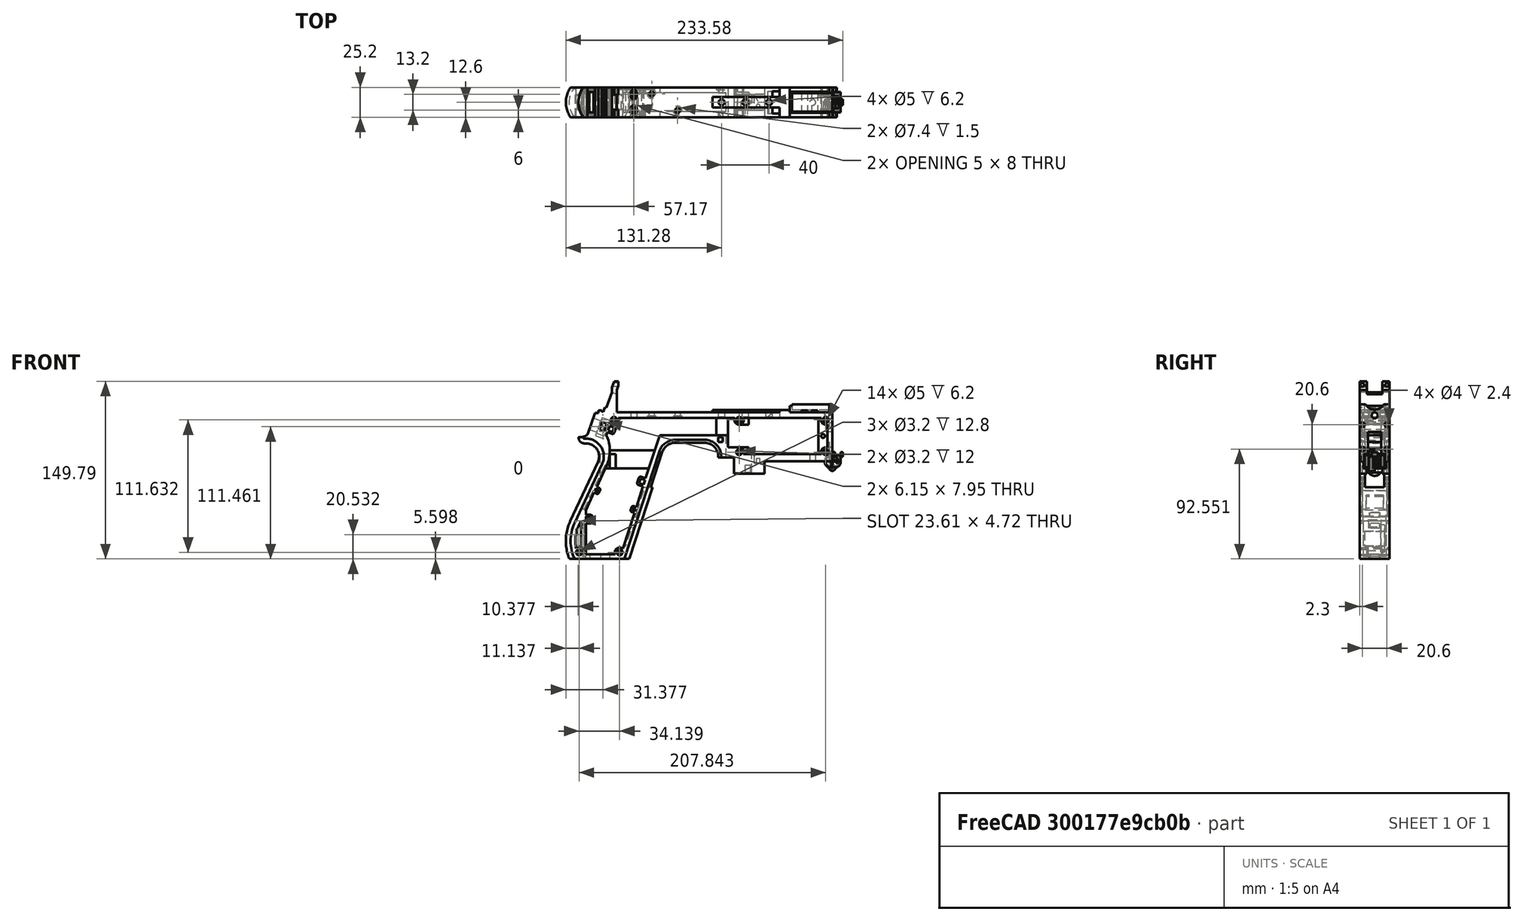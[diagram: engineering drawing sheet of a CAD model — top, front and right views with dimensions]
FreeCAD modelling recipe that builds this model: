
FCSTD DOCUMENT  (FreeCAD 1.0R39319 (Git))
Label: PICON-OF_ver_41
License: All rights reserved
LicenseURL: https://en.wikipedia.org/wiki/All_rights_reserved
objects: Sketcher::SketchObject×109, Part::Extrusion×52, Part::Cut×41, PartDesign::Pad×29, PartDesign::Pocket×18, PartDesign::Chamfer×15, PartDesign::Body×10, PartDesign::Fillet×6, PartDesign::SubtractivePipe×4, Part::Part2DObjectPython×4, PartDesign::SubtractiveLoft×4, PartDesign::Plane×2, PartDesign::SubShapeBinder×2, Part::Sweep×1, PartDesign::ShapeBinder×1, Part::MultiFuse×1, Mesh::Feature×1
note: 560 computed .brp shape members not serialized (recipe doc carries the construction recipe); baked Part::Feature solids carry a one-line shape summary decoded from their .brp

FEATURE [Sketcher::SketchObject] Sketch  label="corpo principale"
  ArcFitTolerance = 1e-06
  AttacherType = Attacher::AttachEngine3D
  AttachmentSupport = -> [XZ_Plane]
  FullyConstrained = true
  MakeInternals = false
  MapMode = 5
  Placement = pos=(0,0,0) rot=(1,0,0;1.5708rad)
  sketch-geometry (65):
    g0: LineSegment StartX=0 StartY=0 StartZ=0 EndX=-57.2 EndY=0 EndZ=0
    g1: LineSegment StartX=-57.2 StartY=0 StartZ=0 EndX=-57.2 EndY=-10.4 EndZ=0
    g2: LineSegment StartX=-57.2 StartY=-10.4 StartZ=0 EndX=-82.8 EndY=-10.4 EndZ=0
    g3: LineSegment StartX=-82.8 StartY=-10.4 StartZ=0 EndX=-82.8 EndY=3.2 EndZ=0
    g4: LineSegment StartX=-82.8 StartY=3.2 StartZ=0 EndX=-93.6 EndY=3.2 EndZ=0
    g5: LineSegment StartX=-93.6 StartY=3.2 StartZ=0 EndX=-93.6 EndY=4 EndZ=0
    g6: LineSegment StartX=-107.6 StartY=18 StartZ=0 EndX=-132.428 EndY=18 EndZ=0
    g7: LineSegment StartX=-145.743 StartY=8.32624 StartZ=0 EndX=-175.232 EndY=-82.4316 EndZ=0
    g8: LineSegment StartX=-175.232 StartY=-82.4316 StartZ=0 EndX=-217.232 EndY=-82.4316 EndZ=0
    g9: LineSegment StartX=-217.232 StartY=-52.1862 StartZ=0 EndX=-193.988 EndY=-2.33927 EndZ=0
    g10: LineSegment StartX=-206.196 StartY=23.0857 StartZ=0 EndX=-199.861 EndY=40.4914 EndZ=0
    g11: LineSegment StartX=-199.861 StartY=40.4914 StartZ=0 EndX=-197.061 EndY=40.4914 EndZ=0
    g12: LineSegment StartX=-197.061 StartY=40.4914 StartZ=0 EndX=-197.061 EndY=42.8914 EndZ=0
    g13: LineSegment StartX=-197.061 StartY=42.8914 StartZ=0 EndX=-194.261 EndY=42.8914 EndZ=0
    g14: LineSegment StartX=-194.261 StartY=42.8914 StartZ=0 EndX=-194.535 EndY=42.1397 EndZ=0
    g15: LineSegment StartX=-194.535 StartY=42.1397 StartZ=0 EndX=-193.031 EndY=41.5924 EndZ=0
    g16: LineSegment StartX=-193.031 StartY=41.5924 StartZ=0 EndX=-191.663 EndY=45.3512 EndZ=0
    g17: LineSegment StartX=-191.663 StartY=45.3512 StartZ=0 EndX=-190.536 EndY=44.9408 EndZ=0
    g18: LineSegment StartX=-190.536 StartY=44.9408 StartZ=0 EndX=-185.747 EndY=58.0965 EndZ=0
    g19: LineSegment StartX=-185.747 StartY=58.0965 StartZ=0 EndX=-185.747 EndY=62.0965 EndZ=0
    g20: LineSegment StartX=-185.747 StartY=62.0965 StartZ=0 EndX=-183.832 EndY=67.3588 EndZ=0
    g21: LineSegment StartX=-183.832 StartY=67.3588 StartZ=0 EndX=-180.232 EndY=67.3588 EndZ=0
    g22: LineSegment StartX=-180.232 StartY=67.3588 StartZ=0 EndX=-180.232 EndY=63.7588 EndZ=0
    g23: LineSegment StartX=-180.232 StartY=63.7588 StartZ=0 EndX=-181.6 EndY=60 EndZ=0
    g24: LineSegment StartX=-181.6 StartY=60 StartZ=0 EndX=-181.6 EndY=41.2 EndZ=0
    g25: LineSegment StartX=-181.6 StartY=41.2 StartZ=0 EndX=-100.8 EndY=41.2 EndZ=0
    g26: LineSegment StartX=-36 StartY=43.2 StartZ=0 EndX=-36 EndY=41.2 EndZ=0
    g27: LineSegment StartX=0 StartY=48 StartZ=0 EndX=0 EndY=0 EndZ=0
    g28: LineSegment StartX=-209.901 StartY=19.85 StartZ=0 EndX=-209.901 EndY=20.1 EndZ=0
    g29: LineSegment StartX=-208.001 StartY=22 StartZ=0 EndX=-207.747 EndY=22 EndZ=0
    g30: LineSegment StartX=-207.583 StartY=19 StartZ=0 EndX=-209.051 EndY=19 EndZ=0
    g31: ArcOfCircle CenterX=-208.001 CenterY=20.1 CenterZ=0 NormalX=0 NormalY=0 NormalZ=1 AngleXU=0 Radius=1.9 StartAngle=1.5708 EndAngle=3.14159
    g32: GeomPoint [constr] X=-209.901 Y=22 Z=0
    g33: ArcOfCircle CenterX=-209.051 CenterY=19.85 CenterZ=0 NormalX=0 NormalY=0 NormalZ=1 AngleXU=0 Radius=0.85 StartAngle=3.14159 EndAngle=4.71239
    g34: GeomPoint [constr] X=-209.901 Y=19 Z=0
    g35: ArcOfCircle CenterX=-207.747 CenterY=23.65 CenterZ=0 NormalX=0 NormalY=0 NormalZ=1 AngleXU=0 Radius=1.65 StartAngle=4.71239 EndAngle=5.93412
    g36: GeomPoint [constr] X=-206.591 Y=22 Z=0
    g37: LineSegment StartX=-4 StartY=6 StartZ=0 EndX=-4 EndY=36.4 EndZ=0
    g38: LineSegment StartX=-4 StartY=36.4 StartZ=0 EndX=-185.2 EndY=36.4 EndZ=0
    g39: LineSegment StartX=-185.2 StartY=36.4 StartZ=0 EndX=-190.441 EndY=22 EndZ=0
    g40: LineSegment StartX=-214.575 StartY=-78.4316 StartZ=0 EndX=-178.142 EndY=-78.4316 EndZ=0
    g41: LineSegment StartX=-178.142 StartY=-78.4316 StartZ=0 EndX=-145.51 EndY=22 EndZ=0
    g42: LineSegment StartX=-145.51 StartY=22 StartZ=0 EndX=-87.91 EndY=22 EndZ=0
    g43: LineSegment StartX=-87.91 StartY=22 StartZ=0 EndX=-87.91 EndY=11.6 EndZ=0
    g44: LineSegment StartX=-87.91 StartY=11.6 StartZ=0 EndX=-80.11 EndY=11.6 EndZ=0
    g45: LineSegment StartX=-80.11 StartY=11.6 StartZ=0 EndX=-80.11 EndY=6 EndZ=0
    g46: LineSegment StartX=-80.11 StartY=6 StartZ=0 EndX=-4 EndY=6 EndZ=0
    g47: LineSegment StartX=-190.363 StartY=-4.02975 StartZ=0 EndX=-213.607 EndY=-53.8767 EndZ=0
    g48: ArcOfCircle CenterX=-132.428 CenterY=4 CenterZ=0 NormalX=0 NormalY=0 NormalZ=1 AngleXU=0 Radius=14 StartAngle=1.5708 EndAngle=2.82743
    g49: GeomPoint [constr] X=-142.6 Y=18 Z=0
    g50: ArcOfCircle CenterX=-107.6 CenterY=4 CenterZ=0 NormalX=0 NormalY=0 NormalZ=1 AngleXU=0 Radius=14 StartAngle=0 EndAngle=1.5708
    g51: GeomPoint [constr] X=-93.6 Y=18 Z=0
    g52: ArcOfCircle CenterX=-184.801 CenterY=-67.3089 CenterZ=0 NormalX=0 NormalY=0 NormalZ=1 AngleXU=0 Radius=35.7833 StartAngle=2.70526 EndAngle=3.57792
    g53: ArcOfCircle CenterX=-207.583 CenterY=4 CenterZ=0 NormalX=0 NormalY=0 NormalZ=1 AngleXU=0 Radius=15 StartAngle=5.84685 EndAngle=7.85398
    g54: LineSegment [constr] StartX=-213.607 StartY=-53.8767 StartZ=0 EndX=-217.232 EndY=-52.1862 EndZ=0
    g55: ArcOfCircle CenterX=-184.801 CenterY=-67.3089 CenterZ=0 NormalX=0 NormalY=0 NormalZ=1 AngleXU=0 Radius=31.7833 StartAngle=2.70526 EndAngle=3.49911
    g56: ArcOfCircle CenterX=-218.095 CenterY=8.90192 CenterZ=0 NormalX=0 NormalY=0 NormalZ=1 AngleXU=0 Radius=30.5989 StartAngle=5.84685 EndAngle=6.72553
    g57: LineSegment StartX=-44.6 StartY=43.2 StartZ=0 EndX=-36 EndY=43.2 EndZ=0
    g58: LineSegment StartX=-100.8 StartY=41.2 StartZ=0 EndX=-44.6 EndY=41.2 EndZ=0
    g59: LineSegment StartX=-44.6 StartY=41.2 StartZ=0 EndX=-44.6 EndY=43.2 EndZ=0
    g60: LineSegment StartX=-2.4 StartY=48 StartZ=0 EndX=0 EndY=48 EndZ=0
    g61: LineSegment StartX=-36 StartY=41.2 StartZ=0 EndX=-2.4 EndY=41.2 EndZ=0
    g62: LineSegment StartX=-2.4 StartY=41.2 StartZ=0 EndX=-2.4 EndY=48 EndZ=0
    g63: LineSegment [constr] StartX=-181.6 StartY=36.4 StartZ=0 EndX=-152.209 EndY=36.4 EndZ=0
    g64: LineSegment [constr] StartX=-181.6 StartY=36.4 StartZ=0 EndX=-130.41 EndY=36.4 EndZ=0
  constraints (183):
    c: Coincident(g-1,g0)
    c: PointOnObject(g0,g-1)
    c: Coincident(g0,g1)
    c: Vertical(g1)
    c: Coincident(g1,g2)
    c: Horizontal(g2)
    c: Coincident(g2,g3)
    c: Vertical(g3)
    c: Coincident(g3,g4)
    c: Coincident(g4,g5)
    c: Vertical(g5)
    c: Horizontal(g6)
    c: Coincident(g7,g8)
    c: Horizontal(g8)
    c: Coincident(g10,g11)
    c: Horizontal(g11)
    c: Coincident(g11,g12)
    c: Vertical(g12)
    c: Coincident(g12,g13)
    c: Horizontal(g13)
    c: Coincident(g13,g14)
    c: Coincident(g14,g15)
    c: Coincident(g15,g16)
    c: Coincident(g16,g17)
    c: Coincident(g17,g18)
    c: Coincident(g18,g19)
    c: Vertical(g19)
    c: Coincident(g19,g20)
    c: Coincident(g20,g21)
    c: Horizontal(g21)
    c: Coincident(g21,g22)
    c: Vertical(g22)
    c: Coincident(g22,g23)
    c: Coincident(g23,g24)
    c: Vertical(g24)
    c: Coincident(g24,g25)
    c: Horizontal(g25)
    c: Coincident(g57,g26)
    c: Vertical(g26)
    c: Coincident(g26,g61)
    c: PointOnObject(g60,g-2)
    c: Coincident(g60,g27)
    c: Coincident(g27,g0)
    c: DistanceY(g27,g27) = 48
    c: DistanceY(g1,g1) = 10.4
    c: DistanceX(g0,g0) = 57.2
    c: DistanceX(g2,g2) = 25.6
    c: Horizontal(g4)
    c: DistanceY(g3,g3) = 13.6
    c: DistanceX(g4,g4) = 10.8
    c: DistanceY(g5,g51) = 14.8
    c: DistanceX(g49,g51) = 49
    c: Distance(g7,g49) = 105.6
    c: DistanceX(g61,g60) = 36
    c: DistanceX(g25,g25) = 80.8
    c: DistanceY(g24,g24) = 18.8
    c: DistanceY(g22,g22) = 3.6
    c: Distance(g23) = 4
    c: Angle(g-1,g23) = 1.22173
    c: DistanceX(g21,g21) = 3.6
    c: Distance(g20) = 5.6
    c: Angle(g-1,g20) = 1.22173
    c: DistanceY(g19,g19) = 4
    c: Distance(g18) = 14
    c: Angle(g-1,g18) = 1.22173
    c: Distance(g17) = 1.2
    c: Distance(g16) = 4
    c: Angle(g16) = 1.22173
    c: Perpendicular(g18,g17)
    c: Distance(g15) = 1.6
    c: Perpendicular(g16,g15)
    c: Distance(g14) = 0.8
    c: DistanceX(g13,g13) = 2.8
    c: Perpendicular(g15,g14)
    c: DistanceY(g12,g12) = 2.4
    c: DistanceX(g11,g11) = 2.8
    c: Distance(g9) = 55
    c: Angle(g9,g-1) = 2.00713
    c: Horizontal(g29)
    c: Vertical(g28)
    c: Horizontal(g30)
    c: PointOnObject(g32,g29)
    c: PointOnObject(g32,g28)
    c: Tangent(g29,g31) = 1.5708
    c: Tangent(g28,g31) = 1.5708
    c: PointOnObject(g34,g28)
    c: PointOnObject(g34,g30)
    c: Tangent(g28,g33) = 1.5708
    c: Tangent(g30,g33) = 1.5708
    c: PointOnObject(g36,g29)
    c: PointOnObject(g36,g10)
    c: Tangent(g29,g35) = -1.5708
    c: Tangent(g10,g35) = -1.5708
    c: Angle(g-1,g10) = 1.22173
    c: Radius(g35) = 1.65
    c: Vertical(g37)
    c: Coincident(g37,g38)
    c: Horizontal(g38)
    c: Coincident(g38,g39)
    c: Horizontal(g40)
    c: Coincident(g40,g41)
    c: Coincident(g41,g42)
    c: Horizontal(g42)
    c: Coincident(g42,g43)
    c: Vertical(g43)
    c: Coincident(g43,g44)
    c: Horizontal(g44)
    c: Coincident(g44,g45)
    c: Vertical(g45)
    c: Coincident(g45,g46)
    c: Coincident(g46,g37)
    c: Horizontal(g46)
    c: DistanceY(g0,g37) = 6
    c: DistanceX(g37,g0) = 4
    c: DistanceY(g37,g25) = 4.8
    c: DistanceX(g38,g38) = 181.2
    c: DistanceX(g42,g42) = 57.6
    c: DistanceY(g49,g41) = 4
    c: DistanceX(g41,g49) = 2.91
    c: DistanceY(g43,g43) = 10.4
    c: DistanceX(g44,g44) = 7.8
    c: DistanceY(g7,g40) = 4
    c: Distance(g47) = 55
    c: Angle(g-1,g39) = 1.22173
    c: PointOnObject(g49,g7)
    c: PointOnObject(g49,g6)
    c: Tangent(g7,g48) = -1.5708
    c: Tangent(g6,g48) = -1.5708
    c: PointOnObject(g51,g5)
    c: PointOnObject(g51,g6)
    c: Tangent(g5,g50) = -1.5708
    c: Tangent(g6,g50) = -1.5708
    c: Radius(g50) = 14
    c: Radius(g48) = 14
    c: DistanceX(g8,g8) = 42
    c: Angle(g7,g-1) = 1.88496
    c: Parallel(g41,g7)
    c: Parallel(g47,g9)
    c: Coincident(g52,g8)
    c: Tangent(g52,g9) = 1.5708
    c: DistanceX(g9,g8) = 0
    c: Tangent(g53,g9) = -1.5708
    c: Tangent(g53,g30) = -1.5708
    c: Diameter(g53) = 30
    c: DistanceY(g53,g0) = -4
    c: Coincident(g54,g47)
    c: Distance(g54) = 4
    c: Coincident(g54,g9)
    c: Coincident(g55,g40)
    c: Tangent(g55,g47) = -1.5708
    c: Coincident(g52,g55)
    c: Coincident(g56,g39)
    c: Tangent(g56,g47) = 1.5708
    c: Horizontal(g57)
    c: DistanceX(g57,g57) = 8.6
    c: Coincident(g58,g25)
    c: Horizontal(g58)
    c: Coincident(g59,g58)
    c: Vertical(g59)
    c: DistanceY(g58,g57) = 2
    c: DistanceX(g58,g58) = 56.2
    c: Coincident(g59,g57)
    c: DistanceY(g41,g36) = 0
    c: DistanceY(g36,g39) = 0
    c: DistanceY(g28,g28) = 0.25
    c: DistanceX(g30,g36) = 2.46
    c: DistanceX(g28,g29) = 1.9
    c: Coincident(g62,g60)
    c: Horizontal(g60)
    c: DistanceX(g62,g27) = 2.4
    c: Coincident(g61,g62)
    c: DistanceY(g26,g26) = 2
    c: Vertical(g62)
    c: DistanceY(g61,g60) = 6.8
    c: Horizontal(g61)
    c: Distance(g63) = 29.391
    c: PointOnObject(g63,g38)
    c: PointOnObject(g63,g38)
    c: Distance(g64) = 51.19
    c: PointOnObject(g64,g38)
    c: PointOnObject(g64,g38)
    c: DistanceX(g24,g63) = 0
    c: DistanceX(g24,g64) = 0
FEATURE [Part::Extrusion] Extrude  label="Extrude corpo principale"
  Base = -> Sketch
  Dir = (0,-1,2e-16)
  DirMode = 2
  FaceMakerClass = Part::FaceMakerBullseye
  FaceMakerMode = 3
  LengthFwd = 25.2
  LengthRev = 12.6
  Solid = true
  Symmetric = true
FEATURE [Sketcher::SketchObject] Sketch002  label="scavo grilletto"
  ArcFitTolerance = 1e-06
  AttachmentSupport = -> [XZ_Plane]
  ExternalGeometry = -> [Sketch]
  FullyConstrained = true
  MakeInternals = false
  MapMode = 5
  Placement = pos=(0,0,0) rot=(1,0,0;1.5708rad)
  sketch-geometry (4):
    g0: LineSegment StartX=-89.51 StartY=22 StartZ=0 EndX=-152.71 EndY=22 EndZ=0
    g1: LineSegment StartX=-152.71 StartY=22 StartZ=0 EndX=-167.006 EndY=-22 EndZ=0
    g2: LineSegment StartX=-167.006 StartY=-22 StartZ=0 EndX=-89.51 EndY=-22 EndZ=0
    g3: LineSegment StartX=-89.51 StartY=-22 StartZ=0 EndX=-89.51 EndY=22 EndZ=0
  constraints (12):
    c: Horizontal(g0)
    c: Coincident(g0,g1)
    c: Coincident(g1,g2)
    c: Horizontal(g2)
    c: Coincident(g2,g3)
    c: Coincident(g3,g0)
    c: Vertical(g3)
    c: Angle(g1,g0) = 1.88496
    c: DistanceY(g3,g3) = 44
    c: DistanceX(g0,g0) = 63.2
    c: DistanceX(g0,g-3) = 1.6
    c: DistanceY(g-3,g0) = 0
FEATURE [Sketcher::SketchObject] Sketch004  label="traiettoria arrotondamento impugnatura anteriore"
  ArcFitTolerance = 1e-06
  AttachmentSupport = -> [XZ_Plane]
  ExternalGeometry = -> [Sketch]
  FullyConstrained = true
  MakeInternals = false
  MapMode = 5
  Placement = pos=(0,0,0) rot=(1,0,0;1.5708rad)
  sketch-geometry (13):
    g0: LineSegment StartX=-175.232 StartY=-82.4316 StartZ=0 EndX=-145.743 EndY=8.32624 EndZ=0
    g1: LineSegment StartX=-93.6 StartY=3.2 StartZ=0 EndX=-93.6 EndY=4 EndZ=0
    g2: LineSegment StartX=-132.428 StartY=18 StartZ=0 EndX=-107.6 EndY=18 EndZ=0
    g3: ArcOfCircle CenterX=-132.428 CenterY=4 CenterZ=0 NormalX=0 NormalY=0 NormalZ=1 AngleXU=0 Radius=14 StartAngle=1.5708 EndAngle=2.82743
    g4: ArcOfCircle CenterX=-107.6 CenterY=4 CenterZ=0 NormalX=0 NormalY=0 NormalZ=1 AngleXU=0 Radius=14 StartAngle=0 EndAngle=1.5708
    g5: LineSegment StartX=-175.232 StartY=-82.4316 StartZ=0 EndX=-217.232 EndY=-82.4316 EndZ=0
    g6: LineSegment StartX=-217.232 StartY=-52.1862 StartZ=0 EndX=-193.988 EndY=-2.33927 EndZ=0
    g7: LineSegment StartX=-209.051 StartY=19 StartZ=0 EndX=-207.583 EndY=19 EndZ=0
    g8: LineSegment StartX=-209.901 StartY=20.1 StartZ=0 EndX=-209.901 EndY=19.85 EndZ=0
    g9: ArcOfCircle CenterX=-184.801 CenterY=-67.3089 CenterZ=0 NormalX=0 NormalY=0 NormalZ=1 AngleXU=0 Radius=35.7833 StartAngle=2.70526 EndAngle=3.57792
    g10: ArcOfCircle CenterX=-207.583 CenterY=4 CenterZ=0 NormalX=0 NormalY=0 NormalZ=1 AngleXU=0 Radius=15 StartAngle=5.84685 EndAngle=7.85398
    g11: ArcOfCircle CenterX=-209.051 CenterY=19.85 CenterZ=0 NormalX=0 NormalY=0 NormalZ=1 AngleXU=0 Radius=0.85 StartAngle=3.14159 EndAngle=4.71239
    g12: ArcOfCircle CenterX=-208.001 CenterY=20.1 CenterZ=0 NormalX=0 NormalY=0 NormalZ=1 AngleXU=0 Radius=1.9 StartAngle=1.5708 EndAngle=3.14159
  constraints (26):
    c: Coincident(g0,g-3)
    c: Coincident(g0,g-6)
    c: Coincident(g1,g-8)
    c: Coincident(g1,g-7)
    c: Coincident(g2,g-5)
    c: Coincident(g2,g-4)
    c: Coincident(g3,g2)
    c: Tangent(g3,g0) = 1.5708
    c: Coincident(g4,g1)
    c: Tangent(g4,g2) = 1.5708
    c: Coincident(g5,g0)
    c: Coincident(g5,g-9)
    c: Coincident(g6,g-12)
    c: Coincident(g6,g-11)
    c: Coincident(g7,g-15)
    c: Coincident(g7,g-14)
    c: Coincident(g8,g-16)
    c: Coincident(g8,g-17)
    c: Tangent(g9,g6) = 1.5708
    c: Coincident(g9,g5)
    c: Coincident(g10,g7)
    c: Tangent(g10,g6) = -1.5708
    c: Tangent(g11,g7) = -1.5708
    c: Coincident(g11,g8)
    c: Tangent(g12,g8) = -1.5708
    c: Coincident(g12,g-17)
FEATURE [PartDesign::Plane] DatumPlane  label="Piano per disegno arrotondamento impugnatura"
  AttachmentSupport = -> [Sketch]
  Length = 68.5841
  MapMode = 7
  Placement = pos=(-145.743,1.8e-15,8.32624) rot=(0.154555,0.154555,0.97582;1.59527rad)
  ResizeMode = 0
  Width = 191.269
FEATURE [Sketcher::SketchObject] Sketch005  label="forma arrotondamento impugnatura anteriore"
  ArcFitTolerance = 1e-06
  AttachmentSupport = -> [DatumPlane]
  FullyConstrained = true
  MakeInternals = false
  MapMode = 5
  Placement = pos=(-145.743,1.8e-15,8.32624) rot=(0.154555,0.154555,0.97582;1.59527rad)
  sketch-geometry (5):
    g0: GeomPoint [constr] X=0 Y=-4 Z=0
    g1: GeomPoint [constr] X=-12.6 Y=7.1e-15 Z=0
    g2: GeomPoint [constr] X=12.6 Y=4.97e-14 Z=0
    g3: LineSegment StartX=-12.6 StartY=7.1e-15 StartZ=0 EndX=12.6 EndY=4.97e-14 EndZ=0
    g4: ArcOfCircle CenterX=-3.88e-14 CenterY=17.845 CenterZ=0 NormalX=0 NormalY=0 NormalZ=1 AngleXU=0 Radius=21.845 StartAngle=4.09759 EndAngle=5.32718
  constraints (11):
    c: DistanceY(g0,g-1) = 4
    c: DistanceX(g-1,g0) = 0
    c: DistanceX(g1,g-1) = 12.6
    c: DistanceX(g-1,g2) = 12.6
    c: DistanceY(g-1,g2) = 0
    c: DistanceY(g-1,g1) = 0
    c: Coincident(g3,g1)
    c: Coincident(g3,g2)
    c: Coincident(g4,g1)
    c: Coincident(g4,g2)
    c: PointOnObject(g0,g4)
FEATURE [Part::Sweep] Sweep  label="Sweep impugnatura"
  Frenet = true
  Sections = -> [Sketch005]
  Solid = true
  Spine = -> Sketch [Edge32,Edge33,Edge34,Edge35,Edge36,Edge37,Edge38,Edge39,Edge40,Edge41,Edge42,Edge43,Edge44]
  Transition = 1
FEATURE [Sketcher::SketchObject] Sketch008  label="buchi e pulizie varie"
  ArcFitTolerance = 1e-06
  AttachmentSupport = -> [XZ_Plane]
  ExternalGeometry = -> [Sketch]
  FullyConstrained = true
  MakeInternals = false
  MapMode = 5
  Placement = pos=(0,0,0) rot=(1,0,0;1.5708rad)
  sketch-geometry (26):
    g0: LineSegment StartX=-96.278 StartY=20.155 StartZ=0 EndX=-92.278 EndY=20.155 EndZ=0
    g1: LineSegment StartX=-92.278 StartY=20.155 StartZ=0 EndX=-92.278 EndY=16.155 EndZ=0
    g2: LineSegment StartX=-92.278 StartY=16.155 StartZ=0 EndX=-96.278 EndY=16.155 EndZ=0
    g3: LineSegment StartX=-96.278 StartY=16.155 StartZ=0 EndX=-96.278 EndY=20.155 EndZ=0
    g4: LineSegment StartX=-222.232 StartY=-82.4316 StartZ=0 EndX=-170.232 EndY=-82.4316 EndZ=0
    g5: LineSegment StartX=-170.232 StartY=-82.4316 StartZ=0 EndX=-170.232 EndY=-86.4316 EndZ=0
    g6: LineSegment StartX=-170.232 StartY=-86.4316 StartZ=0 EndX=-222.232 EndY=-86.4316 EndZ=0
    g7: LineSegment StartX=-222.232 StartY=-86.4316 StartZ=0 EndX=-222.232 EndY=-82.4316 EndZ=0
    g8: LineSegment StartX=-213.901 StartY=20.1 StartZ=0 EndX=-213.901 EndY=26 EndZ=0
    g9: LineSegment StartX=-213.901 StartY=26 StartZ=0 EndX=-206.196 EndY=26 EndZ=0
    g10: LineSegment StartX=-17.4 StartY=42.8 StartZ=0 EndX=-12.4 EndY=42.8 EndZ=0
    g11: LineSegment StartX=-12.4 StartY=42.8 StartZ=0 EndX=-12.4 EndY=41.2 EndZ=0
    g12: LineSegment StartX=-12.4 StartY=41.2 StartZ=0 EndX=-17.4 EndY=41.2 EndZ=0
    g13: LineSegment StartX=-17.4 StartY=41.2 StartZ=0 EndX=-17.4 EndY=42.8 EndZ=0
    g14: LineSegment StartX=-25.9 StartY=42.8 StartZ=0 EndX=-20.9 EndY=42.8 EndZ=0
    g15: LineSegment StartX=-20.9 StartY=42.8 StartZ=0 EndX=-20.9 EndY=41.2 EndZ=0
    g16: LineSegment StartX=-20.9 StartY=41.2 StartZ=0 EndX=-25.9 EndY=41.2 EndZ=0
    g17: LineSegment StartX=-25.9 StartY=41.2 StartZ=0 EndX=-25.9 EndY=42.8 EndZ=0
    g18: GeomPoint [constr] X=-206.196 Y=23.0857 Z=0
    g19: GeomPoint [constr] X=-213.901 Y=20.1 Z=0
    g20: BSplineCurve PolesCount=4 KnotsCount=2 Degree=3 IsPeriodic=0
    g21-g24: Circle [constr] x4 (B-spline internal-alignment scaffolding for g20; pole/knot coordinates omitted)
    g25: LineSegment StartX=-206.196 StartY=26 StartZ=0 EndX=-206.196 EndY=23.0857 EndZ=0
  constraints (73):
    c: Horizontal(g0)
    c: Coincident(g1,g0)
    c: Vertical(g1)
    c: Coincident(g2,g1)
    c: Horizontal(g2)
    c: Coincident(g3,g2)
    c: Coincident(g3,g0)
    c: Vertical(g3)
    c: DistanceX(g0,g-4) = 4.368
    c: DistanceY(g0,g-4) = 1.845
    c: DistanceY(g1,g1) = 4
    c: DistanceX(g2,g2) = 4
    c: Horizontal(g4)
    c: Coincident(g5,g4)
    c: Vertical(g5)
    c: Coincident(g6,g5)
    c: Horizontal(g6)
    c: Coincident(g7,g6)
    c: Coincident(g7,g4)
    c: Vertical(g7)
    c: DistanceY(g7,g7) = 4
    c: DistanceX(g4,g-5) = 5
    c: DistanceX(g-5,g4) = 5
    c: DistanceY(g4,g-5) = 0
    c: Coincident(g9,g8)
    c: Parallel(g9,g-6)
    c: DistanceX(g8,g-8) = 4
    c: Horizontal(g10)
    c: Coincident(g11,g10)
    c: Vertical(g11)
    c: Coincident(g12,g11)
    c: Horizontal(g12)
    c: Coincident(g13,g12)
    c: Coincident(g13,g10)
    c: Vertical(g13)
    c: Horizontal(g14)
    c: Coincident(g15,g14)
    c: Vertical(g15)
    c: Coincident(g16,g15)
    c: Horizontal(g16)
    c: Coincident(g17,g16)
    c: Coincident(g17,g14)
    c: Vertical(g17)
    c: DistanceY(g11,g10) = 1.6
    c: DistanceX(g10,g10) = 5
    c: DistanceY(g15,g14) = 1.6
    c: DistanceX(g14,g14) = 5
    c: DistanceX(g15,g12) = 3.5
    c: DistanceX(g11,g-9) = 10
    c: DistanceY(g-9,g11) = 0
    c: DistanceY(g-9,g15) = 0
    c: Perpendicular(g8,g9)
    c: DistanceY(g-7,g9) = 4
    c: DistanceY(g8,g-8) = 0
    c: InternalAlignment(g18,g20)
    c: InternalAlignment(g19,g20)
    c: InternalAlignment(g21,g20)
    c: Weight(g21) = 1
    c: InternalAlignment(g22,g20)
    c: Equal(g22,g21)
    c: InternalAlignment(g23,g20)
    c: Equal(g23,g21)
    c: InternalAlignment(g24,g20)
    c: Equal(g24,g21)
    c: Coincident(g18,g-12)
    c: Coincident(g19,g8)
    c: Coincident(g25,g9)
    c: Coincident(g25,g20)
    c: Vertical(g25)
    c: DistanceY(g20,g23) = 0
    c: DistanceY(g22,g18) = 2.26
    c: DistanceX(g22,g18) = 0.93
    c: DistanceX(g20,g23) = 2.9
FEATURE [Part::Extrusion] Extrude004  label="Extrude Buchi e pulizie varie"
  Base = -> Sketch008
  Dir = (0,-1,2e-16)
  DirMode = 2
  FaceMakerClass = Part::FaceMakerBullseye
  FaceMakerMode = 3
  LengthFwd = 25.2
  LengthRev = 0
  Solid = true
  Symmetric = true
FEATURE [Sketcher::SketchObject] Sketch009  label="rinforzi"
  ArcFitTolerance = 1e-06
  AttachmentSupport = -> [XZ_Plane]
  ExternalGeometry = -> [Sketch]
  FullyConstrained = true
  MakeInternals = false
  MapMode = 5
  Placement = pos=(0,0,0) rot=(1,0,0;1.5708rad)
  sketch-geometry (9):
    g0: LineSegment StartX=-87.91 StartY=22 StartZ=0 EndX=-87.91 EndY=36.4 EndZ=0
    g1: LineSegment StartX=-87.91 StartY=36.4 StartZ=0 EndX=-97.91 EndY=36.4 EndZ=0
    g2: LineSegment StartX=-97.91 StartY=36.4 StartZ=0 EndX=-97.91 EndY=22 EndZ=0
    g3: LineSegment StartX=-97.91 StartY=22 StartZ=0 EndX=-87.91 EndY=22 EndZ=0
    g4: LineSegment StartX=-149.713 StartY=9.06563 StartZ=0 EndX=-154.586 EndY=-5.93437 EndZ=0
    g5: LineSegment StartX=-154.586 StartY=-5.93437 StartZ=0 EndX=-191.863 EndY=-5.93437 EndZ=0
    g6: LineSegment StartX=-191.863 StartY=-5.93437 StartZ=0 EndX=-191.863 EndY=9.06563 EndZ=0
    g7: LineSegment StartX=-191.863 StartY=9.06563 StartZ=0 EndX=-149.713 EndY=9.06563 EndZ=0
    g8: LineSegment [constr] StartX=-145.51 StartY=22 StartZ=0 EndX=-149.713 EndY=9.06563 EndZ=0
  constraints (25):
    c: Vertical(g0)
    c: Coincident(g1,g0)
    c: Horizontal(g1)
    c: Coincident(g2,g1)
    c: Vertical(g2)
    c: Coincident(g3,g2)
    c: Coincident(g3,g0)
    c: Horizontal(g3)
    c: Coincident(g0,g-4)
    c: DistanceX(g3,g3) = 10
    c: DistanceY(g0,g-3) = 0
    c: Coincident(g5,g4)
    c: Horizontal(g5)
    c: Coincident(g6,g5)
    c: Vertical(g6)
    c: Coincident(g7,g6)
    c: Coincident(g7,g4)
    c: Horizontal(g7)
    c: Distance(g8) = 13.6
    c: Parallel(g-6,g8)
    c: Coincident(g-6,g8)
    c: Parallel(g4,g-6)
    c: DistanceY(g4,g4) = 15
    c: Coincident(g4,g8)
    c: DistanceX(g-5,g5) = -1.5
FEATURE [Part::Extrusion] Extrude001  label="Extrude scavo grilletto"
  Base = -> Sketch002
  Dir = (0,-1,2e-16)
  DirMode = 2
  FaceMakerClass = Part::FaceMakerBullseye
  FaceMakerMode = 3
  LengthFwd = 16
  LengthRev = 0
  Solid = true
  Symmetric = true
FEATURE [Part::Extrusion] Extrude005  label="Extrude Rinforzi"
  Base = -> Sketch009
  Dir = (0,-1,2e-16)
  DirMode = 2
  FaceMakerClass = Part::FaceMakerBullseye
  FaceMakerMode = 3
  LengthFwd = 2
  LengthRev = 0
  Placement = pos=(0,12.6,0) rot=(0,0,1;0rad)
  Solid = true
  Symmetric = false
FEATURE [PartDesign::ShapeBinder] CopyCut
  TraceSupport = false
FEATURE [PartDesign::Plane] DatumPlane001
  AttachmentSupport = -> [CopyCut]
  Length = 60
  MapMode = 5
  Placement = pos=(0,12.6,0) rot=(0,0.707107,0.707107;3.14159rad)
  ResizeMode = 0
  Width = 60
FEATURE [Sketcher::SketchObject] Sketch010  label="buco neopixel"
  ArcFitTolerance = 1e-06
  AttachmentSupport = -> [XZ_Plane]
  ExternalGeometry = -> [Sketch]
  FullyConstrained = true
  MakeInternals = false
  MapMode = 5
  Placement = pos=(0,0,0) rot=(1,0,0;1.5708rad)
  sketch-geometry (5):
    g0: LineSegment [constr] StartX=-199.861 StartY=40.4914 StartZ=0 EndX=-201.368 EndY=36.3521 EndZ=0
    g1: LineSegment StartX=-201.368 StartY=36.3521 StartZ=0 EndX=-204.932 EndY=26.5605 EndZ=0
    g2: LineSegment StartX=-201.368 StartY=36.3521 StartZ=0 EndX=-180.2 EndY=28.6477 EndZ=0
    g3: LineSegment StartX=-180.2 StartY=28.6477 StartZ=0 EndX=-183.764 EndY=18.8561 EndZ=0
    g4: LineSegment StartX=-183.764 StartY=18.8561 StartZ=0 EndX=-204.932 EndY=26.5605 EndZ=0
  constraints (14):
    c: Parallel(g0,g-3)
    c: Distance(g0) = 4.405
    c: Coincident(g0,g-3)
    c: Coincident(g2,g1)
    c: Coincident(g3,g2)
    c: Coincident(g4,g3)
    c: Coincident(g4,g1)
    c: Parallel(g1,g-3)
    c: Distance(g1) = 10.42
    c: Coincident(g1,g0)
    c: Parallel(g2,g4)
    c: Perpendicular(g1,g2)
    c: DistanceX(g-4,g2) = 5
    c: Parallel(g3,g1)
FEATURE [Part::Extrusion] Extrude006  label="Extrude buco neopixel"
  Base = -> Sketch010
  Dir = (0,-1,2e-16)
  DirMode = 2
  FaceMakerClass = Part::FaceMakerBullseye
  FaceMakerMode = 3
  LengthFwd = 17.2
  LengthRev = 0
  Solid = true
  Symmetric = true
FEATURE [Sketcher::SketchObject] Sketch011  label="fermo grilletto"
  ArcFitTolerance = 1e-06
  AttachmentSupport = -> [XZ_Plane]
  ExternalGeometry = -> [Sketch]
  FullyConstrained = true
  MakeInternals = false
  MapMode = 5
  Placement = pos=(0,0,0) rot=(1,0,0;1.5708rad)
  sketch-geometry (18):
    g0: LineSegment [constr] StartX=-145.51 StartY=22 StartZ=0 EndX=-157.347 EndY=-14.4293 EndZ=0
    g1: LineSegment [constr] StartX=-157.347 StartY=-14.4293 StartZ=0 EndX=-157.841 EndY=-15.951 EndZ=0
    g2: LineSegment StartX=-161.151 StartY=-13.1932 StartZ=0 EndX=-155.825 EndY=-14.9237 EndZ=0
    g3: LineSegment StartX=-163.167 StartY=-14.2205 StartZ=0 EndX=-164.403 EndY=-18.0247 EndZ=0
    g4: LineSegment StartX=-163.376 StartY=-20.0408 StartZ=0 EndX=-158.05 EndY=-21.7713 EndZ=0
    g5: LineSegment StartX=-158.05 StartY=-21.7713 StartZ=0 EndX=-155.825 EndY=-14.9237 EndZ=0
    g6: LineSegment StartX=-161.645 StartY=-14.7149 StartZ=0 EndX=-157.841 EndY=-15.951 EndZ=0
    g7: LineSegment StartX=-157.841 StartY=-15.951 StartZ=0 EndX=-159.077 EndY=-19.7552 EndZ=0
    g8: LineSegment StartX=-159.077 StartY=-19.7552 StartZ=0 EndX=-162.881 EndY=-18.5191 EndZ=0
    g9: LineSegment StartX=-162.881 StartY=-18.5191 StartZ=0 EndX=-161.645 EndY=-14.7149 EndZ=0
    g10: LineSegment [constr] StartX=-161.645 StartY=-14.7149 StartZ=0 EndX=-161.151 EndY=-13.1932 EndZ=0
    g11: LineSegment [constr] StartX=-159.077 StartY=-19.7552 StartZ=0 EndX=-157.555 EndY=-20.2496 EndZ=0
    g12: LineSegment [constr] StartX=-159.077 StartY=-19.7552 StartZ=0 EndX=-159.572 EndY=-21.2769 EndZ=0
    g13: LineSegment [constr] StartX=-161.645 StartY=-14.7149 StartZ=0 EndX=-163.167 EndY=-14.2205 EndZ=0
    g14: ArcOfCircle CenterX=-161.645 CenterY=-14.7149 CenterZ=0 NormalX=0 NormalY=0 NormalZ=1 AngleXU=0 Radius=1.6 StartAngle=1.25664 EndAngle=2.82743
    g15: GeomPoint [constr] X=-162.673 Y=-12.6988 Z=0
    g16: ArcOfCircle CenterX=-162.881 CenterY=-18.5191 CenterZ=0 NormalX=0 NormalY=0 NormalZ=1 AngleXU=0 Radius=1.6 StartAngle=2.82743 EndAngle=4.39823
    g17: GeomPoint [constr] X=-164.897 Y=-19.5464 Z=0
  constraints (48):
    c: Parallel(g0,g-3)
    c: Distance(g0) = 38.304
    c: Coincident(g0,g-3)
    c: Parallel(g1,g-3)
    c: Distance(g1) = 1.6
    c: Coincident(g1,g0)
    c: Coincident(g5,g4)
    c: Coincident(g5,g2)
    c: Coincident(g7,g6)
    c: Coincident(g8,g7)
    c: Coincident(g9,g8)
    c: Coincident(g9,g6)
    c: Parallel(g7,g-3)
    c: Parallel(g9,g7)
    c: Perpendicular(g6,g7)
    c: Parallel(g6,g8)
    c: Distance(g6) = 4
    c: Distance(g9) = 4
    c: Parallel(g5,g7)
    c: Parallel(g9,g3)
    c: Parallel(g2,g6)
    c: Parallel(g4,g8)
    c: Parallel(g13,g6)
    c: Parallel(g10,g9)
    c: Parallel(g11,g8)
    c: Parallel(g12,g7)
    c: Distance(g10) = 1.6
    c: Distance(g13) = 1.6
    c: Distance(g12) = 1.6
    c: Distance(g11) = 1.6
    c: Coincident(g10,g6)
    c: Coincident(g13,g6)
    c: Coincident(g12,g7)
    c: Coincident(g11,g7)
    c: Distance(g10,g15) = 1.6
    c: Distance(g15,g13) = 1.6
    c: Distance(g4,g12) = 1.6
    c: Distance(g4,g11) = 1.6
    c: PointOnObject(g15,g2)
    c: Tangent(g3,g14) = -1.5708
    c: Tangent(g2,g14) = 1.5708
    c: PointOnObject(g17,g4)
    c: PointOnObject(g17,g3)
    c: Tangent(g4,g16) = -1.5708
    c: Tangent(g3,g16) = -1.5708
    c: Equal(g16,g14)
    c: Coincident(g16,g8)
    c: Coincident(g6,g1)
FEATURE [Part::Extrusion] Extrude007  label="Extrude fermo grilletto"
  Base = -> Sketch011
  Dir = (0,-1,2e-16)
  DirMode = 2
  FaceMakerClass = Part::FaceMakerBullseye
  FaceMakerMode = 3
  LengthFwd = 25.2
  LengthRev = 0
  Solid = true
  Symmetric = true
FEATURE [Sketcher::SketchObject] Sketch012  label="buco oled"
  ArcFitTolerance = 1e-06
  AttachmentSupport = -> [XZ_Plane]
  ExternalGeometry = -> [Sketch]
  FullyConstrained = true
  MakeInternals = false
  MapMode = 5
  Placement = pos=(0,0,0) rot=(1,0,0;1.5708rad)
  sketch-geometry (4):
    g0: LineSegment StartX=-185.747 StartY=58.0965 StartZ=0 EndX=-180.232 EndY=56.0891 EndZ=0
    g1: LineSegment StartX=-185.747 StartY=58.0965 StartZ=0 EndX=-185.747 EndY=67.3588 EndZ=0
    g2: LineSegment StartX=-185.747 StartY=67.3588 StartZ=0 EndX=-180.232 EndY=67.3588 EndZ=0
    g3: LineSegment StartX=-180.232 StartY=67.3588 StartZ=0 EndX=-180.232 EndY=56.0891 EndZ=0
  constraints (10):
    c: Coincident(g1,g0)
    c: Coincident(g2,g1)
    c: Coincident(g3,g2)
    c: Coincident(g3,g0)
    c: Parallel(g1,g-5)
    c: Perpendicular(g-3,g0)
    c: Parallel(g2,g-6)
    c: Parallel(g3,g-4)
    c: Coincident(g0,g-5)
    c: Coincident(g2,g-6)
FEATURE [Part::Extrusion] Extrude008  label="Extrude buco oled"
  Base = -> Sketch012
  Dir = (0,-1,2e-16)
  DirMode = 2
  FaceMakerClass = Part::FaceMakerBullseye
  FaceMakerMode = 3
  LengthFwd = 12.8
  LengthRev = 0
  Solid = true
  Symmetric = true
FEATURE [Sketcher::SketchObject] Sketch013  label="buco pompa"
  ArcFitTolerance = 1e-06
  AttachmentSupport = -> [XZ_Plane]
  ExternalGeometry = -> [Sketch]
  FullyConstrained = true
  MakeInternals = false
  MapMode = 5
  Placement = pos=(0,0,0) rot=(1,0,0;1.5708rad)
  sketch-geometry (8):
    g0: LineSegment StartX=-82.8 StartY=-10.4 StartZ=0 EndX=-82.8 EndY=-9.6 EndZ=0
    g1: LineSegment StartX=-82.8 StartY=-9.6 StartZ=0 EndX=-67.9 EndY=-9.6 EndZ=0
    g2: LineSegment StartX=-67.9 StartY=-9.6 StartZ=0 EndX=-67.9 EndY=6 EndZ=0
    g3: LineSegment StartX=-67.9 StartY=6 StartZ=0 EndX=-65.9 EndY=6 EndZ=0
    g4: LineSegment StartX=-65.9 StartY=6 StartZ=0 EndX=-65.9 EndY=-1.7 EndZ=0
    g5: LineSegment StartX=-65.9 StartY=-1.7 StartZ=0 EndX=-57.2 EndY=-1.7 EndZ=0
    g6: LineSegment StartX=-57.2 StartY=-1.7 StartZ=0 EndX=-57.2 EndY=-10.4 EndZ=0
    g7: LineSegment StartX=-57.2 StartY=-10.4 StartZ=0 EndX=-82.8 EndY=-10.4 EndZ=0
  constraints (22):
    c: Vertical(g0)
    c: Coincident(g1,g0)
    c: Horizontal(g1)
    c: Coincident(g2,g1)
    c: Vertical(g2)
    c: Coincident(g3,g2)
    c: Horizontal(g3)
    c: Coincident(g4,g3)
    c: Vertical(g4)
    c: Coincident(g5,g4)
    c: Horizontal(g5)
    c: Coincident(g6,g5)
    c: Vertical(g6)
    c: Coincident(g7,g6)
    c: Coincident(g7,g0)
    c: DistanceY(g0,g0) = 0.8
    c: DistanceY(g6,g6) = 8.7
    c: DistanceX(g1,g1) = 14.9
    c: DistanceX(g3,g3) = 2
    c: Coincident(g0,g-4)
    c: DistanceY(g2,g-6) = 0
    c: Coincident(g6,g-5)
FEATURE [Part::Extrusion] Extrude009  label="Extrude buco pompa"
  Base = -> Sketch013
  Dir = (0,-1,2e-16)
  DirMode = 2
  FaceMakerClass = Part::FaceMakerBullseye
  FaceMakerMode = 3
  LengthFwd = 13.2
  LengthRev = 0
  Solid = true
  Symmetric = true
FEATURE [Sketcher::SketchObject] Sketch014  label="buco frontale"
  ArcFitTolerance = 1e-06
  AttachmentSupport = -> [XZ_Plane]
  ExternalGeometry = -> [Sketch]
  FullyConstrained = true
  MakeInternals = false
  MapMode = 5
  Placement = pos=(0,0,0) rot=(1,0,0;1.5708rad)
  sketch-geometry (10):
    g0: LineSegment StartX=0 StartY=0 StartZ=0 EndX=0 EndY=24.671 EndZ=0
    g1: LineSegment StartX=0 StartY=24.671 StartZ=0 EndX=-4 EndY=24.671 EndZ=0
    g2: LineSegment StartX=-4 StartY=24.671 StartZ=0 EndX=-4 EndY=16 EndZ=0
    g3: LineSegment StartX=-4 StartY=16 StartZ=0 EndX=-2.4 EndY=16 EndZ=0
    g4: LineSegment StartX=-2.4 StartY=16 StartZ=0 EndX=-2.4 EndY=10 EndZ=0
    g5: LineSegment StartX=-2.4 StartY=10 StartZ=0 EndX=-12 EndY=10 EndZ=0
    g6: LineSegment StartX=-12 StartY=10 StartZ=0 EndX=-12 EndY=6 EndZ=0
    g7: LineSegment StartX=-12 StartY=6 StartZ=0 EndX=-2.4 EndY=6 EndZ=0
    g8: LineSegment StartX=-2.4 StartY=6 StartZ=0 EndX=-2.4 EndY=0 EndZ=0
    g9: LineSegment StartX=-2.4 StartY=0 StartZ=0 EndX=0 EndY=0 EndZ=0
  constraints (29):
    c: Vertical(g0)
    c: Coincident(g1,g0)
    c: Horizontal(g1)
    c: Coincident(g2,g1)
    c: Vertical(g2)
    c: Coincident(g3,g2)
    c: Horizontal(g3)
    c: Coincident(g4,g3)
    c: Vertical(g4)
    c: Coincident(g5,g4)
    c: Horizontal(g5)
    c: Coincident(g6,g5)
    c: Vertical(g6)
    c: Coincident(g7,g6)
    c: Coincident(g8,g7)
    c: Vertical(g8)
    c: Coincident(g9,g8)
    c: Coincident(g9,g0)
    c: Horizontal(g9)
    c: DistanceY(g0,g0) = 24.671
    c: Horizontal(g7)
    c: DistanceY(g6,g6) = 4
    c: DistanceY(g4,g4) = 6
    c: DistanceX(g9,g9) = 2.4
    c: Coincident(g0,g-1)
    c: DistanceY(g-3,g7) = 0
    c: DistanceX(g8,g4) = 0
    c: DistanceX(g-3,g1) = 0
    c: DistanceX(g6,g-3) = 8
FEATURE [Part::Extrusion] Extrude010  label="Extrude buco frontale"
  Base = -> Sketch014
  Dir = (0,-1,2e-16)
  DirMode = 2
  FaceMakerClass = Part::FaceMakerBullseye
  FaceMakerMode = 3
  LengthFwd = 11.2
  LengthRev = 0
  Solid = true
  Symmetric = true
FEATURE [Sketcher::SketchObject] Sketch015  label="guida rail"
  ArcFitTolerance = 1e-06
  AttachmentSupport = -> [XZ_Plane]
  ExternalGeometry = -> [Sketch]
  FullyConstrained = true
  MakeInternals = false
  MapMode = 5
  Placement = pos=(0,0,0) rot=(1,0,0;1.5708rad)
  sketch-geometry (4):
    g0: LineSegment StartX=-100.8 StartY=43.2 StartZ=0 EndX=-44.6 EndY=43.2 EndZ=0
    g1: LineSegment StartX=-44.6 StartY=43.2 StartZ=0 EndX=-44.6 EndY=41.2 EndZ=0
    g2: LineSegment StartX=-44.6 StartY=41.2 StartZ=0 EndX=-100.8 EndY=41.2 EndZ=0
    g3: LineSegment StartX=-100.8 StartY=41.2 StartZ=0 EndX=-100.8 EndY=43.2 EndZ=0
  constraints (9):
    c: Horizontal(g0)
    c: Coincident(g1,g0)
    c: Coincident(g2,g1)
    c: Coincident(g3,g2)
    c: Coincident(g3,g0)
    c: Vertical(g3)
    c: Coincident(g2,g-3)
    c: Coincident(g1,g-3)
    c: Coincident(g0,g-4)
FEATURE [Part::Extrusion] Extrude011  label="Extrude guida rail"
  Base = -> Sketch015
  Dir = (0,-1,2e-16)
  DirMode = 2
  FaceMakerClass = Part::FaceMakerBullseye
  FaceMakerMode = 3
  LengthFwd = 9
  LengthRev = 0
  Solid = true
  Symmetric = true
FEATURE [Sketcher::SketchObject] Sketch016  label="guide per coperture laterali"
  ArcFitTolerance = 1e-06
  AttachmentSupport = -> [XZ_Plane]
  ExternalGeometry = -> [Sketch]
  FullyConstrained = true
  MakeInternals = false
  MapMode = 5
  Placement = pos=(0,0,0) rot=(1,0,0;1.5708rad)
  sketch-geometry (14):
    g0: Circle CenterX=-5.6 CenterY=7.6 CenterZ=0 NormalX=0 NormalY=0 NormalZ=1 AngleXU=0 Radius=1.6
    g1: Circle CenterX=-5.6 CenterY=7.6 CenterZ=0 NormalX=0 NormalY=0 NormalZ=1 AngleXU=0 Radius=4
    g2: Circle CenterX=-5.6 CenterY=34.8 CenterZ=0 NormalX=0 NormalY=0 NormalZ=1 AngleXU=0 Radius=1.6
    g3: Circle CenterX=-5.6 CenterY=34.8 CenterZ=0 NormalX=0 NormalY=0 NormalZ=1 AngleXU=0 Radius=4
    g4: Circle CenterX=-184.08 CenterY=34.8 CenterZ=0 NormalX=0 NormalY=0 NormalZ=1 AngleXU=0 Radius=1.6
    g5: Circle CenterX=-184.08 CenterY=34.8 CenterZ=0 NormalX=0 NormalY=0 NormalZ=1 AngleXU=0 Radius=4
    g6: Circle CenterX=-179.305 CenterY=-76.8316 CenterZ=0 NormalX=0 NormalY=0 NormalZ=1 AngleXU=0 Radius=1.6
    g7: Circle CenterX=-179.305 CenterY=-76.8316 CenterZ=0 NormalX=0 NormalY=0 NormalZ=1 AngleXU=0 Radius=4
    g8: Circle CenterX=-213.443 CenterY=-76.8316 CenterZ=0 NormalX=0 NormalY=0 NormalZ=1 AngleXU=0 Radius=1.6
    g9: Circle CenterX=-213.443 CenterY=-76.8316 CenterZ=0 NormalX=0 NormalY=0 NormalZ=1 AngleXU=0 Radius=4
    g10: Circle CenterX=-78.51 CenterY=7.6 CenterZ=0 NormalX=0 NormalY=0 NormalZ=1 AngleXU=0 Radius=1.6
    g11: Circle CenterX=-78.51 CenterY=7.6 CenterZ=0 NormalX=0 NormalY=0 NormalZ=1 AngleXU=0 Radius=4
    g12: Circle CenterX=-78.51 CenterY=34.8 CenterZ=0 NormalX=0 NormalY=0 NormalZ=1 AngleXU=0 Radius=1.6
    g13: Circle CenterX=-78.51 CenterY=34.8 CenterZ=0 NormalX=0 NormalY=0 NormalZ=1 AngleXU=0 Radius=4
  constraints (35):
    c: Diameter(g0) = 3.2
    c: Diameter(g1) = 8
    c: Coincident(g0,g1)
    c: Diameter(g2) = 3.2
    c: Diameter(g3) = 8
    c: Coincident(g3,g2)
    c: Tangent(g2,g-7)
    c: Diameter(g4) = 3.2
    c: Diameter(g5) = 8
    c: Coincident(g5,g4)
    c: Tangent(g4,g-7)
    c: Tangent(g4,g-8)
    c: Diameter(g6) = 3.2
    c: Diameter(g7) = 8
    c: Coincident(g7,g6)
    c: Tangent(g6,g-9)
    c: Tangent(g6,g-10)
    c: Diameter(g8) = 3.2
    c: Diameter(g9) = 8
    c: Coincident(g9,g8)
    c: Tangent(g8,g-10)
    c: Tangent(g8,g-11)
    c: Diameter(g10) = 3.2
    c: Diameter(g11) = 8
    c: Diameter(g12) = 3.2
    c: Diameter(g13) = 8
    c: Coincident(g12,g13)
    c: Coincident(g10,g11)
    c: Tangent(g12,g-7)
    c: DistanceX(g12,g10) = 0
    c: Tangent(g2,g-6)
    c: Tangent(g0,g-6)
    c: Tangent(g0,g-3)
    c: Tangent(g10,g-3)
    c: Tangent(g10,g-4)
FEATURE [Part::Extrusion] Extrude012  label="extrude guide per coperture laterali"
  Base = -> Sketch016
  Dir = (0,-1,2e-16)
  DirMode = 2
  FaceMakerClass = Part::FaceMakerBullseye
  FaceMakerMode = 3
  LengthFwd = 25.2
  LengthRev = 0
  Solid = true
  Symmetric = true
FEATURE [Sketcher::SketchObject] Sketch017  label="supporto CAM"
  ArcFitTolerance = 1e-06
  AttachmentSupport = -> [XZ_Plane]
  ExternalGeometry = -> [Sketch]
  FullyConstrained = true
  MakeInternals = false
  MapMode = 5
  Placement = pos=(0,0,0) rot=(1,0,0;1.5708rad)
  sketch-geometry (6):
    g0: LineSegment StartX=-2.4 StartY=48 StartZ=0 EndX=-2.4 EndY=41.2 EndZ=0
    g1: LineSegment StartX=-2.4 StartY=48 StartZ=0 EndX=-34 EndY=48 EndZ=0
    g2: LineSegment StartX=-34 StartY=48 StartZ=0 EndX=-34 EndY=46.72 EndZ=0
    g3: LineSegment StartX=-34 StartY=46.72 StartZ=0 EndX=-36 EndY=46.72 EndZ=0
    g4: LineSegment StartX=-36 StartY=46.72 StartZ=0 EndX=-36 EndY=41.2 EndZ=0
    g5: LineSegment StartX=-36 StartY=41.2 StartZ=0 EndX=-2.4 EndY=41.2 EndZ=0
  constraints (15):
    c: Coincident(g1,g0)
    c: Horizontal(g1)
    c: Coincident(g2,g1)
    c: Vertical(g2)
    c: Coincident(g3,g2)
    c: Horizontal(g3)
    c: Coincident(g4,g3)
    c: Coincident(g5,g4)
    c: DistanceX(g1,g0) = 31.6
    c: Coincident(g5,g0)
    c: Vertical(g4)
    c: DistanceY(g2,g1) = 1.28
    c: Coincident(g0,g-3)
    c: Coincident(g0,g-3)
    c: Coincident(g4,g-4)
FEATURE [Part::Extrusion] Extrude013  label="Extrude supporto CAM"
  Base = -> Sketch017
  Dir = (0,-1,2e-16)
  DirMode = 2
  FaceMakerClass = Part::FaceMakerBullseye
  FaceMakerMode = 3
  LengthFwd = 17.8
  LengthRev = 0
  Solid = true
  Symmetric = true
FEATURE [Sketcher::SketchObject] Sketch018  label="Scavo CAM"
  ArcFitTolerance = 1e-06
  AttachmentSupport = -> [YZ_Plane]
  ExternalGeometry = -> [Sketch]
  FullyConstrained = true
  MakeInternals = false
  MapMode = 5
  Placement = pos=(0,0,0) rot=(0.57735,0.57735,0.57735;2.0944rad)
  sketch-geometry (4):
    g0: LineSegment StartX=-7.73 StartY=48 StartZ=0 EndX=7.73 EndY=48 EndZ=0
    g1: LineSegment [constr] StartX=1.07e-14 StartY=48 StartZ=0 EndX=0 EndY=43.5155 EndZ=0
    g2: ArcOfCircle CenterX=9e-15 CenterY=52.42 CenterZ=0 NormalX=0 NormalY=0 NormalZ=1 AngleXU=0 Radius=8.90445 StartAngle=3.66102 EndAngle=5.76376
    g3: Circle [constr] CenterX=9e-15 CenterY=52.42 CenterZ=0 NormalX=0 NormalY=0 NormalZ=1 AngleXU=0 Radius=8.9
  constraints (13):
    c: Horizontal(g0)
    c: DistanceY(g-3,g0) = 0
    c: DistanceX(g0,g0) = 15.46
    c: DistanceX(g0,g-3) = 7.73
    c: DistanceX(g-3) = 0
    c: Coincident(g1,g-3)
    c: PointOnObject(g1,g-2)
    c: Coincident(g2,g0)
    c: Coincident(g2,g0)
    c: PointOnObject(g1,g2)
    c: Diameter(g3) = 17.8
    c: DistanceY(g1,g3) = 4.42
    c: Coincident(g2,g3)
FEATURE [Part::Extrusion] Extrude014  label="Extrude Scavo CAM"
  Base = -> Sketch018
  Dir = (1,0,0)
  DirMode = 2
  FaceMakerClass = Part::FaceMakerBullseye
  FaceMakerMode = 3
  LengthFwd = -34
  LengthRev = 0
  Solid = true
  Symmetric = false
FEATURE [Sketcher::SketchObject] Sketch019  label="scavo rumble"
  ArcFitTolerance = 1e-06
  AttachmentSupport = -> [XZ_Plane]
  ExternalGeometry = -> [Sketch]
  FullyConstrained = true
  MakeInternals = false
  MapMode = 5
  Placement = pos=(0,0,0) rot=(1,0,0;1.5708rad)
  sketch-geometry (6):
    g0: LineSegment StartX=-164.266 StartY=-23.4275 StartZ=0 EndX=-159.13 EndY=-25.0962 EndZ=0
    g1: LineSegment StartX=-159.13 StartY=-25.0962 StartZ=0 EndX=-166.238 EndY=-46.9705 EndZ=0
    g2: LineSegment StartX=-166.238 StartY=-46.9705 StartZ=0 EndX=-171.373 EndY=-45.3018 EndZ=0
    g3: LineSegment StartX=-171.373 StartY=-45.3018 StartZ=0 EndX=-164.266 EndY=-23.4275 EndZ=0
    g4: LineSegment [constr] StartX=-145.51 StartY=22 StartZ=0 EndX=-160.652 EndY=-24.6018 EndZ=0
    g5: LineSegment [constr] StartX=-159.13 StartY=-25.0962 StartZ=0 EndX=-160.652 EndY=-24.6018 EndZ=0
  constraints (17):
    c: Coincident(g1,g0)
    c: Coincident(g2,g1)
    c: Coincident(g3,g2)
    c: Coincident(g3,g0)
    c: Parallel(g3,g-3)
    c: Parallel(g3,g1)
    c: Perpendicular(g3,g0)
    c: Perpendicular(g2,g3)
    c: Distance(g2,g0) = 23
    c: Parallel(g4,g-3)
    c: Distance(g4) = 49
    c: Coincident(g4,g-3)
    c: Parallel(g5,g0)
    c: Distance(g5) = 1.6
    c: Coincident(g5,g0)
    c: Distance(g5,g0) = 3.8
    c: Coincident(g5,g4)
FEATURE [Part::Extrusion] Extrude015  label="scavo rumble001"
  Base = -> Sketch019
  Dir = (0,-1,2e-16)
  DirMode = 2
  FaceMakerClass = Part::FaceMakerBullseye
  FaceMakerMode = 3
  LengthFwd = 21
  LengthRev = 0
  Solid = true
  Symmetric = true
FEATURE [Sketcher::SketchObject] Sketch020  label="fermo rumble"
  ArcFitTolerance = 1e-06
  AttachmentSupport = -> [XZ_Plane]
  ExternalGeometry = -> [Sketch019,Sketch]
  FullyConstrained = true
  MakeInternals = false
  MapMode = 5
  Placement = pos=(0,0,0) rot=(1,0,0;1.5708rad)
  sketch-geometry (16):
    g0: LineSegment [constr] StartX=-166.4 StartY=-42.2914 StartZ=0 EndX=-167.759 EndY=-46.4761 EndZ=0
    g1: LineSegment [constr] StartX=-167.759 StartY=-46.4761 StartZ=0 EndX=-166.238 EndY=-46.9705 EndZ=0
    g2: LineSegment StartX=-167.812 StartY=-39.5193 StartZ=0 EndX=-165.72 EndY=-40.1991 EndZ=0
    g3: LineSegment StartX=-165.72 StartY=-40.1991 StartZ=0 EndX=-166.4 EndY=-42.2914 EndZ=0
    g4: LineSegment StartX=-166.4 StartY=-42.2914 StartZ=0 EndX=-168.492 EndY=-41.6116 EndZ=0
    g5: LineSegment StartX=-168.492 StartY=-41.6116 StartZ=0 EndX=-167.812 EndY=-39.5193 EndZ=0
    g6: LineSegment StartX=-167.318 StartY=-37.9976 StartZ=0 EndX=-163.894 EndY=-39.11 EndZ=0
    g7: LineSegment StartX=-163.894 StartY=-39.11 StartZ=0 EndX=-165.501 EndY=-44.0555 EndZ=0
    g8: LineSegment StartX=-165.501 StartY=-44.0555 StartZ=0 EndX=-168.924 EndY=-42.9431 EndZ=0
    g9: LineSegment StartX=-169.952 StartY=-40.9269 StartZ=0 EndX=-169.334 EndY=-39.0248 EndZ=0
    g10: LineSegment [constr] StartX=-169.334 StartY=-39.0248 StartZ=0 EndX=-168.839 EndY=-37.5031 EndZ=0
    g11: LineSegment [constr] StartX=-168.839 StartY=-37.5031 StartZ=0 EndX=-167.318 EndY=-37.9976 EndZ=0
    g12: ArcOfCircle CenterX=-168.43 CenterY=-41.4214 CenterZ=0 NormalX=0 NormalY=0 NormalZ=1 AngleXU=0 Radius=1.6 StartAngle=2.82743 EndAngle=4.39823
    g13: GeomPoint [constr] X=-170.446 Y=-42.4486 Z=0
    g14: ArcOfCircle CenterX=-167.812 CenterY=-39.5193 CenterZ=0 NormalX=0 NormalY=0 NormalZ=1 AngleXU=0 Radius=1.6 StartAngle=1.25664 EndAngle=2.82743
    g15: GeomPoint [constr] X=-168.839 Y=-37.5031 Z=0
  constraints (42):
    c: Parallel(g0,g-4)
    c: Distance(g0) = 4.4
    c: Coincident(g1,g0)
    c: Perpendicular(g0,g1)
    c: Distance(g1) = 1.6
    c: Coincident(g1,g-5)
    c: Coincident(g3,g2)
    c: Coincident(g4,g3)
    c: Coincident(g5,g4)
    c: Coincident(g5,g2)
    c: Parallel(g3,g-4)
    c: Parallel(g3,g5)
    c: Perpendicular(g2,g3)
    c: Parallel(g4,g2)
    c: Distance(g2) = 2.2
    c: Distance(g3) = 2.2
    c: Coincident(g7,g6)
    c: Coincident(g8,g7)
    c: Parallel(g7,g-4)
    c: Parallel(g7,g9)
    c: Perpendicular(g6,g7)
    c: Parallel(g6,g8)
    c: Distance(g6,g15) = 5.2
    c: Distance(g7) = 5.2
    c: Coincident(g11,g10)
    c: Parallel(g10,g9)
    c: Parallel(g11,g6)
    c: Distance(g10) = 1.6
    c: Distance(g11) = 1.6
    c: Coincident(g10,g15)
    c: Distance(g11,g2) = 1.6
    c: Distance(g2,g10) = 1.6
    c: PointOnObject(g13,g8)
    c: PointOnObject(g13,g9)
    c: Tangent(g8,g12) = 1.5708
    c: Tangent(g9,g12) = 1.5708
    c: PointOnObject(g15,g9)
    c: Tangent(g6,g14) = 1.5708
    c: Tangent(g9,g14) = 1.5708
    c: Equal(g12,g14)
    c: Coincident(g6,g11)
    c: Coincident(g3,g0)
FEATURE [Part::Extrusion] Extrude016  label="Extrude fermo rumble"
  Base = -> Sketch020
  Dir = (0,-1,2e-16)
  DirMode = 2
  FaceMakerClass = Part::FaceMakerBullseye
  FaceMakerMode = 3
  LengthFwd = 25.2
  LengthRev = 0
  Solid = true
  Symmetric = true
FEATURE [Sketcher::SketchObject] Sketch021  label="perno fermo rumble001"
  ArcFitTolerance = 1e-06
  AttachmentSupport = -> [XZ_Plane001]
  FullyConstrained = true
  MakeInternals = false
  MapMode = 5
  Placement = pos=(0,0,0) rot=(1,0,0;1.5708rad)
  sketch-geometry (16):
    g0: LineSegment StartX=0 StartY=0.45 StartZ=0 EndX=0 EndY=1.55 EndZ=0
    g1: LineSegment StartX=0.45 StartY=2 StartZ=0 EndX=1.55 EndY=2 EndZ=0
    g2: LineSegment StartX=2 StartY=1.55 StartZ=0 EndX=2 EndY=0.45 EndZ=0
    g3: LineSegment StartX=1.55 StartY=0 StartZ=0 EndX=0.45 EndY=0 EndZ=0
    g4: ArcOfCircle [constr] CenterX=0.45 CenterY=1.55 CenterZ=0 NormalX=0 NormalY=0 NormalZ=1 AngleXU=0 Radius=0.45 StartAngle=1.5708 EndAngle=3.14159
    g5: GeomPoint [constr] X=0 Y=2 Z=0
    g6: LineSegment StartX=0.45 StartY=2 StartZ=0 EndX=0 EndY=1.55 EndZ=0
    g7: ArcOfCircle [constr] CenterX=1.55 CenterY=1.55 CenterZ=0 NormalX=0 NormalY=0 NormalZ=1 AngleXU=0 Radius=0.45 StartAngle=0 EndAngle=1.5708
    g8: GeomPoint [constr] X=2 Y=2 Z=0
    g9: LineSegment StartX=2 StartY=1.55 StartZ=0 EndX=1.55 EndY=2 EndZ=0
    g10: ArcOfCircle [constr] CenterX=1.55 CenterY=0.45 CenterZ=0 NormalX=0 NormalY=0 NormalZ=1 AngleXU=0 Radius=0.45 StartAngle=4.71239 EndAngle=6.28319
    g11: GeomPoint [constr] X=2 Y=0 Z=0
    g12: LineSegment StartX=1.55 StartY=0 StartZ=0 EndX=2 EndY=0.45 EndZ=0
    g13: ArcOfCircle [constr] CenterX=0.45 CenterY=0.45 CenterZ=0 NormalX=0 NormalY=0 NormalZ=1 AngleXU=0 Radius=0.45 StartAngle=3.14159 EndAngle=4.71239
    g14: GeomPoint [constr] X=0 Y=0 Z=0
    g15: LineSegment StartX=0 StartY=0.45 StartZ=0 EndX=0.45 EndY=0 EndZ=0
  constraints (35):
    c: Coincident(g14,g-1)
    c: PointOnObject(g5,g-2)
    c: Horizontal(g1)
    c: Vertical(g2)
    c: Horizontal(g3)
    c: DistanceX(g5,g8) = 2
    c: DistanceY(g11,g8) = 2
    c: PointOnObject(g5,g0)
    c: PointOnObject(g5,g1)
    c: Tangent(g0,g4) = 1.5708
    c: Tangent(g1,g4) = 1.5708
    c: Coincident(g6,g0)
    c: Coincident(g6,g1)
    c: PointOnObject(g8,g2)
    c: PointOnObject(g8,g1)
    c: Tangent(g2,g7) = 1.5708
    c: Tangent(g1,g7) = 1.5708
    c: Coincident(g9,g2)
    c: Coincident(g9,g1)
    c: PointOnObject(g11,g2)
    c: PointOnObject(g11,g3)
    c: Tangent(g2,g10) = 1.5708
    c: Tangent(g3,g10) = 1.5708
    c: Coincident(g12,g2)
    c: Coincident(g12,g3)
    c: PointOnObject(g14,g0)
    c: PointOnObject(g14,g3)
    c: Tangent(g0,g13) = 1.5708
    c: Tangent(g3,g13) = 1.5708
    c: Coincident(g15,g0)
    c: Coincident(g15,g3)
    c: Equal(g6,g9)
    c: Equal(g9,g12)
    c: Equal(g12,g15)
    c: DistanceX(g14,g3) = 0.45
FEATURE [Sketcher::SketchObject] Sketch022  label="fori per M3x5(OD)x6(L)"
  ArcFitTolerance = 1e-06
  AttachmentSupport = -> [XZ_Plane]
  ExternalGeometry = -> [Sketch016]
  FullyConstrained = true
  MakeInternals = false
  MapMode = 5
  Placement = pos=(0,0,0) rot=(1,0,0;1.5708rad)
  sketch-geometry (7):
    g0: Circle CenterX=-5.6 CenterY=34.8 CenterZ=0 NormalX=0 NormalY=0 NormalZ=1 AngleXU=0 Radius=2.5
    g1: Circle CenterX=-5.6 CenterY=7.6 CenterZ=0 NormalX=0 NormalY=0 NormalZ=1 AngleXU=0 Radius=2.5
    g2: Circle CenterX=-78.51 CenterY=34.8 CenterZ=0 NormalX=0 NormalY=0 NormalZ=1 AngleXU=0 Radius=2.5
    g3: Circle CenterX=-78.51 CenterY=7.6 CenterZ=0 NormalX=0 NormalY=0 NormalZ=1 AngleXU=0 Radius=2.5
    g4: Circle CenterX=-184.08 CenterY=34.8 CenterZ=0 NormalX=0 NormalY=0 NormalZ=1 AngleXU=0 Radius=2.5
    g5: Circle CenterX=-179.305 CenterY=-76.8316 CenterZ=0 NormalX=0 NormalY=0 NormalZ=1 AngleXU=0 Radius=2.5
    g6: Circle CenterX=-213.443 CenterY=-76.8316 CenterZ=0 NormalX=0 NormalY=0 NormalZ=1 AngleXU=0 Radius=2.5
  constraints (14):
    c: Diameter(g0) = 5
    c: Diameter(g1) = 5
    c: Diameter(g2) = 5
    c: Diameter(g3) = 5
    c: Diameter(g4) = 5
    c: Diameter(g5) = 5
    c: Diameter(g6) = 5
    c: Coincident(g0,g-8)
    c: Coincident(g1,g-9)
    c: Coincident(g2,g-6)
    c: Coincident(g3,g-7)
    c: Coincident(g4,g-5)
    c: Coincident(g5,g-4)
    c: Coincident(g6,g-3)
FEATURE [Part::Extrusion] Extrude018  label="Extrude fori M3x5x6 - dx"
  Base = -> Sketch022
  Dir = (0,-1,2e-16)
  DirMode = 2
  FaceMakerClass = Part::FaceMakerBullseye
  FaceMakerMode = 3
  LengthFwd = 6.2
  LengthRev = 0
  Placement = pos=(0,-9.5,0) rot=(0,0,1;0rad)
  Solid = true
  Symmetric = true
FEATURE [Part::Extrusion] Extrude019  label="Extrude fori M3x5x6 - sx"
  Base = -> Sketch022
  Dir = (0,-1,2e-16)
  DirMode = 2
  FaceMakerClass = Part::FaceMakerBullseye
  FaceMakerMode = 3
  LengthFwd = 6.2
  LengthRev = 0
  Placement = pos=(0,9.5,0) rot=(0,0,1;0rad)
  Solid = true
  Symmetric = true
FEATURE [Sketcher::SketchObject] Sketch023  label="foro anteriore M3x5x6"
  ArcFitTolerance = 1e-06
  AttachmentSupport = -> [YZ_Plane]
  FullyConstrained = true
  MakeInternals = false
  MapMode = 5
  Placement = pos=(0,0,0) rot=(0.57735,0.57735,0.57735;2.0944rad)
  sketch-geometry (2):
    g0: LineSegment [constr] StartX=0 StartY=0 StartZ=0 EndX=0 EndY=38.6 EndZ=0
    g1: Circle CenterX=0 CenterY=38.6 CenterZ=0 NormalX=0 NormalY=0 NormalZ=1 AngleXU=0 Radius=2.5
  constraints (5):
    c: Coincident(g0,g-1)
    c: PointOnObject(g0,g-2)
    c: DistanceY(g0,g0) = 38.6
    c: Diameter(g1) = 5
    c: Coincident(g1,g0)
FEATURE [Part::Extrusion] Extrude020  label="Extrude foro anteriore M3x5x6"
  Base = -> Sketch023
  Dir = (1,0,0)
  DirMode = 2
  FaceMakerClass = Part::FaceMakerBullseye
  FaceMakerMode = 3
  LengthFwd = -6.2
  LengthRev = 0
  Solid = true
  Symmetric = false
FEATURE [Sketcher::SketchObject] Sketch024  label="fori per viti frontale"
  ArcFitTolerance = 1e-06
  AttachmentSupport = -> [YZ_Plane]
  FullyConstrained = true
  MakeInternals = false
  MapMode = 5
  Placement = pos=(0,0,0) rot=(0.57735,0.57735,0.57735;2.0944rad)
  sketch-geometry (9):
    g0: LineSegment [constr] StartX=-10.3 StartY=30.721 StartZ=0 EndX=10.3 EndY=30.721 EndZ=0
    g1: LineSegment [constr] StartX=10.3 StartY=30.721 StartZ=0 EndX=10.3 EndY=10.121 EndZ=0
    g2: LineSegment [constr] StartX=10.3 StartY=10.121 StartZ=0 EndX=-10.3 EndY=10.121 EndZ=0
    g3: LineSegment [constr] StartX=-10.3 StartY=10.121 StartZ=0 EndX=-10.3 EndY=30.721 EndZ=0
    g4: LineSegment [constr] StartX=0 StartY=0 StartZ=0 EndX=0 EndY=10.121 EndZ=0
    g5: Circle CenterX=-10.3 CenterY=30.721 CenterZ=0 NormalX=0 NormalY=0 NormalZ=1 AngleXU=0 Radius=2
    g6: Circle CenterX=10.3 CenterY=30.721 CenterZ=0 NormalX=0 NormalY=0 NormalZ=1 AngleXU=0 Radius=2
    g7: Circle CenterX=-10.3 CenterY=10.121 CenterZ=0 NormalX=0 NormalY=0 NormalZ=1 AngleXU=0 Radius=2
    g8: Circle CenterX=10.3 CenterY=10.121 CenterZ=0 NormalX=0 NormalY=0 NormalZ=1 AngleXU=0 Radius=2
  constraints (22):
    c: Horizontal(g0)
    c: Coincident(g1,g0)
    c: Vertical(g1)
    c: Coincident(g2,g1)
    c: Horizontal(g2)
    c: Coincident(g3,g2)
    c: Coincident(g3,g0)
    c: Vertical(g3)
    c: DistanceX(g0,g0) = 20.6
    c: DistanceY(g3,g3) = 20.6
    c: Coincident(g4,g-1)
    c: PointOnObject(g4,g-2)
    c: DistanceY(g4,g4) = 10.121
    c: Symmetric(g2,g2,g4)
    c: Diameter(g5) = 4
    c: Diameter(g6) = 4
    c: Diameter(g7) = 4
    c: Diameter(g8) = 4
    c: Coincident(g5,g0)
    c: Coincident(g6,g0)
    c: Coincident(g7,g2)
    c: Coincident(g8,g1)
FEATURE [Part::Extrusion] Extrude021  label="Extrude fori per viti frontale"
  Base = -> Sketch024
  Dir = (1,0,0)
  DirMode = 2
  FaceMakerClass = Part::FaceMakerBullseye
  FaceMakerMode = 3
  LengthFwd = -2.4
  LengthRev = 0
  Solid = true
  Symmetric = false
FEATURE [Sketcher::SketchObject] Sketch025  label="foro per filo CAM"
  ArcFitTolerance = 1e-06
  AttachmentSupport = -> [XZ_Plane]
  ExternalGeometry = -> [Sketch]
  FullyConstrained = true
  MakeInternals = false
  MapMode = 5
  Placement = pos=(0,0,0) rot=(1,0,0;1.5708rad)
  sketch-geometry (4):
    g0: LineSegment StartX=-44.6 StartY=41.2 StartZ=0 EndX=-44.6 EndY=36.4 EndZ=0
    g1: LineSegment StartX=-44.6 StartY=36.4 StartZ=0 EndX=-54.6 EndY=36.4 EndZ=0
    g2: LineSegment StartX=-54.6 StartY=36.4 StartZ=0 EndX=-50.4 EndY=41.2 EndZ=0
    g3: LineSegment StartX=-50.4 StartY=41.2 StartZ=0 EndX=-44.6 EndY=41.2 EndZ=0
  constraints (11):
    c: Vertical(g0)
    c: Coincident(g1,g0)
    c: Horizontal(g1)
    c: Coincident(g2,g1)
    c: Coincident(g3,g2)
    c: Coincident(g3,g0)
    c: Horizontal(g3)
    c: Coincident(g0,g-3)
    c: DistanceY(g0,g-4) = 0
    c: DistanceX(g3,g3) = 5.8
    c: DistanceX(g1,g1) = 10
FEATURE [Part::Extrusion] Extrude022  label="Extrude foro per filo CAM dx"
  Base = -> Sketch025
  Dir = (0,-1,2e-16)
  DirMode = 2
  FaceMakerClass = Part::FaceMakerBullseye
  FaceMakerMode = 3
  LengthFwd = 4.9
  LengthRev = 0
  Placement = pos=(0,6.95,0) rot=(0,0,1;0rad)
  Solid = true
  Symmetric = true
FEATURE [Part::Extrusion] Extrude023  label="Extrude foro per filo CAM sx"
  Base = -> Sketch025
  Dir = (0,-1,2e-16)
  DirMode = 2
  FaceMakerClass = Part::FaceMakerBullseye
  FaceMakerMode = 3
  LengthFwd = 4.9
  LengthRev = 0
  Placement = pos=(0,-6.95,0) rot=(0,0,1;0rad)
  Solid = true
  Symmetric = true
FEATURE [Sketcher::SketchObject] Sketch026  label="foro sotto anteriore M3x5x6"
  ArcFitTolerance = 1e-06
  AttachmentSupport = -> [XY_Plane]
  FullyConstrained = true
  MakeInternals = false
  MapMode = 5
  sketch-geometry (2):
    g0: LineSegment [constr] StartX=0 StartY=0 StartZ=0 EndX=-16.5 EndY=0 EndZ=0
    g1: Circle CenterX=-16.5 CenterY=0 CenterZ=0 NormalX=0 NormalY=0 NormalZ=1 AngleXU=0 Radius=2.5
  constraints (5):
    c: Distance(g0) = 16.5
    c: Coincident(g0,g-1)
    c: PointOnObject(g0,g-1)
    c: Diameter(g1) = 5
    c: Coincident(g0,g1)
FEATURE [Sketcher::SketchObject] Sketch027  label="foro sotto posteriore M3x5x6"
  ArcFitTolerance = 1e-06
  AttachmentSupport = -> [XY_Plane]
  ExternalGeometry = -> [Sketch]
  FullyConstrained = true
  MakeInternals = false
  MapMode = 5
  sketch-geometry (2):
    g0: LineSegment [constr] StartX=-82.8 StartY=2e-16 StartZ=0 EndX=-71.3 EndY=2e-16 EndZ=0
    g1: Circle CenterX=-71.3 CenterY=2e-16 CenterZ=0 NormalX=0 NormalY=0 NormalZ=1 AngleXU=0 Radius=2.5
  constraints (5):
    c: Distance(g0) = 11.5
    c: Coincident(g0,g-3)
    c: PointOnObject(g0,g-3)
    c: Diameter(g1) = 5
    c: Coincident(g1,g0)
FEATURE [Sketcher::SketchObject] Sketch029  label="fori sotto impugnatura"
  ArcFitTolerance = 1e-06
  AttachmentSupport = -> [XY_Plane]
  ExternalGeometry = -> [Sketch]
  FullyConstrained = true
  MakeInternals = false
  MapMode = 5
  sketch-geometry (15):
    g0: LineSegment [constr] StartX=-175.232 StartY=-1.83e-14 StartZ=0 EndX=-191.232 EndY=0 EndZ=0
    g1: Circle CenterX=-191.232 CenterY=0 CenterZ=0 NormalX=0 NormalY=0 NormalZ=1 AngleXU=0 Radius=3.95
    g2: LineSegment [constr] StartX=-175.232 StartY=-1.83e-14 StartZ=0 EndX=-204.275 EndY=0 EndZ=0
    g3: LineSegment StartX=-204.275 StartY=3.525 StartZ=0 EndX=-204.275 EndY=-3.525 EndZ=0
    g4: LineSegment StartX=-205.4 StartY=-4.65 StartZ=0 EndX=-206.65 EndY=-4.65 EndZ=0
    g5: LineSegment StartX=-207.775 StartY=-3.525 StartZ=0 EndX=-207.775 EndY=3.525 EndZ=0
    g6: LineSegment StartX=-206.65 StartY=4.65 StartZ=0 EndX=-205.4 EndY=4.65 EndZ=0
    g7: ArcOfCircle CenterX=-206.65 CenterY=3.525 CenterZ=0 NormalX=0 NormalY=0 NormalZ=1 AngleXU=0 Radius=1.125 StartAngle=1.5708 EndAngle=3.14159
    g8: GeomPoint [constr] X=-207.775 Y=4.65 Z=0
    g9: ArcOfCircle CenterX=-205.4 CenterY=3.525 CenterZ=0 NormalX=0 NormalY=0 NormalZ=1 AngleXU=0 Radius=1.125 StartAngle=0 EndAngle=1.5708
    g10: GeomPoint [constr] X=-204.275 Y=4.65 Z=0
    g11: ArcOfCircle CenterX=-205.4 CenterY=-3.525 CenterZ=0 NormalX=0 NormalY=0 NormalZ=1 AngleXU=0 Radius=1.125 StartAngle=4.71239 EndAngle=6.28319
    g12: GeomPoint [constr] X=-204.275 Y=-4.65 Z=0
    g13: ArcOfCircle CenterX=-206.65 CenterY=-3.525 CenterZ=0 NormalX=0 NormalY=0 NormalZ=1 AngleXU=0 Radius=1.125 StartAngle=3.14159 EndAngle=4.71239
    g14: GeomPoint [constr] X=-207.775 Y=-4.65 Z=0
  constraints (35):
    c: Distance(g0) = 16
    c: Coincident(g0,g-3)
    c: PointOnObject(g0,g-1)
    c: Diameter(g1) = 7.9
    c: Coincident(g1,g0)
    c: Coincident(g2,g0)
    c: PointOnObject(g2,g-1)
    c: Vertical(g3)
    c: Horizontal(g4)
    c: Vertical(g5)
    c: Horizontal(g6)
    c: DistanceY(g12,g10) = 9.3
    c: DistanceX(g8,g10) = 3.5
    c: Symmetric(g10,g12,g2)
    c: PointOnObject(g8,g5)
    c: PointOnObject(g8,g6)
    c: Tangent(g5,g7) = 1.5708
    c: Tangent(g6,g7) = 1.5708
    c: PointOnObject(g10,g3)
    c: PointOnObject(g10,g6)
    c: Tangent(g3,g9) = 1.5708
    c: Tangent(g6,g9) = 1.5708
    c: PointOnObject(g12,g3)
    c: PointOnObject(g12,g4)
    c: Tangent(g3,g11) = 1.5708
    c: Tangent(g4,g11) = 1.5708
    c: PointOnObject(g14,g4)
    c: PointOnObject(g14,g5)
    c: Tangent(g4,g13) = 1.5708
    c: Tangent(g5,g13) = 1.5708
    c: Equal(g7,g9)
    c: Equal(g9,g11)
    c: Equal(g11,g13)
    c: DistanceX(g6,g6) = 1.25
    c: DistanceX(g-5,g5) = 6.8
FEATURE [Sketcher::SketchObject] Sketch030  label="fori superiori per solenoide e oled"
  ArcFitTolerance = 1e-06
  AttachmentSupport = -> [XY_Plane]
  ExternalGeometry = -> [Sketch]
  FullyConstrained = true
  MakeInternals = false
  MapMode = 5
  sketch-geometry (33):
    g0: LineSegment [constr] StartX=-181.6 StartY=1.12e-14 StartZ=0 EndX=-169.91 EndY=0 EndZ=0
    g1: LineSegment [constr] StartX=-169.91 StartY=0 StartZ=0 EndX=-169.91 EndY=-2.6 EndZ=0
    g2: LineSegment [constr] StartX=-169.91 StartY=0 StartZ=0 EndX=-169.91 EndY=2.6 EndZ=0
    g3: LineSegment StartX=-169.91 StartY=4.975 StartZ=0 EndX=-169.91 EndY=8.225 EndZ=0
    g4: LineSegment StartX=-167.535 StartY=10.6 StartZ=0 EndX=-167.285 EndY=10.6 EndZ=0
    g5: LineSegment StartX=-164.91 StartY=8.225 StartZ=0 EndX=-164.91 EndY=4.975 EndZ=0
    g6: LineSegment StartX=-167.285 StartY=2.6 StartZ=0 EndX=-167.535 EndY=2.6 EndZ=0
    g7: LineSegment StartX=-169.91 StartY=-4.975 StartZ=0 EndX=-169.91 EndY=-8.225 EndZ=0
    g8: LineSegment StartX=-167.535 StartY=-10.6 StartZ=0 EndX=-167.285 EndY=-10.6 EndZ=0
    g9: LineSegment StartX=-164.91 StartY=-8.225 StartZ=0 EndX=-164.91 EndY=-4.975 EndZ=0
    g10: LineSegment StartX=-167.285 StartY=-2.6 StartZ=0 EndX=-167.535 EndY=-2.6 EndZ=0
    g11: ArcOfCircle CenterX=-167.535 CenterY=8.225 CenterZ=0 NormalX=0 NormalY=0 NormalZ=1 AngleXU=0 Radius=2.375 StartAngle=1.5708 EndAngle=3.14159
    g12: GeomPoint [constr] X=-169.91 Y=10.6 Z=0
    g13: ArcOfCircle CenterX=-167.285 CenterY=8.225 CenterZ=0 NormalX=0 NormalY=0 NormalZ=1 AngleXU=0 Radius=2.375 StartAngle=0 EndAngle=1.5708
    g14: GeomPoint [constr] X=-164.91 Y=10.6 Z=0
    g15: ArcOfCircle CenterX=-167.285 CenterY=4.975 CenterZ=0 NormalX=0 NormalY=0 NormalZ=1 AngleXU=0 Radius=2.375 StartAngle=4.71239 EndAngle=6.28319
    g16: GeomPoint [constr] X=-164.91 Y=2.6 Z=0
    g17: ArcOfCircle CenterX=-167.535 CenterY=4.975 CenterZ=0 NormalX=0 NormalY=0 NormalZ=1 AngleXU=0 Radius=2.375 StartAngle=3.14159 EndAngle=4.71239
    g18: GeomPoint [constr] X=-169.91 Y=2.6 Z=0
    g19: ArcOfCircle CenterX=-167.535 CenterY=-4.975 CenterZ=0 NormalX=0 NormalY=0 NormalZ=1 AngleXU=0 Radius=2.375 StartAngle=1.5708 EndAngle=3.14159
    g20: GeomPoint [constr] X=-169.91 Y=-2.6 Z=0
    g21: ArcOfCircle CenterX=-167.285 CenterY=-4.975 CenterZ=0 NormalX=0 NormalY=0 NormalZ=1 AngleXU=0 Radius=2.375 StartAngle=0 EndAngle=1.5708
    g22: GeomPoint [constr] X=-164.91 Y=-2.6 Z=0
    g23: ArcOfCircle CenterX=-167.285 CenterY=-8.225 CenterZ=0 NormalX=0 NormalY=0 NormalZ=1 AngleXU=0 Radius=2.375 StartAngle=4.71239 EndAngle=6.28319
    g24: GeomPoint [constr] X=-164.91 Y=-10.6 Z=0
    g25: ArcOfCircle CenterX=-167.535 CenterY=-8.225 CenterZ=0 NormalX=0 NormalY=0 NormalZ=1 AngleXU=0 Radius=2.375 StartAngle=3.14159 EndAngle=4.71239
    g26: GeomPoint [constr] X=-169.91 Y=-10.6 Z=0
    g27: LineSegment [constr] StartX=-181.6 StartY=1.12e-14 StartZ=0 EndX=-152.209 EndY=0 EndZ=0
    g28: LineSegment [constr] StartX=-181.6 StartY=1.12e-14 StartZ=0 EndX=-130.41 EndY=0 EndZ=0
    g29: LineSegment [constr] StartX=-152.209 StartY=0 StartZ=0 EndX=-152.209 EndY=6.95 EndZ=0
    g30: LineSegment [constr] StartX=-130.41 StartY=0 StartZ=0 EndX=-130.41 EndY=-6.95 EndZ=0
    g31: Circle CenterX=-152.209 CenterY=6.95 CenterZ=0 NormalX=0 NormalY=0 NormalZ=1 AngleXU=0 Radius=2.1
    g32: Circle CenterX=-130.41 CenterY=-6.95 CenterZ=0 NormalX=0 NormalY=0 NormalZ=1 AngleXU=0 Radius=2.1
  constraints (79):
    c: Distance(g0) = 11.69
    c: PointOnObject(g0,g-1)
    c: Coincident(g-4,g0)
    c: Distance(g1) = 2.6
    c: Coincident(g1,g0)
    c: Vertical(g1)
    c: Distance(g2) = 2.6
    c: Coincident(g2,g0)
    c: Vertical(g2)
    c: Distance(g18,g12) = 8
    c: Coincident(g18,g2)
    c: Vertical(g3)
    c: Distance(g14,g12) = 5
    c: Horizontal(g4)
    c: Distance(g16,g14) = 8
    c: Vertical(g5)
    c: Distance(g26,g20) = 8
    c: Coincident(g20,g1)
    c: Vertical(g7)
    c: Distance(g26,g24) = 5
    c: Horizontal(g8)
    c: Distance(g24,g22) = 8
    c: Vertical(g9)
    c: PointOnObject(g12,g3)
    c: PointOnObject(g12,g4)
    c: Tangent(g3,g11) = 1.5708
    c: Tangent(g4,g11) = 1.5708
    c: PointOnObject(g14,g5)
    c: PointOnObject(g14,g4)
    c: Tangent(g5,g13) = 1.5708
    c: Tangent(g4,g13) = 1.5708
    c: PointOnObject(g16,g5)
    c: PointOnObject(g16,g6)
    c: Tangent(g5,g15) = 1.5708
    c: Tangent(g6,g15) = 1.5708
    c: PointOnObject(g18,g3)
    c: PointOnObject(g18,g6)
    c: Tangent(g3,g17) = 1.5708
    c: Tangent(g6,g17) = 1.5708
    c: Equal(g11,g13)
    c: Equal(g13,g15)
    c: Equal(g15,g17)
    c: DistanceX(g4,g4) = 0.25
    c: PointOnObject(g20,g7)
    c: PointOnObject(g20,g10)
    c: Tangent(g7,g19) = -1.5708
    c: Tangent(g10,g19) = -1.5708
    c: PointOnObject(g22,g9)
    c: PointOnObject(g22,g10)
    c: Tangent(g9,g21) = -1.5708
    c: Tangent(g10,g21) = -1.5708
    c: PointOnObject(g24,g9)
    c: PointOnObject(g24,g8)
    c: Tangent(g9,g23) = -1.5708
    c: Tangent(g8,g23) = -1.5708
    c: PointOnObject(g26,g8)
    c: PointOnObject(g26,g7)
    c: Tangent(g8,g25) = -1.5708
    c: Tangent(g7,g25) = -1.5708
    c: Equal(g19,g21)
    c: Equal(g21,g23)
    c: Equal(g23,g25)
    c: DistanceX(g10,g10) = 0.25
    c: Distance(g27) = 29.391
    c: Coincident(g27,g0)
    c: PointOnObject(g27,g-1)
    c: Distance(g28) = 51.19
    c: Coincident(g28,g0)
    c: PointOnObject(g28,g-1)
    c: Distance(g29) = 6.95
    c: Coincident(g29,g27)
    c: Vertical(g29)
    c: Distance(g30) = 6.95
    c: Coincident(g30,g28)
    c: Vertical(g30)
    c: Diameter(g31) = 4.2
    c: Diameter(g32) = 4.2
    c: Coincident(g32,g30)
    c: Coincident(g31,g29)
FEATURE [Sketcher::SketchObject] Sketch031  label="fori inferiori switch pompa"
  ArcFitTolerance = 1e-06
  AttachmentSupport = -> [XY_Plane]
  ExternalGeometry = -> [Sketch]
  FullyConstrained = true
  MakeInternals = false
  MapMode = 5
  sketch-geometry (4):
    g0: LineSegment [constr] StartX=-57.2 StartY=1.9e-15 StartZ=0 EndX=-62.45 EndY=1.9e-15 EndZ=0
    g1: LineSegment [constr] StartX=-62.45 StartY=3.25 StartZ=0 EndX=-62.45 EndY=-3.25 EndZ=0
    g2: Circle CenterX=-62.45 CenterY=3.25 CenterZ=0 NormalX=0 NormalY=0 NormalZ=1 AngleXU=0 Radius=1.6
    g3: Circle CenterX=-62.45 CenterY=-3.25 CenterZ=0 NormalX=0 NormalY=0 NormalZ=1 AngleXU=0 Radius=1.6
  constraints (10):
    c: Distance(g0) = 5.25
    c: Coincident(g0,g-3)
    c: PointOnObject(g0,g-3)
    c: Vertical(g1)
    c: DistanceY(g1,g1) = 6.5
    c: Symmetric(g1,g1,g0)
    c: Diameter(g2) = 3.2
    c: Diameter(g3) = 3.2
    c: Coincident(g2,g1)
    c: Coincident(g3,g1)
FEATURE [Sketcher::SketchObject] Sketch032  label="spazio per PILA 18650"
  ArcFitTolerance = 1e-06
  AttachmentSupport = -> [XY_Plane]
  ExternalGeometry = -> [Sketch]
  FullyConstrained = true
  MakeInternals = false
  MapMode = 5
  sketch-geometry (2):
    g0: LineSegment [constr] StartX=-178.142 StartY=-1.74e-14 StartZ=0 EndX=-191.142 EndY=-1.83e-14 EndZ=0
    g1: Circle CenterX=-191.142 CenterY=-1.83e-14 CenterZ=0 NormalX=0 NormalY=0 NormalZ=1 AngleXU=0 Radius=10.9
  constraints (5):
    c: Distance(g0) = 13
    c: Coincident(g0,g-3)
    c: PointOnObject(g0,g-4)
    c: Diameter(g1) = 21.8
    c: Coincident(g1,g0)
FEATURE [Part::Extrusion] Extrude030  label="Extrude spazio per PILA 18650"
  Base = -> Sketch032
  Dir = (0,0,1)
  DirLink = -> Sketch [Edge45]
  DirMode = 2
  FaceMakerClass = Part::FaceMakerBullseye
  FaceMakerMode = 3
  LengthFwd = 76
  LengthRev = 0
  Placement = pos=(6,0,-70) rot=(0,0,1;0rad)
  Solid = true
  Symmetric = false
FEATURE [Sketcher::SketchObject] Sketch033  label="fermo per scheda micro"
  ArcFitTolerance = 1e-06
  AttachmentSupport = -> [XZ_Plane]
  ExternalGeometry = -> [Sketch]
  FullyConstrained = true
  MakeInternals = false
  MapMode = 5
  Placement = pos=(0,0,0) rot=(1,0,0;1.5708rad)
  sketch-geometry (12):
    g0: LineSegment StartX=-11.6 StartY=6 StartZ=0 EndX=-4 EndY=6 EndZ=0
    g1: LineSegment StartX=-4 StartY=6 StartZ=0 EndX=-4 EndY=36.4 EndZ=0
    g2: LineSegment StartX=-4 StartY=36.4 StartZ=0 EndX=-11.6 EndY=36.4 EndZ=0
    g3: LineSegment StartX=-11.6 StartY=36.4 StartZ=0 EndX=-11.6 EndY=6 EndZ=0
    g4: LineSegment StartX=-80.11 StartY=11.6 StartZ=0 EndX=-70.51 EndY=11.6 EndZ=0
    g5: LineSegment StartX=-70.51 StartY=11.6 StartZ=0 EndX=-70.51 EndY=6 EndZ=0
    g6: LineSegment StartX=-70.51 StartY=6 StartZ=0 EndX=-80.11 EndY=6 EndZ=0
    g7: LineSegment StartX=-80.11 StartY=6 StartZ=0 EndX=-80.11 EndY=11.6 EndZ=0
    g8: LineSegment StartX=-78.51 StartY=36.4 StartZ=0 EndX=-70.51 EndY=36.4 EndZ=0
    g9: LineSegment StartX=-70.51 StartY=36.4 StartZ=0 EndX=-70.51 EndY=30.8 EndZ=0
    g10: LineSegment StartX=-70.51 StartY=30.8 StartZ=0 EndX=-78.51 EndY=30.8 EndZ=0
    g11: LineSegment StartX=-78.51 StartY=30.8 StartZ=0 EndX=-78.51 EndY=36.4 EndZ=0
  constraints (33):
    c: Horizontal(g0)
    c: Coincident(g1,g0)
    c: Coincident(g2,g1)
    c: Horizontal(g2)
    c: Coincident(g3,g2)
    c: Coincident(g3,g0)
    c: Vertical(g3)
    c: DistanceX(g2,g2) = 7.6
    c: Coincident(g1,g-3)
    c: Coincident(g0,g-3)
    c: Horizontal(g4)
    c: Coincident(g5,g4)
    c: Vertical(g5)
    c: Coincident(g6,g5)
    c: Horizontal(g6)
    c: Coincident(g7,g6)
    c: Coincident(g7,g4)
    c: Vertical(g7)
    c: DistanceY(g5,g5) = 5.6
    c: DistanceX(g4,g4) = 9.6
    c: Coincident(g9,g8)
    c: Vertical(g9)
    c: Coincident(g10,g9)
    c: Horizontal(g10)
    c: Coincident(g11,g10)
    c: Coincident(g11,g8)
    c: Vertical(g11)
    c: DistanceY(g9,g9) = 5.6
    c: DistanceX(g10,g10) = 8
    c: Coincident(g4,g-4)
    c: DistanceX(g4,g10) = 1.6
    c: Horizontal(g8)
    c: DistanceY(g8,g1) = 0
FEATURE [Sketcher::SketchObject] Sketch034  label="buchi guida rail"
  ArcFitTolerance = 1e-06
  AttachmentSupport = -> [XY_Plane]
  ExternalGeometry = -> [Sketch]
  FullyConstrained = true
  MakeInternals = false
  MapMode = 5
  sketch-geometry (6):
    g0: LineSegment [constr] StartX=-100.8 StartY=9.1e-15 StartZ=0 EndX=-93.3 EndY=0 EndZ=0
    g1: LineSegment [constr] StartX=-93.3 StartY=0 StartZ=0 EndX=-73.3 EndY=0 EndZ=0
    g2: LineSegment [constr] StartX=-73.3 StartY=0 StartZ=0 EndX=-53.3 EndY=0 EndZ=0
    g3: Circle CenterX=-93.3 CenterY=0 CenterZ=0 NormalX=0 NormalY=0 NormalZ=1 AngleXU=0 Radius=2.5
    g4: Circle CenterX=-73.3 CenterY=0 CenterZ=0 NormalX=0 NormalY=0 NormalZ=1 AngleXU=0 Radius=2.5
    g5: Circle CenterX=-53.3 CenterY=0 CenterZ=0 NormalX=0 NormalY=0 NormalZ=1 AngleXU=0 Radius=2.5
  constraints (15):
    c: Distance(g0) = 7.5
    c: Coincident(g0,g-3)
    c: PointOnObject(g0,g-1)
    c: Distance(g1) = 20
    c: Coincident(g1,g0)
    c: PointOnObject(g1,g-1)
    c: Distance(g2) = 20
    c: Coincident(g2,g1)
    c: PointOnObject(g2,g-1)
    c: Diameter(g3) = 5
    c: Diameter(g4) = 5
    c: Diameter(g5) = 5
    c: Coincident(g3,g0)
    c: Coincident(g4,g1)
    c: Coincident(g5,g2)
FEATURE [Part::Extrusion] Extrude032  label="Extrude buchi guida rail"
  Base = -> Sketch034
  Dir = (0,0,1)
  DirMode = 2
  FaceMakerClass = Part::FaceMakerBullseye
  FaceMakerMode = 3
  LengthFwd = -6.2
  LengthRev = 0
  Placement = pos=(0,0,43.2) rot=(0,0,1;0rad)
  Solid = true
  Symmetric = false
FEATURE [Part::Extrusion] Extrude033  label="Extrude fori superiori per solenoide e oled001"
  Base = -> Sketch030
  Dir = (0,0,1)
  DirMode = 2
  FaceMakerClass = Part::FaceMakerBullseye
  FaceMakerMode = 3
  LengthFwd = -4.8
  LengthRev = 0
  Placement = pos=(0,0,41.2) rot=(0,0,1;0rad)
  Solid = true
  Symmetric = false
FEATURE [Part::Extrusion] Extrude034  label="Extrude fori sotto impugnatura001"
  Base = -> Sketch029
  Dir = (0,0,1)
  DirMode = 2
  FaceMakerClass = Part::FaceMakerBullseye
  FaceMakerMode = 3
  LengthFwd = 5
  LengthRev = 0
  Placement = pos=(0,0,-83) rot=(0,0,1;0rad)
  Solid = true
  Symmetric = false
FEATURE [Part::Extrusion] Extrude035  label="Extrude fori inferiori switch pompa001"
  Base = -> Sketch031
  Dir = (0,0,1)
  DirMode = 2
  FaceMakerClass = Part::FaceMakerBullseye
  FaceMakerMode = 3
  LengthFwd = 4
  LengthRev = 0
  Placement = pos=(0,0,-1.7) rot=(0,0,1;0rad)
  Solid = true
  Symmetric = false
FEATURE [Part::Extrusion] Extrude036  label="Extrude foro sotto posteriore M3x5x007"
  Base = -> Sketch027
  Dir = (0,0,1)
  DirMode = 2
  FaceMakerClass = Part::FaceMakerBullseye
  FaceMakerMode = 3
  LengthFwd = 6.2
  LengthRev = 0
  Placement = pos=(0,0,-9.6) rot=(0,0,1;0rad)
  Solid = true
  Symmetric = false
FEATURE [Part::Extrusion] Extrude037  label="Extrude foro sotto anteriore M3x5x007"
  Base = -> Sketch026
  Dir = (0,0,1)
  DirMode = 2
  FaceMakerClass = Part::FaceMakerBullseye
  FaceMakerMode = 3
  LengthFwd = 6.2
  LengthRev = 0
  Solid = true
  Symmetric = false
FEATURE [Sketcher::SketchObject] Sketch035  label="foro per fissaggio micro"
  ArcFitTolerance = 1e-06
  AttachmentSupport = -> [XZ_Plane]
  ExternalGeometry = -> [Sketch,Sketch033]
  FullyConstrained = true
  MakeInternals = false
  MapMode = 5
  Placement = pos=(0,0,0) rot=(1,0,0;1.5708rad)
  sketch-geometry (3):
    g0: Circle CenterX=-7.8 CenterY=21.2 CenterZ=0 NormalX=0 NormalY=0 NormalZ=1 AngleXU=0 Radius=1.6
    g1: GeomPoint [constr] X=-4 Y=21.2 Z=0
    g2: LineSegment [constr] StartX=-4 StartY=21.2 StartZ=0 EndX=-11.6 EndY=21.2 EndZ=0
  constraints (6):
    c: Diameter(g0) = 3.2
    c: Symmetric(g-3,g-3,g1)
    c: Coincident(g2,g1)
    c: Horizontal(g2)
    c: DistanceX(g-4,g2) = 0
    c: Symmetric(g2,g1,g0)
FEATURE [Part::Extrusion] Extrude038  label="Extrude foro per fissaggio micro"
  Base = -> Sketch035
  Dir = (0,-1,2e-16)
  DirMode = 2
  FaceMakerClass = Part::FaceMakerBullseye
  FaceMakerMode = 3
  LengthFwd = 3
  LengthRev = 0
  Placement = pos=(0,8.6,0) rot=(0,0,1;0rad)
  Solid = true
  Symmetric = false
FEATURE [Sketcher::SketchObject] Sketch036  label="supporto per alimentatore"
  ArcFitTolerance = 1e-06
  AttachmentSupport = -> [XZ_Plane]
  ExternalGeometry = -> [Sketch,Sketch016,Sketch022]
  FullyConstrained = true
  MakeInternals = false
  MapMode = 5
  Placement = pos=(0,0,0) rot=(1,0,0;1.5708rad)
  sketch-geometry (5):
    g0: LineSegment StartX=-211.843 StartY=-50.0944 StartZ=0 EndX=-211.843 EndY=-80.4316 EndZ=0
    g1: LineSegment StartX=-211.843 StartY=-50.0944 StartZ=0 EndX=-207.775 EndY=-41.3701 EndZ=0
    g2: LineSegment [constr] StartX=-209.443 StartY=-50.0944 StartZ=0 EndX=-209.443 EndY=-80.4316 EndZ=0
    g3: LineSegment StartX=-207.775 StartY=-41.3701 StartZ=0 EndX=-207.775 EndY=-80.4316 EndZ=0
    g4: LineSegment StartX=-211.843 StartY=-80.4316 StartZ=0 EndX=-207.775 EndY=-80.4316 EndZ=0
  constraints (15):
    c: Vertical(g0)
    c: Coincident(g1,g0)
    c: Vertical(g2)
    c: Tangent(g2,g-5)
    c: Coincident(g3,g1)
    c: Vertical(g3)
    c: DistanceY(g-3,g3) = -2
    c: Tangent(g1,g-8)
    c: DistanceY(g-3,g0) = -2
    c: Coincident(g4,g0)
    c: Coincident(g4,g3)
    c: Tangent(g0,g-6)
    c: DistanceY(g-3,g2) = -2
    c: DistanceY(g2,g0) = 0
    c: DistanceX(g-3,g3) = 6.8
FEATURE [Part::Extrusion] Extrude039  label="Extrude039 supporto alimentatore"
  Base = -> Sketch036
  Dir = (0,-1,2e-16)
  DirMode = 2
  FaceMakerClass = Part::FaceMakerBullseye
  FaceMakerMode = 3
  LengthFwd = 25.2
  LengthRev = 0
  Solid = true
  Symmetric = true
FEATURE [Sketcher::SketchObject] Sketch037  label="scavo per alimentatore"
  ArcFitTolerance = 1e-06
  AttachmentSupport = -> [XZ_Plane]
  ExternalGeometry = -> [Sketch036]
  FullyConstrained = true
  MakeInternals = false
  MapMode = 5
  Placement = pos=(0,0,0) rot=(1,0,0;1.5708rad)
  sketch-geometry (4):
    g0: LineSegment StartX=-209.575 StartY=-50.4316 StartZ=0 EndX=-209.575 EndY=-80.4316 EndZ=0
    g1: LineSegment StartX=-209.575 StartY=-50.4316 StartZ=0 EndX=-207.775 EndY=-50.4316 EndZ=0
    g2: LineSegment StartX=-207.775 StartY=-50.4316 StartZ=0 EndX=-207.775 EndY=-80.4316 EndZ=0
    g3: LineSegment StartX=-207.775 StartY=-80.4316 StartZ=0 EndX=-209.575 EndY=-80.4316 EndZ=0
  constraints (11):
    c: Vertical(g0)
    c: Coincident(g1,g0)
    c: Horizontal(g1)
    c: Coincident(g2,g1)
    c: Vertical(g2)
    c: Coincident(g3,g2)
    c: Coincident(g3,g0)
    c: Horizontal(g3)
    c: DistanceX(g1,g1) = 1.8
    c: Coincident(g2,g-3)
    c: DistanceY(g2,g2) = 30
FEATURE [Part::Extrusion] Extrude040  label="Extrude040 scavo alimentatore"
  Base = -> Sketch037
  Dir = (0,-1,2e-16)
  DirMode = 2
  FaceMakerClass = Part::FaceMakerBullseye
  FaceMakerMode = 3
  LengthFwd = 19.5
  LengthRev = 0
  Solid = true
  Symmetric = true
FEATURE [Part::Extrusion] Extrude031  label="Extrude fermo per scheda micro"
  Base = -> Sketch033
  Dir = (0,-1,2e-16)
  DirMode = 2
  FaceMakerClass = Part::FaceMakerBullseye
  FaceMakerMode = 3
  LengthFwd = 3
  LengthRev = 0
  Placement = pos=(0,8.6,0) rot=(0,0,1;0rad)
  Solid = true
  Symmetric = false
FEATURE [Sketcher::SketchObject] Sketch038  label="scavo driver solenoide"
  ArcFitTolerance = 1e-06
  AttachmentSupport = -> [XZ_Plane]
  ExternalGeometry = -> [Sketch,Sketch036]
  FullyConstrained = true
  MakeInternals = false
  MapMode = 5
  Placement = pos=(0,0,0) rot=(1,0,0;1.5708rad)
  sketch-geometry (7):
    g0: LineSegment StartX=-190.448 StartY=-4.2115 StartZ=0 EndX=-191.898 EndY=-3.53531 EndZ=0
    g1: LineSegment StartX=-191.898 StartY=-3.53531 StartZ=0 EndX=-209.225 EndY=-40.6939 EndZ=0
    g2: LineSegment StartX=-190.448 StartY=-4.2115 StartZ=0 EndX=-187.004 EndY=-5.81745 EndZ=0
    g3: LineSegment StartX=-187.004 StartY=-5.81745 StartZ=0 EndX=-204.331 EndY=-42.9761 EndZ=0
    g4: LineSegment StartX=-204.331 StartY=-42.9761 StartZ=0 EndX=-207.775 EndY=-41.3701 EndZ=0
    g5: LineSegment [constr] StartX=-209.225 StartY=-40.6939 StartZ=0 EndX=-207.775 EndY=-41.3701 EndZ=0
    g6: LineSegment StartX=-209.225 StartY=-40.6939 StartZ=0 EndX=-207.775 EndY=-41.3701 EndZ=0
  constraints (19):
    c: Coincident(g1,g0)
    c: Coincident(g3,g2)
    c: Coincident(g4,g3)
    c: Distance(g2) = 3.8
    c: Distance(g1) = 41
    c: Coincident(g5,g1)
    c: Distance(g5) = 1.6
    c: Coincident(g-4,g5)
    c: Perpendicular(g5,g-3)
    c: Parallel(g1,g-3)
    c: Perpendicular(g1,g0)
    c: Distance(g0) = 1.6
    c: Coincident(g6,g1)
    c: Coincident(g6,g5)
    c: Parallel(g3,g-3)
    c: Perpendicular(g3,g4)
    c: Perpendicular(g2,g3)
    c: Coincident(g2,g0)
    c: Coincident(g4,g5)
FEATURE [Part::Extrusion] Extrude041  label="Extrude scavo driver solenoide"
  Base = -> Sketch038
  Dir = (0,-1,2e-16)
  DirMode = 2
  FaceMakerClass = Part::FaceMakerBullseye
  FaceMakerMode = 3
  LengthFwd = 20.8
  LengthRev = 0
  Solid = true
  Symmetric = true
FEATURE [Sketcher::SketchObject] Sketch039  label="scavo per cavo usb per micro"
  ArcFitTolerance = 1e-06
  AttachmentSupport = -> [XZ_Plane]
  ExternalGeometry = -> [Sketch,Sketch016]
  FullyConstrained = true
  MakeInternals = false
  MapMode = 5
  Placement = pos=(0,0,0) rot=(1,0,0;1.5708rad)
  sketch-geometry (4):
    g0: LineSegment StartX=-82.51 StartY=36.4 StartZ=0 EndX=-74.51 EndY=36.4 EndZ=0
    g1: LineSegment StartX=-74.51 StartY=36.4 StartZ=0 EndX=-74.51 EndY=30.8 EndZ=0
    g2: LineSegment StartX=-74.51 StartY=30.8 StartZ=0 EndX=-82.51 EndY=30.8 EndZ=0
    g3: LineSegment StartX=-82.51 StartY=30.8 StartZ=0 EndX=-82.51 EndY=36.4 EndZ=0
  constraints (11):
    c: Coincident(g1,g0)
    c: Vertical(g1)
    c: Coincident(g2,g1)
    c: Horizontal(g2)
    c: Coincident(g3,g2)
    c: Coincident(g3,g0)
    c: Vertical(g3)
    c: Tangent(g0,g-3)
    c: Tangent(g2,g-4)
    c: Tangent(g3,g-4)
    c: Tangent(g1,g-4)
FEATURE [Part::Extrusion] Extrude042  label="Extrude scavo per cavo usb per micro"
  Base = -> Sketch039
  Dir = (0,-1,2e-16)
  DirMode = 2
  FaceMakerClass = Part::FaceMakerBullseye
  FaceMakerMode = 3
  LengthFwd = 11.2
  LengthRev = 0
  Solid = true
  Symmetric = true
FEATURE [Sketcher::SketchObject] Sketch040  label="scavo saldature alimentatore connettore 5v"
  ArcFitTolerance = 1e-06
  AttachmentSupport = -> [XZ_Plane]
  ExternalGeometry = -> [Sketch037]
  FullyConstrained = true
  MakeInternals = false
  MapMode = 5
  Placement = pos=(0,0,0) rot=(1,0,0;1.5708rad)
  sketch-geometry (4):
    g0: LineSegment StartX=-211.175 StartY=-52.4316 StartZ=0 EndX=-211.175 EndY=-56.4316 EndZ=0
    g1: LineSegment StartX=-211.175 StartY=-52.4316 StartZ=0 EndX=-209.575 EndY=-52.4316 EndZ=0
    g2: LineSegment StartX=-209.575 StartY=-52.4316 StartZ=0 EndX=-209.575 EndY=-56.4316 EndZ=0
    g3: LineSegment StartX=-209.575 StartY=-56.4316 StartZ=0 EndX=-211.175 EndY=-56.4316 EndZ=0
  constraints (11):
    c: Vertical(g0)
    c: Coincident(g1,g0)
    c: Horizontal(g1)
    c: Coincident(g2,g1)
    c: Coincident(g3,g2)
    c: Coincident(g3,g0)
    c: Horizontal(g3)
    c: DistanceX(g1,g1) = 1.6
    c: DistanceY(g2,g2) = 4
    c: Tangent(g2,g-3)
    c: DistanceY(g1,g-3) = 2
FEATURE [Part::Extrusion] Extrude043  label="Extrude scavo saldature alimentatore connettore 5v"
  Base = -> Sketch040
  Dir = (0,-1,2e-16)
  DirMode = 2
  FaceMakerClass = Part::FaceMakerBullseye
  FaceMakerMode = 3
  LengthFwd = 8
  LengthRev = 0
  Solid = true
  Symmetric = true
FEATURE [Sketcher::SketchObject] Sketch041  label="scavo saldature alimentatore connettore 5v verticali"
  ArcFitTolerance = 1e-06
  AttachmentSupport = -> [XZ_Plane]
  ExternalGeometry = -> [Sketch037]
  FullyConstrained = true
  MakeInternals = false
  MapMode = 5
  Placement = pos=(0,0,0) rot=(1,0,0;1.5708rad)
  sketch-geometry (4):
    g0: LineSegment StartX=-211.175 StartY=-53.6316 StartZ=0 EndX=-209.575 EndY=-53.6316 EndZ=0
    g1: LineSegment StartX=-209.575 StartY=-53.6316 StartZ=0 EndX=-209.575 EndY=-76.6316 EndZ=0
    g2: LineSegment StartX=-209.575 StartY=-76.6316 StartZ=0 EndX=-211.175 EndY=-76.6316 EndZ=0
    g3: LineSegment StartX=-211.175 StartY=-76.6316 StartZ=0 EndX=-211.175 EndY=-53.6316 EndZ=0
  constraints (11):
    c: Horizontal(g0)
    c: Coincident(g1,g0)
    c: Coincident(g2,g1)
    c: Horizontal(g2)
    c: Coincident(g3,g2)
    c: Coincident(g3,g0)
    c: Vertical(g3)
    c: DistanceY(g3,g3) = 23
    c: DistanceX(g0,g0) = 1.6
    c: Tangent(g1,g-3)
    c: DistanceY(g0,g-3) = 3.2
FEATURE [Part::Extrusion] Extrude044  label="Extrude scavo saldature alimentatore connettore 5v verticali"
  Base = -> Sketch041
  Dir = (0,-1,2e-16)
  DirMode = 2
  FaceMakerClass = Part::FaceMakerBullseye
  FaceMakerMode = 3
  LengthFwd = 3.2
  LengthRev = 0
  Placement = pos=(0,8.3,0) rot=(0,0,1;0rad)
  Solid = true
  Symmetric = false
FEATURE [Sketcher::SketchObject] Sketch042  label="fermi per driver solenoide e alimentatore"
  ArcFitTolerance = 1e-06
  AttachmentSupport = -> [XZ_Plane]
  ExternalGeometry = -> [Sketch036,Sketch037,Sketch,Sketch038]
  FullyConstrained = true
  MakeInternals = false
  MapMode = 5
  Placement = pos=(0,0,0) rot=(1,0,0;1.5708rad)
  sketch-geometry (27):
    g0: LineSegment StartX=-199.238 StartY=-23.0627 StartZ=0 EndX=-200.168 EndY=-25.0566 EndZ=0
    g1: LineSegment StartX=-200.168 StartY=-25.0566 StartZ=0 EndX=-198.174 EndY=-25.9863 EndZ=0
    g2: LineSegment StartX=-198.174 StartY=-25.9863 StartZ=0 EndX=-197.244 EndY=-23.9925 EndZ=0
    g3: LineSegment StartX=-197.244 StartY=-23.9925 StartZ=0 EndX=-199.238 EndY=-23.0627 EndZ=0
    g4: LineSegment StartX=-200.012 StartY=-20.9364 StartZ=0 EndX=-202.294 EndY=-25.8305 EndZ=0
    g5: LineSegment StartX=-202.294 StartY=-25.8305 StartZ=0 EndX=-198.85 EndY=-27.4364 EndZ=0
    g6: LineSegment StartX=-196.724 StartY=-26.6625 StartZ=0 EndX=-195.794 EndY=-24.6687 EndZ=0
    g7: LineSegment StartX=-196.568 StartY=-22.5424 StartZ=0 EndX=-200.012 EndY=-20.9364 EndZ=0
    g8: LineSegment [constr] StartX=-197.4 StartY=-28.1126 StartZ=0 EndX=-196.724 EndY=-26.6625 EndZ=0
    g9: LineSegment [constr] StartX=-197.4 StartY=-28.1126 StartZ=0 EndX=-198.85 EndY=-27.4364 EndZ=0
    g10: ArcOfCircle CenterX=-197.244 CenterY=-23.9925 CenterZ=0 NormalX=0 NormalY=0 NormalZ=1 AngleXU=0 Radius=1.6 StartAngle=5.84685 EndAngle=7.41765
    g11: GeomPoint [constr] X=-195.118 Y=-23.2186 Z=0
    g12: ArcOfCircle CenterX=-198.174 CenterY=-25.9863 CenterZ=0 NormalX=0 NormalY=0 NormalZ=1 AngleXU=0 Radius=1.6 StartAngle=4.27606 EndAngle=5.84685
    g13: GeomPoint [constr] X=-197.4 Y=-28.1126 Z=0
    g14: LineSegment StartX=-207.775 StartY=-46.8316 StartZ=0 EndX=-207.775 EndY=-50.8316 EndZ=0
    g15: LineSegment StartX=-207.775 StartY=-46.8316 StartZ=0 EndX=-203.775 EndY=-46.8316 EndZ=0
    g16: LineSegment StartX=-203.775 StartY=-46.8316 StartZ=0 EndX=-203.775 EndY=-50.8316 EndZ=0
    g17: LineSegment StartX=-207.775 StartY=-50.8316 StartZ=0 EndX=-203.775 EndY=-50.8316 EndZ=0
    g18: LineSegment StartX=-209.375 StartY=-52.4316 StartZ=0 EndX=-203.775 EndY=-52.4316 EndZ=0
    g19: LineSegment StartX=-202.175 StartY=-50.8316 StartZ=0 EndX=-202.175 EndY=-46.8316 EndZ=0
    g20: LineSegment StartX=-203.775 StartY=-45.2316 StartZ=0 EndX=-209.375 EndY=-45.2316 EndZ=0
    g21: LineSegment StartX=-209.375 StartY=-45.2316 StartZ=0 EndX=-209.375 EndY=-52.4316 EndZ=0
    g22: ArcOfCircle CenterX=-203.775 CenterY=-46.8316 CenterZ=0 NormalX=0 NormalY=0 NormalZ=1 AngleXU=0 Radius=1.6 StartAngle=1.8e-15 EndAngle=1.5708
    g23: GeomPoint [constr] X=-202.175 Y=-45.2316 Z=0
    g24: ArcOfCircle CenterX=-203.775 CenterY=-50.8316 CenterZ=0 NormalX=0 NormalY=0 NormalZ=1 AngleXU=0 Radius=1.6 StartAngle=4.71239 EndAngle=6.28319
    g25: GeomPoint [constr] X=-202.175 Y=-52.4316 Z=0
    g26: LineSegment [constr] StartX=-207.775 StartY=-50.4316 StartZ=0 EndX=-207.775 EndY=-50.8316 EndZ=0
  constraints (69):
    c: Coincident(g1,g0)
    c: Coincident(g2,g1)
    c: Coincident(g3,g2)
    c: Coincident(g3,g0)
    c: Parallel(g0,g2)
    c: Perpendicular(g3,g0)
    c: Perpendicular(g1,g0)
    c: Coincident(g5,g4)
    c: Coincident(g7,g4)
    c: Distance(g3) = 2.2
    c: Distance(g2) = 2.2
    c: Parallel(g6,g2)
    c: Parallel(g6,g4)
    c: Perpendicular(g5,g6)
    c: Perpendicular(g7,g6)
    c: Distance(g13,g11) = 5.4
    c: Distance(g5,g13) = 5.4
    c: Coincident(g9,g8)
    c: Distance(g8) = 1.6
    c: Distance(g9) = 1.6
    c: Perpendicular(g9,g8)
    c: Parallel(g8,g6)
    c: Coincident(g8,g13)
    c: Distance(g8,g1) = 1.6
    c: Distance(g9,g1) = 1.6
    c: Tangent(g0,g-5)
    c: Distance(g0,g-6) = 18
    c: PointOnObject(g11,g7)
    c: PointOnObject(g11,g6)
    c: Tangent(g7,g10) = -1.5708
    c: Tangent(g6,g10) = -1.5708
    c: PointOnObject(g13,g5)
    c: Tangent(g5,g12) = -1.5708
    c: Tangent(g6,g12) = -1.5708
    c: Equal(g10,g12)
    c: Coincident(g10,g2)
    c: Vertical(g14)
    c: Coincident(g15,g14)
    c: Horizontal(g15)
    c: Coincident(g16,g15)
    c: Vertical(g16)
    c: Coincident(g17,g14)
    c: Coincident(g17,g16)
    c: Horizontal(g17)
    c: Distance(g16) = 4
    c: Distance(g15) = 4
    c: Horizontal(g18)
    c: Vertical(g19)
    c: Horizontal(g20)
    c: Coincident(g21,g20)
    c: Coincident(g21,g18)
    c: Vertical(g21)
    c: Distance(g20,g23) = 7.2
    c: Distance(g25,g23) = 7.2
    c: DistanceY(g18,g14) = 1.6
    c: DistanceX(g18,g14) = 1.6
    c: PointOnObject(g23,g20)
    c: PointOnObject(g23,g19)
    c: Tangent(g20,g22) = -1.5708
    c: Tangent(g19,g22) = -1.5708
    c: PointOnObject(g25,g19)
    c: Tangent(g18,g24) = -1.5708
    c: Tangent(g19,g24) = -1.5708
    c: Equal(g22,g24)
    c: Coincident(g22,g15)
    c: Vertical(g26)
    c: Distance(g26) = 0.4
    c: Coincident(g26,g-4)
    c: Coincident(g14,g26)
FEATURE [Part::Extrusion] Extrude045  label="Extrude fermi per driver solenoide e alimentatore"
  Base = -> Sketch042
  Dir = (0,-1,2e-16)
  DirMode = 2
  FaceMakerClass = Part::FaceMakerBullseye
  FaceMakerMode = 3
  LengthFwd = 25.2
  LengthRev = 0
  Solid = true
  Symmetric = true
FEATURE [Sketcher::SketchObject] Sketch043  label="scavo pulizia fermo alimentatore"
  ArcFitTolerance = 1e-06
  AttachmentSupport = -> [XZ_Plane]
  ExternalGeometry = -> [Sketch042,Sketch036,Sketch037]
  FullyConstrained = true
  MakeInternals = false
  MapMode = 5
  Placement = pos=(0,0,0) rot=(1,0,0;1.5708rad)
  sketch-geometry (6):
    g0: LineSegment StartX=-209.375 StartY=-52.4316 StartZ=0 EndX=-209.375 EndY=-50.4316 EndZ=0
    g1: LineSegment StartX=-209.375 StartY=-50.4316 StartZ=0 EndX=-207.775 EndY=-50.4316 EndZ=0
    g2: LineSegment StartX=-207.775 StartY=-50.4316 StartZ=0 EndX=-207.775 EndY=-45.2316 EndZ=0
    g3: LineSegment StartX=-207.775 StartY=-45.2316 StartZ=0 EndX=-202.175 EndY=-45.2316 EndZ=0
    g4: LineSegment StartX=-202.175 StartY=-45.2316 StartZ=0 EndX=-202.175 EndY=-52.4316 EndZ=0
    g5: LineSegment StartX=-202.175 StartY=-52.4316 StartZ=0 EndX=-209.375 EndY=-52.4316 EndZ=0
  constraints (13):
    c: Vertical(g0)
    c: Coincident(g1,g0)
    c: Coincident(g2,g1)
    c: Coincident(g3,g2)
    c: Coincident(g4,g3)
    c: Coincident(g5,g4)
    c: Coincident(g5,g0)
    c: Horizontal(g5)
    c: Coincident(g0,g-6)
    c: Tangent(g1,g-8)
    c: Tangent(g2,g-4)
    c: Tangent(g3,g-7)
    c: Tangent(g4,g-3)
FEATURE [Part::Extrusion] Extrude046  label="Extrude scavo pulizia fermo alimentatore"
  Base = -> Sketch043
  Dir = (0,-1,2e-16)
  DirMode = 2
  FaceMakerClass = Part::FaceMakerBullseye
  FaceMakerMode = 3
  LengthFwd = 19.5
  LengthRev = 0
  Solid = true
  Symmetric = true
FEATURE [Sketcher::SketchObject] Sketch044  label="buchini per fissaggio oled"
  ArcFitTolerance = 1e-06
  AttachmentSupport = -> [YZ_Plane]
  ExternalGeometry = -> [Sketch]
  FullyConstrained = true
  MakeInternals = false
  MapMode = 5
  Placement = pos=(0,0,0) rot=(0.57735,0.57735,0.57735;2.0944rad)
  sketch-geometry (5):
    g0: LineSegment [constr] StartX=1.5e-14 StartY=67.3588 StartZ=0 EndX=0 EndY=64.3588 EndZ=0
    g1: LineSegment [constr] StartX=0 StartY=64.3588 StartZ=0 EndX=10.4 EndY=64.3588 EndZ=0
    g2: LineSegment [constr] StartX=0 StartY=64.3588 StartZ=0 EndX=-10.4 EndY=64.3588 EndZ=0
    g3: Circle CenterX=10.4 CenterY=64.3588 CenterZ=0 NormalX=0 NormalY=0 NormalZ=1 AngleXU=0 Radius=1.5
    g4: Circle CenterX=-10.4 CenterY=64.3588 CenterZ=0 NormalX=0 NormalY=0 NormalZ=1 AngleXU=0 Radius=1.5
  constraints (13):
    c: Distance(g0) = 3
    c: PointOnObject(g0,g-2)
    c: Coincident(g1,g0)
    c: Horizontal(g1)
    c: Coincident(g2,g0)
    c: Horizontal(g2)
    c: DistanceX(g1,g1) = 10.4
    c: Coincident(g3,g1)
    c: Diameter(g4) = 3
    c: Coincident(g4,g2)
    c: Coincident(g0,g-7)
    c: Equal(g1,g2)
    c: Equal(g4,g3)
FEATURE [Part::Extrusion] Extrude047  label="Extrude buchini per fissaggio oled"
  Base = -> Sketch044
  Dir = (1,0,0)
  DirMode = 2
  FaceMakerClass = Part::FaceMakerBullseye
  FaceMakerMode = 3
  LengthFwd = 10
  LengthRev = 0
  Placement = pos=(-186,0,0) rot=(0,0,1;0rad)
  Solid = true
  Symmetric = false
FEATURE [Sketcher::SketchObject] Sketch046  label="scavo 5x5 neopixel"
  ArcFitTolerance = 1e-06
  AttachmentSupport = -> [YZ_Plane002]
  FullyConstrained = true
  MakeInternals = false
  MapMode = 5
  Placement = pos=(0,0,0) rot=(0.57735,0.57735,0.57735;2.0944rad)
  sketch-geometry (4):
    g0: LineSegment StartX=-2.7 StartY=2.7 StartZ=0 EndX=2.7 EndY=2.7 EndZ=0
    g1: LineSegment StartX=2.7 StartY=2.7 StartZ=0 EndX=2.7 EndY=-2.7 EndZ=0
    g2: LineSegment StartX=2.7 StartY=-2.7 StartZ=0 EndX=-2.7 EndY=-2.7 EndZ=0
    g3: LineSegment StartX=-2.7 StartY=-2.7 StartZ=0 EndX=-2.7 EndY=2.7 EndZ=0
  constraints (11):
    c: Horizontal(g0)
    c: Coincident(g1,g0)
    c: Vertical(g1)
    c: Coincident(g2,g1)
    c: Horizontal(g2)
    c: Coincident(g3,g2)
    c: Coincident(g3,g0)
    c: Vertical(g3)
    c: DistanceX(g0,g0) = 5.4
    c: DistanceY(g1,g1) = 5.4
    c: Symmetric(g0,g1,g-1)
FEATURE [Sketcher::SketchObject] Sketch047  label="scavo 10x10 neopixel corpo"
  ArcFitTolerance = 1e-06
  AttachmentOffset = pos=(0,0,1) rot=(0,0,1;0rad)
  AttachmentSupport = -> [YZ_Plane002]
  FullyConstrained = true
  MakeInternals = false
  MapMode = 5
  Placement = pos=(1,0,0) rot=(0.57735,0.57735,0.57735;2.0944rad)
  sketch-geometry (4):
    g0: LineSegment StartX=-5 StartY=5.1 StartZ=0 EndX=5 EndY=5.1 EndZ=0
    g1: LineSegment StartX=5 StartY=5.1 StartZ=0 EndX=5 EndY=-5.1 EndZ=0
    g2: LineSegment StartX=5 StartY=-5.1 StartZ=0 EndX=-5 EndY=-5.1 EndZ=0
    g3: LineSegment StartX=-5 StartY=-5.1 StartZ=0 EndX=-5 EndY=5.1 EndZ=0
  constraints (11):
    c: Horizontal(g0)
    c: Coincident(g1,g0)
    c: Vertical(g1)
    c: Coincident(g2,g1)
    c: Horizontal(g2)
    c: Coincident(g3,g2)
    c: Coincident(g3,g0)
    c: Vertical(g3)
    c: DistanceX(g0,g0) = 10
    c: DistanceY(g1,g1) = 10.2
    c: Symmetric(g0,g2,g-1)
FEATURE [Sketcher::SketchObject] Sketch048  label="buco per perno blocco neopixel"
  ArcFitTolerance = 1e-06
  AttachmentSupport = -> [XZ_Plane002]
  FullyConstrained = true
  MakeInternals = false
  MapMode = 5
  Placement = pos=(0,0,0) rot=(1,0,0;1.5708rad)
  sketch-geometry (4):
    g0: LineSegment StartX=3 StartY=1.2 StartZ=0 EndX=3 EndY=-1.2 EndZ=0
    g1: LineSegment StartX=3 StartY=-1.2 StartZ=0 EndX=5.4 EndY=-1.2 EndZ=0
    g2: LineSegment StartX=5.4 StartY=-1.2 StartZ=0 EndX=5.4 EndY=1.2 EndZ=0
    g3: LineSegment StartX=5.4 StartY=1.2 StartZ=0 EndX=3 EndY=1.2 EndZ=0
  constraints (11):
    c: Coincident(g1,g0)
    c: Horizontal(g1)
    c: Coincident(g2,g1)
    c: Vertical(g2)
    c: Coincident(g3,g2)
    c: Coincident(g3,g0)
    c: Horizontal(g3)
    c: DistanceX(g1,g1) = 2.4
    c: DistanceY(g2,g2) = 2.4
    c: Symmetric(g0,g0,g-1)
    c: DistanceX(g-1,g0) = 3
FEATURE [Sketcher::SketchObject] Sketch045  label="blocco principale per neopixel"
  ArcFitTolerance = 1e-06
  AttachmentSupport = -> [XZ_Plane002]
  ExternalGeometry = -> [Sketch048]
  FullyConstrained = true
  MakeInternals = false
  MapMode = 5
  Placement = pos=(0,0,0) rot=(1,0,0;1.5708rad)
  sketch-geometry (6):
    g0: LineSegment StartX=0 StartY=5.1 StartZ=0 EndX=0 EndY=-5.1 EndZ=0
    g1: LineSegment StartX=0 StartY=-5.1 StartZ=0 EndX=3 EndY=-5.1 EndZ=0
    g2: LineSegment StartX=7 StartY=-1.1 StartZ=0 EndX=7 EndY=5.1 EndZ=0
    g3: LineSegment StartX=7 StartY=5.1 StartZ=0 EndX=0 EndY=5.1 EndZ=0
    g4: ArcOfCircle CenterX=3 CenterY=-1.1 CenterZ=0 NormalX=0 NormalY=0 NormalZ=1 AngleXU=0 Radius=4 StartAngle=4.71239 EndAngle=6.28319
    g5: GeomPoint [constr] X=7 Y=-5.1 Z=0
  constraints (15):
    c: Vertical(g0)
    c: Coincident(g1,g0)
    c: Horizontal(g1)
    c: Vertical(g2)
    c: Coincident(g3,g2)
    c: Coincident(g3,g0)
    c: Horizontal(g3)
    c: DistanceY(g0,g0) = 10.2
    c: Symmetric(g0,g0,g-1)
    c: DistanceX(g3,g3) = 7
    c: PointOnObject(g5,g2)
    c: PointOnObject(g5,g1)
    c: Tangent(g2,g4) = -1.5708
    c: Tangent(g1,g4) = -1.5708
    c: DistanceX(g-3,g1) = 0
FEATURE [Sketcher::SketchObject] Sketch049  label="rinforzi esterni per corpo neopoixel"
  ArcFitTolerance = 1e-06
  AttachmentSupport = -> [XZ_Plane002]
  ExternalGeometry = -> [Sketch045]
  FullyConstrained = true
  MakeInternals = false
  MapMode = 5
  Placement = pos=(0,0,0) rot=(1,0,0;1.5708rad)
  sketch-geometry (8):
    g0: LineSegment StartX=1 StartY=-4.1 StartZ=0 EndX=2 EndY=-4.1 EndZ=0
    g1: LineSegment StartX=2 StartY=-4.1 StartZ=0 EndX=2 EndY=-5.1 EndZ=0
    g2: LineSegment StartX=2 StartY=-5.1 StartZ=0 EndX=1 EndY=-5.1 EndZ=0
    g3: LineSegment StartX=1 StartY=-5.1 StartZ=0 EndX=1 EndY=-4.1 EndZ=0
    g4: LineSegment StartX=1 StartY=5.1 StartZ=0 EndX=2 EndY=5.1 EndZ=0
    g5: LineSegment StartX=2 StartY=5.1 StartZ=0 EndX=2 EndY=4.1 EndZ=0
    g6: LineSegment StartX=2 StartY=4.1 StartZ=0 EndX=1 EndY=4.1 EndZ=0
    g7: LineSegment StartX=1 StartY=4.1 StartZ=0 EndX=1 EndY=5.1 EndZ=0
  constraints (24):
    c: Horizontal(g0)
    c: Coincident(g1,g0)
    c: Vertical(g1)
    c: Coincident(g2,g1)
    c: Horizontal(g2)
    c: Coincident(g3,g2)
    c: Coincident(g3,g0)
    c: Vertical(g3)
    c: Horizontal(g4)
    c: Coincident(g5,g4)
    c: Vertical(g5)
    c: Coincident(g6,g5)
    c: Horizontal(g6)
    c: Coincident(g7,g6)
    c: Coincident(g7,g4)
    c: Vertical(g7)
    c: DistanceX(g4,g4) = 1
    c: DistanceY(g5,g5) = 1
    c: DistanceX(g0,g0) = 1
    c: DistanceY(g1,g1) = 1
    c: DistanceX(g-3,g4) = 1
    c: DistanceY(g-3,g4) = 0
    c: DistanceX(g-4,g2) = 1
    c: DistanceY(g2,g-4) = 0
FEATURE [Sketcher::SketchObject] Sketch052  label="scavo saldature driver solenoide"
  ArcFitTolerance = 1e-06
  AttachmentSupport = -> [XZ_Plane]
  ExternalGeometry = -> [Sketch038]
  FullyConstrained = true
  MakeInternals = false
  MapMode = 5
  Placement = pos=(0,0,0) rot=(1,0,0;1.5708rad)
  sketch-geometry (4):
    g0: LineSegment StartX=-193.348 StartY=-2.85912 StartZ=0 EndX=-195.038 EndY=-6.48435 EndZ=0
    g1: LineSegment StartX=-195.038 StartY=-6.48435 StartZ=0 EndX=-193.588 EndY=-7.16054 EndZ=0
    g2: LineSegment StartX=-193.588 StartY=-7.16054 StartZ=0 EndX=-191.898 EndY=-3.53531 EndZ=0
    g3: LineSegment StartX=-191.898 StartY=-3.53531 StartZ=0 EndX=-193.348 EndY=-2.85912 EndZ=0
  constraints (11):
    c: Coincident(g1,g0)
    c: Coincident(g2,g1)
    c: Coincident(g3,g2)
    c: Coincident(g3,g0)
    c: Parallel(g2,g0)
    c: Perpendicular(g2,g3)
    c: Perpendicular(g1,g2,g1) = 1.5708
    c: Parallel(g2,g-3)
    c: Distance(g2) = 4
    c: Distance(g3) = 1.6
    c: Coincident(g2,g-3)
FEATURE [Part::Extrusion] Extrude055  label="Extrude scavo saldature driver solenoide"
  Base = -> Sketch052
  Dir = (0,-1,2e-16)
  DirMode = 2
  FaceMakerClass = Part::FaceMakerBullseye
  FaceMakerMode = 3
  LengthFwd = 6
  LengthRev = 0
  Solid = true
  Symmetric = true
FEATURE [Sketcher::SketchObject] Sketch053  label="scavo saldature rumble"
  ArcFitTolerance = 1e-06
  AttachmentSupport = -> [XZ_Plane]
  ExternalGeometry = -> [Sketch019]
  FullyConstrained = true
  MakeInternals = false
  MapMode = 5
  Placement = pos=(0,0,0) rot=(1,0,0;1.5708rad)
  sketch-geometry (4):
    g0: LineSegment StartX=-165.001 StartY=-43.1663 StartZ=0 EndX=-166.238 EndY=-46.9705 EndZ=0
    g1: LineSegment StartX=-166.238 StartY=-46.9705 StartZ=0 EndX=-165.096 EndY=-47.3413 EndZ=0
    g2: LineSegment StartX=-165.096 StartY=-47.3413 StartZ=0 EndX=-163.86 EndY=-43.5371 EndZ=0
    g3: LineSegment StartX=-163.86 StartY=-43.5371 StartZ=0 EndX=-165.001 EndY=-43.1663 EndZ=0
  constraints (11):
    c: Coincident(g1,g0)
    c: Coincident(g2,g1)
    c: Coincident(g3,g2)
    c: Coincident(g3,g0)
    c: Parallel(g0,g2)
    c: Perpendicular(g3,g0)
    c: Perpendicular(g1,g0)
    c: Parallel(g0,g-3)
    c: Distance(g0) = 4
    c: Distance(g1) = 1.2
    c: Coincident(g0,g-3)
FEATURE [Part::Extrusion] Extrude056  label="Extrude scavo saldature rumble"
  Base = -> Sketch053
  Dir = (0,-1,2e-16)
  DirMode = 2
  FaceMakerClass = Part::FaceMakerBullseye
  FaceMakerMode = 3
  LengthFwd = 8.4
  LengthRev = 0
  Solid = true
  Symmetric = true
FEATURE [Sketcher::SketchObject] Sketch054  label="scavo saldature alimentatore connettore USB"
  ArcFitTolerance = 1e-06
  AttachmentSupport = -> [XZ_Plane]
  ExternalGeometry = -> [Sketch037]
  FullyConstrained = true
  MakeInternals = false
  MapMode = 5
  Placement = pos=(0,0,0) rot=(1,0,0;1.5708rad)
  sketch-geometry (4):
    g0: LineSegment StartX=-209.575 StartY=-80.4316 StartZ=0 EndX=-210.375 EndY=-80.4316 EndZ=0
    g1: LineSegment StartX=-210.375 StartY=-80.4316 StartZ=0 EndX=-210.375 EndY=-72.4316 EndZ=0
    g2: LineSegment StartX=-210.375 StartY=-72.4316 StartZ=0 EndX=-209.575 EndY=-72.4316 EndZ=0
    g3: LineSegment StartX=-209.575 StartY=-72.4316 StartZ=0 EndX=-209.575 EndY=-80.4316 EndZ=0
  constraints (11):
    c: Horizontal(g0)
    c: Coincident(g1,g0)
    c: Vertical(g1)
    c: Coincident(g2,g1)
    c: Horizontal(g2)
    c: Coincident(g3,g2)
    c: Coincident(g3,g0)
    c: Vertical(g3)
    c: DistanceX(g0,g0) = 0.8
    c: DistanceY(g3,g3) = 8
    c: Coincident(g0,g-4)
FEATURE [Part::Extrusion] Extrude057  label="Extrude scavo saldature alimentatore connettore USB"
  Base = -> Sketch054
  Dir = (0,-1,2e-16)
  DirMode = 2
  FaceMakerClass = Part::FaceMakerBullseye
  FaceMakerMode = 3
  LengthFwd = 11
  LengthRev = 0
  Solid = true
  Symmetric = true
FEATURE [Sketcher::SketchObject] Sketch055  label="buco interno per micro switch"
  ArcFitTolerance = 1e-06
  AttachmentSupport = -> [XZ_Plane]
  ExternalGeometry = -> [Sketch]
  FullyConstrained = true
  MakeInternals = false
  MapMode = 5
  Placement = pos=(0,0,0) rot=(1,0,0;1.5708rad)
  sketch-geometry (11):
    g0: LineSegment [constr] StartX=-194.483 StartY=34.2854 StartZ=0 EndX=-196.022 EndY=30.0568 EndZ=0
    g1: LineSegment [constr] StartX=-196.022 StartY=30.0568 StartZ=0 EndX=-197.561 EndY=25.8282 EndZ=0
    g2: LineSegment [constr] StartX=-196.022 StartY=30.0568 StartZ=0 EndX=-194.143 EndY=29.3727 EndZ=0
    g3: LineSegment [constr] StartX=-196.022 StartY=30.0568 StartZ=0 EndX=-197.902 EndY=30.7408 EndZ=0
    g4: LineSegment StartX=-196.362 StartY=34.9694 StartZ=0 EndX=-192.604 EndY=33.6014 EndZ=0
    g5: LineSegment StartX=-199.441 StartY=26.5122 StartZ=0 EndX=-195.682 EndY=25.1441 EndZ=0
    g6: LineSegment StartX=-192.604 StartY=33.6014 StartZ=0 EndX=-195.682 EndY=25.1441 EndZ=0
    g7: LineSegment StartX=-196.362 StartY=34.9694 StartZ=0 EndX=-199.441 EndY=26.5122 EndZ=0
    g8: GeomPoint [constr] X=-187.821 Y=29.2 Z=0
    g9: LineSegment [constr] StartX=-188.505 StartY=27.3206 StartZ=0 EndX=-196.022 EndY=30.0568 EndZ=0
    g10: LineSegment [constr] StartX=-187.821 StartY=29.2 StartZ=0 EndX=-188.505 EndY=27.3206 EndZ=0
  constraints (27):
    c: Coincident(g2,g0)
    c: Parallel(g0,g-3)
    c: Tangent(g1,g0) = -1.5708
    c: Perpendicular(g0,g2)
    c: Tangent(g2,g3)
    c: Distance(g0,g1) = 9
    c: Equal(g0,g1)
    c: Distance(g3,g2) = 4
    c: Equal(g2,g3)
    c: Parallel(g3,g4)
    c: Symmetric(g4,g4,g0)
    c: Parallel(g6,g1)
    c: Parallel(g7,g1)
    c: Symmetric(g6,g6,g2)
    c: Symmetric(g5,g5,g1)
    c: Symmetric(g7,g7,g3)
    c: Coincident(g7,g4)
    c: Coincident(g6,g4)
    c: Coincident(g5,g6)
    c: Symmetric(g-3,g-3,g8)
    c: Perpendicular(g-3,g9)
    c: Distance(g9) = 8
    c: Coincident(g3,g9)
    c: Coincident(g10,g8)
    c: Parallel(g10,g-3)
    c: Distance(g10) = 2
    c: Coincident(g10,g9)
FEATURE [Sketcher::SketchObject] Sketch056  label="buco esterno per micro switch"
  ArcFitTolerance = 1e-06
  AttachmentSupport = -> [XZ_Plane]
  ExternalGeometry = -> [Sketch055]
  FullyConstrained = true
  MakeInternals = false
  MapMode = 5
  Placement = pos=(0,0,0) rot=(1,0,0;1.5708rad)
  sketch-geometry (17):
    g0: GeomPoint [constr] X=-194.143 Y=29.3727 Z=0
    g1: GeomPoint [constr] X=-194.483 Y=34.2854 Z=0
    g2: GeomPoint [constr] X=-197.902 Y=30.7408 Z=0
    g3: GeomPoint [constr] X=-197.561 Y=25.8282 Z=0
    g4: GeomPoint [constr] X=-196.022 Y=30.0568 Z=0
    g5: LineSegment [constr] StartX=-194.483 StartY=34.2854 StartZ=0 EndX=-196.022 EndY=30.0568 EndZ=0
    g6: LineSegment [constr] StartX=-196.022 StartY=30.0568 StartZ=0 EndX=-197.561 EndY=25.8282 EndZ=0
    g7: LineSegment [constr] StartX=-197.902 StartY=30.7408 StartZ=0 EndX=-196.022 EndY=30.0568 EndZ=0
    g8: LineSegment [constr] StartX=-196.022 StartY=30.0568 StartZ=0 EndX=-194.143 EndY=29.3727 EndZ=0
    g9: LineSegment [constr] StartX=-195.338 StartY=31.9362 StartZ=0 EndX=-196.022 EndY=30.0568 EndZ=0
    g10: LineSegment [constr] StartX=-196.022 StartY=30.0568 StartZ=0 EndX=-196.706 EndY=28.1774 EndZ=0
    g11: LineSegment [constr] StartX=-196.022 StartY=30.0568 StartZ=0 EndX=-196.821 EndY=30.3475 EndZ=0
    g12: LineSegment [constr] StartX=-196.022 StartY=30.0568 StartZ=0 EndX=-195.223 EndY=29.7661 EndZ=0
    g13: LineSegment StartX=-194.539 StartY=31.6454 StartZ=0 EndX=-195.907 EndY=27.8867 EndZ=0
    g14: LineSegment StartX=-196.137 StartY=32.2269 StartZ=0 EndX=-197.505 EndY=28.4681 EndZ=0
    g15: LineSegment StartX=-196.137 StartY=32.2269 StartZ=0 EndX=-194.539 EndY=31.6454 EndZ=0
    g16: LineSegment StartX=-197.505 StartY=28.4681 StartZ=0 EndX=-195.907 EndY=27.8867 EndZ=0
  constraints (34):
    c: Symmetric(g-5,g-5,g1)
    c: Symmetric(g-5,g-6,g0)
    c: Symmetric(g-6,g-6,g3)
    c: Symmetric(g-5,g-6,g2)
    c: Coincident(g5,g1)
    c: Coincident(g5,g4)
    c: Coincident(g6,g4)
    c: Coincident(g6,g3)
    c: Equal(g5,g6)
    c: Coincident(g7,g2)
    c: Coincident(g7,g4)
    c: Coincident(g8,g4)
    c: Coincident(g8,g0)
    c: Equal(g7,g8)
    c: Coincident(g11,g9)
    c: Coincident(g12,g9)
    c: Tangent(g10,g9) = -1.5708
    c: Perpendicular(g11,g9)
    c: Parallel(g9,g-4)
    c: Equal(g9,g10)
    c: Parallel(g12,g11)
    c: Equal(g11,g12)
    c: Distance(g11,g12) = 1.7
    c: Distance(g9,g10) = 4
    c: Symmetric(g13,g13,g12)
    c: Parallel(g13,g9)
    c: Symmetric(g14,g14,g11)
    c: Symmetric(g15,g15,g9)
    c: Parallel(g15,g11)
    c: Symmetric(g16,g16,g10)
    c: Coincident(g16,g14)
    c: Coincident(g15,g14)
    c: Coincident(g13,g15)
    c: Coincident(g9,g4)
FEATURE [Sketcher::SketchObject] Sketch057  label="buco interno per SWITCH"
  ArcFitTolerance = 1e-06
  AttachmentSupport = -> [XZ_Plane]
  ExternalGeometry = -> [Sketch]
  FullyConstrained = true
  MakeInternals = false
  MapMode = 5
  Placement = pos=(0,0,0) rot=(1,0,0;1.5708rad)
  sketch-geometry (10):
    g0: GeomPoint [constr] X=-187.821 Y=29.2 Z=0
    g1: LineSegment [constr] StartX=-188.505 StartY=27.3206 StartZ=0 EndX=-193.203 EndY=29.0307 EndZ=0
    g2: LineSegment [constr] StartX=-190.809 StartY=35.6086 StartZ=0 EndX=-195.597 EndY=22.4529 EndZ=0
    g3: GeomPoint [constr] X=-193.203 Y=29.0307 Z=0
    g4: LineSegment [constr] StartX=-196.492 StartY=30.2278 StartZ=0 EndX=-189.914 EndY=27.8336 EndZ=0
    g5: LineSegment StartX=-194.098 StartY=36.8056 StartZ=0 EndX=-187.52 EndY=34.4115 EndZ=0
    g6: LineSegment StartX=-194.098 StartY=36.8056 StartZ=0 EndX=-198.886 EndY=23.6499 EndZ=0
    g7: LineSegment StartX=-187.52 StartY=34.4115 StartZ=0 EndX=-192.308 EndY=21.2558 EndZ=0
    g8: LineSegment StartX=-198.886 StartY=23.6499 StartZ=0 EndX=-192.308 EndY=21.2558 EndZ=0
    g9: LineSegment [constr] StartX=-187.821 StartY=29.2 StartZ=0 EndX=-188.505 EndY=27.3206 EndZ=0
  constraints (23):
    c: Symmetric(g-3,g-3,g0)
    c: Perpendicular(g1,g-3)
    c: Parallel(g2,g-3)
    c: Symmetric(g2,g2,g3)
    c: Perpendicular(g2,g4)
    c: Symmetric(g4,g4,g3)
    c: Distance(g2) = 14
    c: Distance(g4) = 7
    c: Distance(g1) = 5
    c: Parallel(g5,g4)
    c: Parallel(g7,g2)
    c: Symmetric(g5,g5,g2)
    c: Symmetric(g6,g6,g4)
    c: Symmetric(g7,g7,g4)
    c: Symmetric(g8,g8,g2)
    c: Coincident(g6,g5)
    c: Coincident(g7,g5)
    c: Coincident(g8,g7)
    c: Coincident(g3,g1)
    c: Coincident(g9,g0)
    c: Parallel(g9,g-3)
    c: Distance(g9) = 2
    c: Coincident(g1,g9)
FEATURE [Sketcher::SketchObject] Sketch058  label="buco esterno per SWITCH"
  ArcFitTolerance = 1e-06
  AttachmentSupport = -> [XZ_Plane]
  ExternalGeometry = -> [Sketch057]
  FullyConstrained = true
  MakeInternals = false
  MapMode = 5
  Placement = pos=(0,0,0) rot=(1,0,0;1.5708rad)
  sketch-geometry (12):
    g0: GeomPoint [constr] X=-190.809 Y=35.6086 Z=0
    g1: GeomPoint [constr] X=-196.492 Y=30.2278 Z=0
    g2: GeomPoint [constr] X=-189.914 Y=27.8336 Z=0
    g3: GeomPoint [constr] X=-195.597 Y=22.4529 Z=0
    g4: GeomPoint [constr] X=-193.203 Y=29.0307 Z=0
    g5: LineSegment [constr] StartX=-192.006 StartY=32.3196 StartZ=0 EndX=-194.4 EndY=25.7418 EndZ=0
    g6: GeomPoint [constr] X=-193.203 Y=29.0307 Z=0
    g7: LineSegment [constr] StartX=-195.082 StartY=29.7148 StartZ=0 EndX=-191.324 EndY=28.3467 EndZ=0
    g8: LineSegment StartX=-193.885 StartY=33.0037 StartZ=0 EndX=-190.127 EndY=31.6356 EndZ=0
    g9: LineSegment StartX=-190.127 StartY=31.6356 StartZ=0 EndX=-192.521 EndY=25.0578 EndZ=0
    g10: LineSegment StartX=-196.28 StartY=26.4258 StartZ=0 EndX=-192.521 EndY=25.0578 EndZ=0
    g11: LineSegment StartX=-193.885 StartY=33.0037 StartZ=0 EndX=-196.28 EndY=26.4258 EndZ=0
  constraints (21):
    c: Symmetric(g-6,g-6,g3)
    c: Symmetric(g-4,g-6,g2)
    c: Symmetric(g-5,g-4,g0)
    c: Symmetric(g-5,g-6,g1)
    c: Symmetric(g1,g2,g4)
    c: Parallel(g5,g-4)
    c: Symmetric(g5,g5,g6)
    c: Perpendicular(g7,g5)
    c: Symmetric(g7,g7,g6)
    c: Distance(g5) = 7
    c: Distance(g7) = 4
    c: Parallel(g8,g7)
    c: Parallel(g11,g5)
    c: Symmetric(g8,g8,g5)
    c: Symmetric(g9,g9,g7)
    c: Symmetric(g10,g10,g5)
    c: Symmetric(g11,g11,g7)
    c: Coincident(g11,g8)
    c: Coincident(g9,g8)
    c: Coincident(g9,g10)
    c: Coincident(g6,g4)
FEATURE [Part::Extrusion] Extrude060  label="Extrude buco interno per SWITCH destro"
  Base = -> Sketch057
  Dir = (0,-1,2e-16)
  DirMode = 2
  FaceMakerClass = Part::FaceMakerBullseye
  FaceMakerMode = 3
  LengthFwd = 13.2
  LengthRev = 0
  Placement = pos=(0,2.6,0) rot=(0,0,1;0rad)
  Solid = true
  Symmetric = false
FEATURE [Part::Extrusion] Extrude061  label="Extrude buco esterno per SWITCH destro"
  Base = -> Sketch058
  Dir = (0,-1,2e-16)
  DirMode = 2
  FaceMakerClass = Part::FaceMakerBullseye
  FaceMakerMode = 3
  LengthFwd = 2
  LengthRev = 0
  Placement = pos=(0,-10.6,0) rot=(0,0,1;0rad)
  Solid = true
  Symmetric = false
FEATURE [Sketcher::SketchObject] Sketch059  label="buco per spazio introduzione SWITCH"
  ArcFitTolerance = 1e-06
  AttachmentSupport = -> [XZ_Plane]
  ExternalGeometry = -> [Sketch057,Sketch010]
  FullyConstrained = true
  MakeInternals = false
  MapMode = 5
  Placement = pos=(0,0,0) rot=(1,0,0;1.5708rad)
  sketch-geometry (8):
    g0: LineSegment [constr] StartX=-201.368 StartY=36.3521 StartZ=0 EndX=-195.094 EndY=34.0687 EndZ=0
    g1: LineSegment [constr] StartX=-194.098 StartY=36.8056 StartZ=0 EndX=-195.094 EndY=34.0687 EndZ=0
    g2: LineSegment StartX=-198.658 StartY=24.2771 StartZ=0 EndX=-199.654 EndY=21.5401 EndZ=0
    g3: LineSegment StartX=-199.654 StartY=21.5401 StartZ=0 EndX=-181.196 EndY=14.822 EndZ=0
    g4: LineSegment StartX=-181.196 StartY=14.822 StartZ=0 EndX=-180.2 EndY=17.559 EndZ=0
    g5: LineSegment StartX=-180.2 StartY=17.559 StartZ=0 EndX=-198.658 EndY=24.2771 EndZ=0
    g6: LineSegment [constr] StartX=-204.932 StartY=26.5605 StartZ=0 EndX=-198.658 EndY=24.2771 EndZ=0
    g7: LineSegment [constr] StartX=-198.658 StartY=24.2771 StartZ=0 EndX=-199.654 EndY=21.5401 EndZ=0
  constraints (20):
    c: Parallel(g1,g-3)
    c: Parallel(g0,g-4)
    c: Coincident(g0,g-4)
    c: Coincident(g1,g-3)
    c: Coincident(g0,g1)
    c: Coincident(g3,g2)
    c: Coincident(g4,g3)
    c: Coincident(g5,g4)
    c: Coincident(g5,g2)
    c: Parallel(g5,g-5)
    c: Parallel(g3,g-5)
    c: Parallel(g4,g-6)
    c: DistanceX(g-6,g4) = 0
    c: Coincident(g6,g-5)
    c: Equal(g6,g0)
    c: Coincident(g7,g6)
    c: Equal(g7,g1)
    c: Tangent(g7,g-3)
    c: Coincident(g2,g6)
    c: Coincident(g2,g7)
FEATURE [Part::Extrusion] Extrude062  label="Extrude buco per spazio introduzione SWITCH"
  Base = -> Sketch059
  Dir = (0,-1,2e-16)
  DirMode = 2
  FaceMakerClass = Part::FaceMakerBullseye
  FaceMakerMode = 3
  LengthFwd = 13.2
  LengthRev = 0
  Solid = true
  Symmetric = true
FEATURE [Part::Extrusion] Extrude063  label="Extrude buco interno per SWITCH sinistro"
  Base = -> Sketch057
  Dir = (0,-1,2e-16)
  DirMode = 2
  FaceMakerClass = Part::FaceMakerBullseye
  FaceMakerMode = 3
  LengthFwd = 13.2
  LengthRev = 0
  Placement = pos=(0,10.6,0) rot=(0,0,1;0rad)
  Solid = true
  Symmetric = false
FEATURE [Part::Extrusion] Extrude064  label="Extrude buco esterno per SWITCH sinistro"
  Base = -> Sketch058
  Dir = (0,-1,2e-16)
  DirMode = 2
  FaceMakerClass = Part::FaceMakerBullseye
  FaceMakerMode = 3
  LengthFwd = 2
  LengthRev = 0
  Placement = pos=(0,12.6,0) rot=(0,0,1;0rad)
  Solid = true
  Symmetric = false
FEATURE [Sketcher::SketchObject] Sketch061  label="struttura esterna blocco switch"
  ArcFitTolerance = 1e-06
  AttachmentSupport = -> [XZ_Plane003]
  FullyConstrained = true
  MakeInternals = false
  MapMode = 5
  Placement = pos=(0,0,0) rot=(1,0,0;1.5708rad)
  sketch-geometry (5):
    g0: LineSegment StartX=-1 StartY=-5.1 StartZ=0 EndX=1 EndY=-5.1 EndZ=0
    g1: LineSegment StartX=1 StartY=-5.1 StartZ=0 EndX=1 EndY=5.1 EndZ=0
    g2: LineSegment StartX=1 StartY=5.1 StartZ=0 EndX=-1 EndY=5.1 EndZ=0
    g3: LineSegment StartX=-1 StartY=5.1 StartZ=0 EndX=-1 EndY=-5.1 EndZ=0
    g4: GeomPoint [constr] X=0 Y=0 Z=0
  constraints (12):
    c: Coincident(g0,g1)
    c: Coincident(g1,g2)
    c: Coincident(g2,g3)
    c: Coincident(g3,g0)
    c: Horizontal(g0)
    c: Horizontal(g2)
    c: Vertical(g1)
    c: Vertical(g3)
    c: Symmetric(g2,g0,g4)
    c: Distance(g1,g3) = 2
    c: Distance(g0,g2) = 10.2
    c: Coincident(g4,g-1)
FEATURE [Sketcher::SketchObject] Sketch062  label="struttura interna blocco switch"
  ArcFitTolerance = 1e-06
  AttachmentSupport = -> [XZ_Plane003]
  ExternalGeometry = -> [Sketch061]
  FullyConstrained = true
  MakeInternals = false
  MapMode = 5
  Placement = pos=(0,0,0) rot=(1,0,0;1.5708rad)
  sketch-geometry (5):
    g0: LineSegment StartX=-1 StartY=3.1 StartZ=0 EndX=-1 EndY=-3.1 EndZ=0
    g1: LineSegment StartX=-1 StartY=-3.1 StartZ=0 EndX=1 EndY=-3.1 EndZ=0
    g2: LineSegment StartX=1 StartY=-3.1 StartZ=0 EndX=1 EndY=3.1 EndZ=0
    g3: LineSegment StartX=1 StartY=3.1 StartZ=0 EndX=-1 EndY=3.1 EndZ=0
    g4: GeomPoint [constr] X=0 Y=0 Z=0
  constraints (12):
    c: Coincident(g0,g1)
    c: Coincident(g1,g2)
    c: Coincident(g2,g3)
    c: Coincident(g3,g0)
    c: Vertical(g0)
    c: Vertical(g2)
    c: Horizontal(g1)
    c: Horizontal(g3)
    c: Symmetric(g2,g0,g4)
    c: Coincident(g4,g-1)
    c: Distance(g0) = 6.2
    c: Equal(g3,g-3)
FEATURE [Sketcher::SketchObject] Sketch063  label="blocchi tra switch"
  ArcFitTolerance = 1e-06
  AttachmentSupport = -> [XZ_Plane003]
  ExternalGeometry = -> [Sketch061,Sketch062]
  FullyConstrained = true
  MakeInternals = false
  MapMode = 5
  Placement = pos=(0,0,0) rot=(1,0,0;1.5708rad)
  sketch-geometry (8):
    g0: LineSegment StartX=-3 StartY=5.1 StartZ=0 EndX=-1 EndY=5.1 EndZ=0
    g1: LineSegment StartX=-1 StartY=5.1 StartZ=0 EndX=-1 EndY=3.1 EndZ=0
    g2: LineSegment StartX=-1 StartY=3.1 StartZ=0 EndX=-3 EndY=3.1 EndZ=0
    g3: LineSegment StartX=-3 StartY=3.1 StartZ=0 EndX=-3 EndY=5.1 EndZ=0
    g4: LineSegment StartX=-3 StartY=-3.1 StartZ=0 EndX=-1 EndY=-3.1 EndZ=0
    g5: LineSegment StartX=-1 StartY=-3.1 StartZ=0 EndX=-1 EndY=-5.1 EndZ=0
    g6: LineSegment StartX=-1 StartY=-5.1 StartZ=0 EndX=-3 EndY=-5.1 EndZ=0
    g7: LineSegment StartX=-3 StartY=-5.1 StartZ=0 EndX=-3 EndY=-3.1 EndZ=0
  constraints (20):
    c: Horizontal(g0)
    c: Coincident(g1,g0)
    c: Coincident(g2,g1)
    c: Horizontal(g2)
    c: Coincident(g3,g2)
    c: Coincident(g3,g0)
    c: Vertical(g3)
    c: Horizontal(g4)
    c: Coincident(g5,g4)
    c: Coincident(g6,g5)
    c: Horizontal(g6)
    c: Coincident(g7,g6)
    c: Coincident(g7,g4)
    c: Vertical(g7)
    c: Coincident(g0,g-4)
    c: Coincident(g1,g-5)
    c: Coincident(g4,g-6)
    c: Coincident(g5,g-7)
    c: Distance(g0) = 2
    c: Distance(g4) = 2
FEATURE [Sketcher::SketchObject] Sketch066  label="piano per rampino"
  ArcFitTolerance = 1e-06
  AttachmentSupport = -> [XZ_Plane002]
  ExternalGeometry = -> [Sketch045]
  FullyConstrained = true
  MakeInternals = false
  MapMode = 5
  Placement = pos=(0,0,0) rot=(1,0,0;1.5708rad)
  sketch-geometry (4):
    g0: LineSegment StartX=5.4 StartY=5.1 StartZ=0 EndX=5.4 EndY=3.9 EndZ=0
    g1: LineSegment StartX=5.4 StartY=3.9 StartZ=0 EndX=7 EndY=3.9 EndZ=0
    g2: LineSegment StartX=7 StartY=3.9 StartZ=0 EndX=7 EndY=5.1 EndZ=0
    g3: LineSegment StartX=7 StartY=5.1 StartZ=0 EndX=5.4 EndY=5.1 EndZ=0
  constraints (11):
    c: Coincident(g0,g1)
    c: Coincident(g1,g2)
    c: Coincident(g2,g3)
    c: Coincident(g3,g0)
    c: Vertical(g0)
    c: Vertical(g2)
    c: Horizontal(g1)
    c: Horizontal(g3)
    c: Distance(g0,g2) = 1.6
    c: Distance(g1,g3) = 1.2
    c: Coincident(g2,g-3)
FEATURE [Sketcher::SketchObject] Sketch064  label="rampini_per_serraggio_struttura"
  ArcFitTolerance = 1e-06
  AttachmentSupport = -> [XZ_Plane002]
  ExternalGeometry = -> [Sketch066,Sketch045]
  FullyConstrained = true
  MakeInternals = false
  MapMode = 5
  Placement = pos=(0,0,0) rot=(1,0,0;1.5708rad)
  sketch-geometry (7):
    g0: LineSegment StartX=7 StartY=5.1 StartZ=0 EndX=7 EndY=3.9 EndZ=0
    g1: LineSegment StartX=7 StartY=3.9 StartZ=0 EndX=9 EndY=3.9 EndZ=0
    g2: LineSegment StartX=7 StartY=5.1 StartZ=0 EndX=7 EndY=5.1 EndZ=0
    g3: LineSegment StartX=7 StartY=5.1 StartZ=0 EndX=7 EndY=7.5 EndZ=0
    g4: LineSegment StartX=9 StartY=5.1 StartZ=0 EndX=9 EndY=3.9 EndZ=0
    g5: LineSegment StartX=7 StartY=7.5 StartZ=0 EndX=9 EndY=7.5 EndZ=0
    g6: LineSegment StartX=9 StartY=7.5 StartZ=0 EndX=9 EndY=5.1 EndZ=0
  constraints (20):
    c: Vertical(g0)
    c: Coincident(g1,g0)
    c: Horizontal(g1)
    c: Coincident(g2,g0)
    c: Horizontal(g2)
    c: Coincident(g3,g2)
    c: Vertical(g3)
    c: Coincident(g5,g3)
    c: Coincident(g4,g6)
    c: Coincident(g4,g1)
    c: Vertical(g4)
    c: Coincident(g0,g-3)
    c: DistanceY(g-4,g3) = 2.4
    c: DistanceX(g1,g1) = 2
    c: DistanceY(g2,g6) = 0
    c: DistanceX(g2,g2) = 0
    c: DistanceY(g0,g0) = 1.2
    c: Coincident(g5,g6)
    c: Horizontal(g5)
    c: Vertical(g6)
FEATURE [Sketcher::SketchObject] Sketch067  label="perno per blocco switch"
  ArcFitTolerance = 1e-06
  AttachmentSupport = -> [XZ_Plane]
  ExternalGeometry = -> [Sketch,Sketch010]
  FullyConstrained = true
  MakeInternals = false
  MapMode = 5
  Placement = pos=(0,0,0) rot=(1,0,0;1.5708rad)
  sketch-geometry (14):
    g0: LineSegment StartX=-191.073 StartY=24.9429 StartZ=0 EndX=-185.81 EndY=23.0276 EndZ=0
    g1: LineSegment StartX=-183.76 StartY=23.9839 StartZ=0 EndX=-182.392 EndY=27.7427 EndZ=0
    g2: LineSegment StartX=-183.348 StartY=29.7934 StartZ=0 EndX=-188.61 EndY=31.7087 EndZ=0
    g3: LineSegment StartX=-188.61 StartY=31.7087 StartZ=0 EndX=-191.073 EndY=24.9429 EndZ=0
    g4: GeomPoint [constr] X=-186.459 Y=27.0946 Z=0
    g5: LineSegment StartX=-189.022 StartY=25.8992 StartZ=0 EndX=-185.263 EndY=24.5311 EndZ=0
    g6: LineSegment StartX=-185.263 StartY=24.5311 StartZ=0 EndX=-183.895 EndY=28.2899 EndZ=0
    g7: LineSegment StartX=-183.895 StartY=28.2899 StartZ=0 EndX=-187.654 EndY=29.658 EndZ=0
    g8: LineSegment StartX=-187.654 StartY=29.658 StartZ=0 EndX=-189.022 EndY=25.8992 EndZ=0
    g9: GeomPoint [constr] X=-186.459 Y=27.0946 Z=0
    g10: ArcOfCircle CenterX=-185.263 CenterY=24.5311 CenterZ=0 NormalX=0 NormalY=0 NormalZ=1 AngleXU=0 Radius=1.6 StartAngle=4.36332 EndAngle=5.93412
    g11: GeomPoint [constr] X=-184.307 Y=22.4804 Z=0
    g12: ArcOfCircle CenterX=-183.895 CenterY=28.2899 CenterZ=0 NormalX=0 NormalY=0 NormalZ=1 AngleXU=0 Radius=1.6 StartAngle=5.93412 EndAngle=7.50492
    g13: GeomPoint [constr] X=-181.844 Y=29.2462 Z=0
  constraints (30):
    c: Coincident(g2,g3)
    c: Coincident(g3,g0)
    c: Symmetric(g13,g0,g4)
    c: Distance(g11,g3) = 7.2
    c: Distance(g0,g2) = 7.2
    c: Parallel(g3,g1)
    c: Parallel(g2,g0)
    c: Perpendicular(g2,g3)
    c: Coincident(g5,g6)
    c: Coincident(g6,g7)
    c: Coincident(g7,g8)
    c: Coincident(g8,g5)
    c: Symmetric(g7,g5,g9)
    c: Distance(g6,g8) = 4
    c: Distance(g5,g7) = 4
    c: Coincident(g9,g4)
    c: Parallel(g8,g6)
    c: Parallel(g7,g5)
    c: Perpendicular(g7,g8)
    c: Tangent(g8,g-3)
    c: Tangent(g2,g-4)
    c: PointOnObject(g11,g1)
    c: PointOnObject(g11,g0)
    c: Tangent(g1,g10) = -1.5708
    c: Tangent(g0,g10) = -1.5708
    c: PointOnObject(g13,g1)
    c: Tangent(g1,g12) = -1.5708
    c: Tangent(g2,g12) = -1.5708
    c: Equal(g10,g12)
    c: Coincident(g10,g5)
FEATURE [Part::Extrusion] Extrude072  label="Extrude perno per blocco switch"
  Base = -> Sketch067
  Dir = (0,-1,2e-16)
  DirMode = 2
  FaceMakerClass = Part::FaceMakerBullseye
  FaceMakerMode = 3
  LengthFwd = 25.2
  LengthRev = 0
  Solid = true
  Symmetric = true
FEATURE [Part::MultiFuse] Fusion
  Refine = true
  Shapes = -> [Extrude,Sweep,Extrude007,Extrude011,Extrude005,Extrude012,Extrude013,Extrude016,Extrude031,Extrude039,Extrude045,Extrude072]
FEATURE [Part::Cut] Cut
  Base = -> Fusion
  Refine = true
  Tool = -> Extrude001
FEATURE [Part::Cut] Cut001
  Base = -> Cut
  Refine = true
  Tool = -> Extrude004
FEATURE [Part::Cut] Cut002
  Base = -> Cut001
  Refine = true
  Tool = -> Extrude006
FEATURE [Part::Cut] Cut003
  Base = -> Cut002
  Refine = true
  Tool = -> Extrude008
FEATURE [Part::Cut] Cut004
  Base = -> Cut003
  Refine = true
  Tool = -> Extrude009
FEATURE [Part::Cut] Cut005
  Base = -> Cut004
  Refine = true
  Tool = -> Extrude010
FEATURE [Part::Cut] Cut006
  Base = -> Cut005
  Refine = true
  Tool = -> Extrude014
FEATURE [Part::Cut] Cut007
  Base = -> Cut006
  Refine = true
  Tool = -> Extrude015
FEATURE [Part::Cut] Cut008
  Base = -> Cut007
  Refine = true
  Tool = -> Extrude018
FEATURE [Part::Cut] Cut009
  Base = -> Cut008
  Refine = true
  Tool = -> Extrude019
FEATURE [Part::Cut] Cut010
  Base = -> Cut009
  Refine = true
  Tool = -> Extrude020
FEATURE [Part::Cut] Cut011
  Base = -> Cut010
  Refine = true
  Tool = -> Extrude021
FEATURE [Part::Cut] Cut012
  Base = -> Cut011
  Refine = true
  Tool = -> Extrude022
FEATURE [Part::Cut] Cut013
  Base = -> Cut012
  Refine = true
  Tool = -> Extrude023
FEATURE [Part::Cut] Cut014
  Base = -> Cut013
  Refine = true
  Tool = -> Extrude032
FEATURE [Part::Cut] Cut015
  Base = -> Cut014
  Refine = true
  Tool = -> Extrude033
FEATURE [Part::Cut] Cut016
  Base = -> Cut015
  Refine = true
  Tool = -> Extrude034
FEATURE [Part::Cut] Cut017
  Base = -> Cut016
  Refine = true
  Tool = -> Extrude035
FEATURE [Part::Cut] Cut018
  Base = -> Cut017
  Refine = true
  Tool = -> Extrude036
FEATURE [Part::Cut] Cut019
  Base = -> Cut018
  Refine = true
  Tool = -> Extrude037
FEATURE [Part::Cut] Cut020
  Base = -> Cut019
  Refine = true
  Tool = -> Extrude030
FEATURE [Part::Cut] Cut022
  Base = -> Cut020
  Refine = true
  Tool = -> Extrude038
FEATURE [Part::Cut] Cut023
  Base = -> Cut022
  Refine = true
  Tool = -> Extrude041
FEATURE [Part::Cut] Cut024
  Base = -> Cut023
  Refine = true
  Tool = -> Extrude040
FEATURE [Part::Cut] Cut025
  Base = -> Cut024
  Refine = true
  Tool = -> Extrude042
FEATURE [Part::Cut] Cut026
  Base = -> Cut025
  Refine = true
  Tool = -> Extrude043
FEATURE [Part::Cut] Cut027
  Base = -> Cut026
  Refine = true
  Tool = -> Extrude044
FEATURE [Part::Cut] Cut028
  Base = -> Cut027
  Refine = true
  Tool = -> Extrude046
FEATURE [Part::Cut] Cut029
  Base = -> Cut028
  Refine = true
  Tool = -> Extrude047
FEATURE [Part::Cut] Cut033
  Base = -> Cut029
  Refine = true
  Tool = -> Extrude055
FEATURE [Part::Cut] Cut034
  Base = -> Cut033
  Refine = true
  Tool = -> Extrude056
FEATURE [Part::Cut] Cut035
  Base = -> Cut034
  Refine = true
  Tool = -> Extrude057
FEATURE [Part::Cut] Cut037
  Base = -> Cut035
  Refine = true
  Tool = -> Extrude060
FEATURE [Part::Cut] Cut038
  Base = -> Cut037
  Refine = true
  Tool = -> Extrude061
FEATURE [Part::Cut] Cut039
  Base = -> Cut038
  Refine = true
  Tool = -> Extrude063
FEATURE [Part::Cut] Cut040
  Base = -> Cut039
  Refine = true
  Tool = -> Extrude064
FEATURE [Part::Cut] Cut041
  Base = -> Cut040
  Refine = true
  Tool = -> Extrude062
FEATURE [Sketcher::SketchObject] Sketch068  label="base con smusso sopra neopixel"
  ArcFitTolerance = 1e-06
  AttachmentSupport = -> [YZ_Plane002]
  FullyConstrained = true
  MakeInternals = false
  MapMode = 5
  Placement = pos=(0,0,0) rot=(0.57735,0.57735,0.57735;2.0944rad)
  sketch-geometry (5):
    g0: LineSegment StartX=-9.5 StartY=-6.1 StartZ=0 EndX=9.5 EndY=-6.1 EndZ=0
    g1: LineSegment StartX=9.5 StartY=-6.1 StartZ=0 EndX=9.5 EndY=6.1 EndZ=0
    g2: LineSegment StartX=9.5 StartY=6.1 StartZ=0 EndX=-9.5 EndY=6.1 EndZ=0
    g3: LineSegment StartX=-9.5 StartY=6.1 StartZ=0 EndX=-9.5 EndY=-6.1 EndZ=0
    g4: GeomPoint [constr] X=0 Y=0 Z=0
  constraints (12):
    c: Coincident(g0,g1)
    c: Coincident(g1,g2)
    c: Coincident(g2,g3)
    c: Coincident(g3,g0)
    c: Horizontal(g0)
    c: Horizontal(g2)
    c: Vertical(g1)
    c: Vertical(g3)
    c: Symmetric(g2,g0,g4)
    c: Distance(g1,g3) = 19
    c: Distance(g0,g2) = 12.2
    c: Coincident(g4,g-1)
FEATURE [Sketcher::SketchObject] Sketch069  label="cilindro minore"
  ArcFitTolerance = 1e-06
  AttachmentSupport = -> [XZ_Plane004]
  FullyConstrained = true
  MakeInternals = false
  MapMode = 5
  Placement = pos=(0,0,0) rot=(1,0,0;1.5708rad)
  sketch-geometry (1):
    g0: Circle CenterX=0 CenterY=0 CenterZ=0 NormalX=0 NormalY=0 NormalZ=1 AngleXU=0 Radius=5.8
  constraints (2):
    c: Diameter(g0) = 11.6
    c: Coincident(g0,g-1)
FEATURE [Sketcher::SketchObject] Sketch070  label="cilindro maggiore"
  ArcFitTolerance = 1e-06
  AttachmentSupport = -> [XZ_Plane004]
  ExternalGeometry = -> [Sketch069]
  FullyConstrained = true
  MakeInternals = false
  MapMode = 5
  Placement = pos=(0,0,0) rot=(1,0,0;1.5708rad)
  sketch-geometry (1):
    g0: Circle CenterX=0 CenterY=0 CenterZ=0 NormalX=0 NormalY=0 NormalZ=1 AngleXU=0 Radius=6.5
  constraints (2):
    c: Coincident(g0,g-1)
    c: Diameter(g0) = 13
FEATURE [Sketcher::SketchObject] Sketch071  label="buco interno"
  ArcFitTolerance = 1e-06
  AttachmentSupport = -> [XZ_Plane004]
  ExternalGeometry = -> [Sketch069]
  FullyConstrained = true
  MakeInternals = false
  MapMode = 5
  Placement = pos=(0,0,0) rot=(1,0,0;1.5708rad)
  sketch-geometry (1):
    g0: Circle CenterX=0 CenterY=0 CenterZ=0 NormalX=0 NormalY=0 NormalZ=1 AngleXU=0 Radius=5
  constraints (2):
    c: Coincident(g0,g-1)
    c: Diameter(g0) = 10
FEATURE [PartDesign::Pad] Pad
  Direction = (0,-1,2e-16)
  Length = 1.2
  Length2 = 10
  Placement = pos=(0,0,0) rot=(1,0,0;1.5708rad)
  Profile = -> Sketch070
  ReferenceAxis = -> Sketch070 [N_Axis]
  Refine = true
  Suppressed = false
  Type = 0
FEATURE [PartDesign::Pad] Pad001
  BaseFeature = -> Pad
  Direction = (0,-1,2e-16)
  Length = 5.6
  Length2 = 10
  Placement = pos=(0,0,0) rot=(1,0,0;1.5708rad)
  Profile = -> Sketch069
  ReferenceAxis = -> Sketch069 [N_Axis]
  Refine = true
  Suppressed = false
  Type = 0
FEATURE [PartDesign::Pocket] Pocket
  BaseFeature = -> Pad001
  Direction = (0,1,-2e-16)
  Length = 7
  Length2 = 5
  Midplane = true
  Placement = pos=(0,0,0) rot=(1,0,0;1.5708rad)
  Profile = -> Sketch071
  ReferenceAxis = -> Sketch071 [N_Axis]
  Refine = true
  Suppressed = false
  Type = 0
FEATURE [PartDesign::Fillet] Fillet
  Base = -> Pocket [Face7]
  BaseFeature = -> Pocket
  Placement = pos=(0,0,0) rot=(1,0,0;1.5708rad)
  Radius = 1
  Refine = true
  SupportTransform = false
  Suppressed = false
  UseAllEdges = false
FEATURE [PartDesign::Body] Body004  label="pulsanti lato sinistro"
  AllowCompound = false
  Group = -> [Sketch069,Sketch070,Sketch071,Pad,Pad001,Pocket,Fillet]
  Origin = -> Origin004
  Tip = -> Fillet
FEATURE [Sketcher::SketchObject] Sketch072  label="buco per saldature e diodo driver solenoide"
  ArcFitTolerance = 1e-06
  AttachmentSupport = -> [XZ_Plane]
  ExternalGeometry = -> [Sketch038]
  FullyConstrained = true
  MakeInternals = false
  MapMode = 5
  Placement = pos=(0,0,0) rot=(1,0,0;1.5708rad)
  sketch-geometry (4):
    g0: LineSegment StartX=-209.225 StartY=-40.6939 StartZ=0 EndX=-204.154 EndY=-29.8182 EndZ=0
    g1: LineSegment StartX=-204.154 StartY=-29.8182 StartZ=0 EndX=-206.51 EndY=-28.7194 EndZ=0
    g2: LineSegment StartX=-206.51 StartY=-28.7194 StartZ=0 EndX=-211.582 EndY=-39.5951 EndZ=0
    g3: LineSegment StartX=-211.582 StartY=-39.5951 StartZ=0 EndX=-209.225 EndY=-40.6939 EndZ=0
  constraints (11):
    c: Coincident(g1,g0)
    c: Coincident(g2,g1)
    c: Coincident(g3,g2)
    c: Coincident(g3,g0)
    c: Parallel(g-3,g0)
    c: Parallel(g0,g2)
    c: Perpendicular(g0,g3)
    c: Perpendicular(g1,g0)
    c: Distance(g3) = 2.6
    c: Distance(g2) = 12
    c: Coincident(g0,g-3)
FEATURE [Part::Extrusion] Extrude074  label="Extrude buco per saldature e diodo driver solenoide"
  Base = -> Sketch072
  Dir = (0,-1,2e-16)
  DirMode = 2
  FaceMakerClass = Part::FaceMakerBullseye
  FaceMakerMode = 3
  LengthFwd = 14.6
  LengthRev = 0
  Solid = true
  Symmetric = true
FEATURE [Part::Cut] Cut042
  Base = -> Cut041
  Refine = true
  Tool = -> Extrude074
FEATURE [Sketcher::SketchObject] Sketch073  label="fori slargati blocco solenoide"
  ArcFitTolerance = 1e-06
  AttachmentSupport = -> [XY_Plane]
  ExternalGeometry = -> [Sketch030]
  FullyConstrained = true
  MakeInternals = false
  MapMode = 5
  sketch-geometry (2):
    g0: Circle CenterX=-152.209 CenterY=6.95 CenterZ=0 NormalX=0 NormalY=0 NormalZ=1 AngleXU=0 Radius=3.7
    g1: Circle CenterX=-130.41 CenterY=-6.95 CenterZ=0 NormalX=0 NormalY=0 NormalZ=1 AngleXU=0 Radius=3.7
  constraints (4):
    c: Diameter(g0) = 7.4
    c: Coincident(g0,g-3)
    c: Diameter(g1) = 7.4
    c: Coincident(g1,g-4)
FEATURE [Part::Extrusion] Extrude075  label="Extrude fori slargati blocco solenoide"
  Base = -> Sketch073
  Dir = (0,0,1)
  DirMode = 2
  FaceMakerClass = Part::FaceMakerBullseye
  FaceMakerMode = 3
  LengthFwd = 1.5
  LengthRev = 0
  Placement = pos=(0,0,36.4) rot=(0,0,1;0rad)
  Solid = true
  Symmetric = false
FEATURE [Part::Cut] Cut043
  Base = -> Cut042
  Refine = true
  Tool = -> Extrude075
FEATURE [Sketcher::SketchObject] Sketch074  label="lato sx pistola"
  ArcFitTolerance = 1e-06
  AttachmentSupport = -> [XZ_Plane]
  ExternalGeometry = -> [Sketch016,Sketch,Sketch058]
  FullyConstrained = true
  MakeInternals = false
  MapMode = 5
  Placement = pos=(0,0,0) rot=(1,0,0;1.5708rad)
  sketch-geometry (37):
    g0: LineSegment StartX=-82.8 StartY=3.2 StartZ=0 EndX=0 EndY=3.2 EndZ=0
    g1: LineSegment StartX=-82.8 StartY=3.2 StartZ=0 EndX=-82.8 EndY=6.2 EndZ=0
    g2: LineSegment [constr] StartX=-107.6 StartY=18 StartZ=0 EndX=-107.6 EndY=20 EndZ=0
    g3: LineSegment [constr] StartX=-132.428 StartY=18 StartZ=0 EndX=-132.428 EndY=20 EndZ=0
    g4: LineSegment StartX=-132.428 StartY=20 StartZ=0 EndX=-107.6 EndY=20 EndZ=0
    g5: ArcOfCircle CenterX=-107.6 CenterY=4 CenterZ=0 NormalX=0 NormalY=0 NormalZ=1 AngleXU=0 Radius=16 StartAngle=0.137937 EndAngle=1.5708
    g6: LineSegment StartX=-82.8 StartY=6.2 StartZ=0 EndX=-91.752 EndY=6.2 EndZ=0
    g7: LineSegment [constr] StartX=-145.743 StartY=8.32624 StartZ=0 EndX=-147.645 EndY=8.94427 EndZ=0
    g8: ArcOfCircle CenterX=-132.428 CenterY=4 CenterZ=0 NormalX=0 NormalY=0 NormalZ=1 AngleXU=0 Radius=16 StartAngle=1.5708 EndAngle=2.82743
    g9: LineSegment StartX=-215.932 StartY=-80.4316 StartZ=0 EndX=-176.685 EndY=-80.4316 EndZ=0
    g10: LineSegment StartX=-147.645 StartY=8.94427 StartZ=0 EndX=-176.685 EndY=-80.4316 EndZ=0
    g11: LineSegment [constr] StartX=-193.988 StartY=-2.33927 StartZ=0 EndX=-192.176 EndY=-3.18451 EndZ=0
    g12: LineSegment [constr] StartX=-217.232 StartY=-52.1862 StartZ=0 EndX=-215.42 EndY=-53.0314 EndZ=0
    g13: LineSegment StartX=-192.176 StartY=-3.18451 StartZ=0 EndX=-215.42 EndY=-53.0314 EndZ=0
    g14: ArcOfCircle CenterX=-184.801 CenterY=-67.3089 CenterZ=0 NormalX=0 NormalY=0 NormalZ=1 AngleXU=0 Radius=33.7833 StartAngle=2.70526 EndAngle=3.54053
    g15: ArcOfCircle CenterX=-207.583 CenterY=4 CenterZ=0 NormalX=0 NormalY=0 NormalZ=1 AngleXU=0 Radius=17 StartAngle=5.84685 EndAngle=7.56663
    g16: LineSegment StartX=-202.765 StartY=20.303 StartZ=0 EndX=-195.887 EndY=39.2 EndZ=0
    g17: LineSegment [constr] StartX=-193.885 StartY=33.0037 StartZ=0 EndX=-197.644 EndY=34.3718 EndZ=0
    g18: LineSegment StartX=-195.887 StartY=39.2 StartZ=0 EndX=0 EndY=39.2 EndZ=0
    g19: LineSegment StartX=0 StartY=3.2 StartZ=0 EndX=0 EndY=39.2 EndZ=0
    g20: LineSegment StartX=-189.939 StartY=31.5672 StartZ=0 EndX=-192.333 EndY=24.9893 EndZ=0
    g21: LineSegment StartX=-196.467 StartY=26.4942 StartZ=0 EndX=-194.073 EndY=33.0721 EndZ=0
    g22: Circle CenterX=-213.443 CenterY=-76.8316 CenterZ=0 NormalX=0 NormalY=0 NormalZ=1 AngleXU=0 Radius=1.8
    g23: Circle CenterX=-179.305 CenterY=-76.8316 CenterZ=0 NormalX=0 NormalY=0 NormalZ=1 AngleXU=0 Radius=1.8
    g24: Circle CenterX=-184.08 CenterY=34.8 CenterZ=0 NormalX=0 NormalY=0 NormalZ=1 AngleXU=0 Radius=1.8
    g25: Circle CenterX=-78.51 CenterY=34.8 CenterZ=0 NormalX=0 NormalY=0 NormalZ=1 AngleXU=0 Radius=1.8
    g26: Circle CenterX=-78.51 CenterY=7.6 CenterZ=0 NormalX=0 NormalY=0 NormalZ=1 AngleXU=0 Radius=1.8
    g27: Circle CenterX=-5.6 CenterY=34.8 CenterZ=0 NormalX=0 NormalY=0 NormalZ=1 AngleXU=0 Radius=1.8
    g28: Circle CenterX=-5.6 CenterY=7.6 CenterZ=0 NormalX=0 NormalY=0 NormalZ=1 AngleXU=0 Radius=1.8
    g29: LineSegment StartX=-190.127 StartY=31.6356 StartZ=0 EndX=-189.939 EndY=31.5672 EndZ=0
    g30: LineSegment StartX=-194.073 StartY=33.0721 StartZ=0 EndX=-193.885 EndY=33.0037 EndZ=0
    g31: LineSegment StartX=-193.885 StartY=33.0037 StartZ=0 EndX=-190.127 EndY=31.6356 EndZ=0
    g32: LineSegment StartX=-196.467 StartY=26.4942 StartZ=0 EndX=-192.333 EndY=24.9893 EndZ=0
    g33: Circle CenterX=-19 CenterY=21.2 CenterZ=0 NormalX=0 NormalY=0 NormalZ=1 AngleXU=0 Radius=6.3
    g34: Circle CenterX=-42 CenterY=21.2 CenterZ=0 NormalX=0 NormalY=0 NormalZ=1 AngleXU=0 Radius=6.3
    g35: Circle CenterX=-65 CenterY=21.2 CenterZ=0 NormalX=0 NormalY=0 NormalZ=1 AngleXU=0 Radius=6.3
    g36: LineSegment [constr] StartX=-4 StartY=21.2 StartZ=0 EndX=-65 EndY=21.2 EndZ=0
  constraints (96):
    c: Coincident(g0,g-41)
    c: Horizontal(g0)
    c: PointOnObject(g0,g-39)
    c: Coincident(g1,g0)
    c: Vertical(g1)
    c: DistanceY(g1,g1) = 3
    c: Coincident(g2,g-17)
    c: Vertical(g2)
    c: Coincident(g3,g-16)
    c: Vertical(g3)
    c: DistanceY(g2,g2) = 2
    c: DistanceY(g3,g3) = 2
    c: Coincident(g4,g3)
    c: Coincident(g4,g2)
    c: Coincident(g5,g-17)
    c: Coincident(g5,g2)
    c: Coincident(g6,g1)
    c: Horizontal(g6)
    c: Coincident(g6,g5)
    c: Coincident(g7,g-15)
    c: Coincident(g8,g7)
    c: Coincident(g8,g3)
    c: Coincident(g8,g-15)
    c: Horizontal(g9)
    c: DistanceY(g-13,g9) = 2
    c: Coincident(g10,g7)
    c: Parallel(g10,g-14)
    c: Coincident(g9,g10)
    c: Distance(g11) = 2
    c: Coincident(g11,g-11)
    c: Perpendicular(g-11,g11)
    c: Distance(g12) = 2
    c: Coincident(g12,g-12)
    c: Perpendicular(g-11,g12)
    c: Coincident(g13,g11)
    c: Coincident(g13,g12)
    c: Coincident(g14,g-32)
    c: Coincident(g14,g12)
    c: Coincident(g14,g9)
    c: Coincident(g15,g-10)
    c: Coincident(g15,g11)
    c: Parallel(g16,g-22)
    c: Distance(g17) = 4
    c: PointOnObject(g17,g16)
    c: Coincident(g15,g16)
    c: Horizontal(g18)
    c: Coincident(g18,g16)
    c: Coincident(g19,g0)
    c: PointOnObject(g19,g-39)
    c: DistanceY(g19,g-36) = 2
    c: Coincident(g18,g19)
    c: Diameter(g22) = 3.6
    c: Coincident(g22,g-9)
    c: Diameter(g23) = 3.6
    c: Coincident(g23,g-8)
    c: Diameter(g24) = 3.6
    c: Diameter(g25) = 3.6
    c: Diameter(g26) = 3.6
    c: Diameter(g27) = 3.6
    c: Diameter(g28) = 3.6
    c: Coincident(g27,g-4)
    c: Coincident(g28,g-3)
    c: Coincident(g25,g-6)
    c: Coincident(g26,g-5)
    c: Coincident(g24,g-7)
    c: Parallel(g20,g-21)
    c: Equal(g20,g-21)
    c: Parallel(g21,g-19)
    c: Equal(g21,g-19)
    c: Distance(g29) = 0.2
    c: Distance(g30) = 0.2
    c: Parallel(g29,g-20)
    c: Parallel(g31,g-20)
    c: Equal(g31,g-20)
    c: Coincident(g30,g31)
    c: Coincident(g31,g29)
    c: Coincident(g29,g-21)
    c: Parallel(g30,g31)
    c: Coincident(g17,g30)
    c: Coincident(g20,g29)
    c: Coincident(g21,g30)
    c: Perpendicular(g16,g17)
    c: Coincident(g32,g21)
    c: Coincident(g32,g20)
    c: Perpendicular(g10,g7)
    c: Diameter(g33) = 12.6
    c: Diameter(g34) = 12.6
    c: Diameter(g35) = 12.6
    c: Horizontal(g36)
    c: PointOnObject(g33,g36)
    c: PointOnObject(g34,g36)
    c: DistanceX(g34,g33) = 23
    c: DistanceX(g35,g34) = 23
    c: DistanceX(g33,g36) = 15
    c: Symmetric(g-24,g-24,g36)
    c: Coincident(g36,g35)
FEATURE [Sketcher::SketchObject] Sketch075  label="lato dx pistola"
  ArcFitTolerance = 1e-06
  AttachmentSupport = -> [XZ_Plane]
  ExternalGeometry = -> [Sketch016,Sketch,Sketch058,Sketch074]
  FullyConstrained = true
  MakeInternals = false
  MapMode = 5
  Placement = pos=(0,0,0) rot=(1,0,0;1.5708rad)
  sketch-geometry (61):
    g0: LineSegment StartX=-82.8 StartY=3.2 StartZ=0 EndX=0 EndY=3.2 EndZ=0
    g1: LineSegment StartX=-82.8 StartY=3.2 StartZ=0 EndX=-82.8 EndY=6.2 EndZ=0
    g2: LineSegment [constr] StartX=-107.6 StartY=18 StartZ=0 EndX=-107.6 EndY=20 EndZ=0
    g3: LineSegment [constr] StartX=-132.428 StartY=18 StartZ=0 EndX=-132.428 EndY=20 EndZ=0
    g4: LineSegment StartX=-132.428 StartY=20 StartZ=0 EndX=-107.6 EndY=20 EndZ=0
    g5: ArcOfCircle CenterX=-107.6 CenterY=4 CenterZ=0 NormalX=0 NormalY=0 NormalZ=1 AngleXU=0 Radius=16 StartAngle=0.137937 EndAngle=1.5708
    g6: LineSegment StartX=-82.8 StartY=6.2 StartZ=0 EndX=-91.752 EndY=6.2 EndZ=0
    g7: LineSegment [constr] StartX=-145.743 StartY=8.32624 StartZ=0 EndX=-147.645 EndY=8.94427 EndZ=0
    g8: ArcOfCircle CenterX=-132.428 CenterY=4 CenterZ=0 NormalX=0 NormalY=0 NormalZ=1 AngleXU=0 Radius=16 StartAngle=1.5708 EndAngle=2.82743
    g9: LineSegment StartX=-215.932 StartY=-80.4316 StartZ=0 EndX=-176.685 EndY=-80.4316 EndZ=0
    g10: LineSegment StartX=-147.645 StartY=8.94427 StartZ=0 EndX=-176.685 EndY=-80.4316 EndZ=0
    g11: LineSegment [constr] StartX=-193.988 StartY=-2.33927 StartZ=0 EndX=-192.176 EndY=-3.18451 EndZ=0
    g12: LineSegment [constr] StartX=-217.232 StartY=-52.1862 StartZ=0 EndX=-215.42 EndY=-53.0314 EndZ=0
    g13: LineSegment StartX=-192.176 StartY=-3.18451 StartZ=0 EndX=-215.42 EndY=-53.0314 EndZ=0
    g14: ArcOfCircle CenterX=-184.801 CenterY=-67.3089 CenterZ=0 NormalX=0 NormalY=0 NormalZ=1 AngleXU=0 Radius=33.7833 StartAngle=2.70526 EndAngle=3.54053
    g15: ArcOfCircle CenterX=-207.583 CenterY=4 CenterZ=0 NormalX=0 NormalY=0 NormalZ=1 AngleXU=0 Radius=17 StartAngle=5.84685 EndAngle=7.56663
    g16: LineSegment StartX=-202.765 StartY=20.303 StartZ=0 EndX=-195.887 EndY=39.2 EndZ=0
    g17: LineSegment [constr] StartX=-193.885 StartY=33.0037 StartZ=0 EndX=-197.644 EndY=34.3718 EndZ=0
    g18: LineSegment StartX=-195.887 StartY=39.2 StartZ=0 EndX=0 EndY=39.2 EndZ=0
    g19: LineSegment StartX=0 StartY=3.2 StartZ=0 EndX=0 EndY=39.2 EndZ=0
    g20: LineSegment StartX=-189.939 StartY=31.5672 StartZ=0 EndX=-192.333 EndY=24.9893 EndZ=0
    g21: LineSegment StartX=-196.467 StartY=26.4942 StartZ=0 EndX=-194.073 EndY=33.0721 EndZ=0
    g22: Circle CenterX=-213.443 CenterY=-76.8316 CenterZ=0 NormalX=0 NormalY=0 NormalZ=1 AngleXU=0 Radius=1.8
    g23: Circle CenterX=-179.305 CenterY=-76.8316 CenterZ=0 NormalX=0 NormalY=0 NormalZ=1 AngleXU=0 Radius=1.8
    g24: Circle CenterX=-184.08 CenterY=34.8 CenterZ=0 NormalX=0 NormalY=0 NormalZ=1 AngleXU=0 Radius=1.8
    g25: Circle CenterX=-78.51 CenterY=34.8 CenterZ=0 NormalX=0 NormalY=0 NormalZ=1 AngleXU=0 Radius=1.8
    g26: Circle CenterX=-78.51 CenterY=7.6 CenterZ=0 NormalX=0 NormalY=0 NormalZ=1 AngleXU=0 Radius=1.8
    g27: Circle CenterX=-5.6 CenterY=34.8 CenterZ=0 NormalX=0 NormalY=0 NormalZ=1 AngleXU=0 Radius=1.8
    g28: Circle CenterX=-5.6 CenterY=7.6 CenterZ=0 NormalX=0 NormalY=0 NormalZ=1 AngleXU=0 Radius=1.8
    g29: LineSegment StartX=-190.127 StartY=31.6356 StartZ=0 EndX=-189.939 EndY=31.5672 EndZ=0
    g30: LineSegment StartX=-194.073 StartY=33.0721 StartZ=0 EndX=-193.885 EndY=33.0037 EndZ=0
    g31: LineSegment StartX=-193.885 StartY=33.0037 StartZ=0 EndX=-190.127 EndY=31.6356 EndZ=0
    g32: LineSegment StartX=-196.467 StartY=26.4942 StartZ=0 EndX=-192.333 EndY=24.9893 EndZ=0
    g33: LineSegment [constr] StartX=-4 StartY=21.2 StartZ=0 EndX=-87.91 EndY=21.2 EndZ=0
    g34: GeomPoint [constr] X=-4 Y=21.2 Z=0
    g35: LineSegment [constr] StartX=-15.2 StartY=33.7 StartZ=0 EndX=-15.2 EndY=8.7 EndZ=0
    g36: LineSegment [constr] StartX=-15.2 StartY=33.7 StartZ=0 EndX=-56.2 EndY=33.7 EndZ=0
    g37: LineSegment [constr] StartX=-15.2 StartY=8.7 StartZ=0 EndX=-56.2 EndY=8.7 EndZ=0
    g38: LineSegment [constr] StartX=-56.2 StartY=33.7 StartZ=0 EndX=-56.2 EndY=8.7 EndZ=0
    g39: Circle CenterX=-18.6 CenterY=30.3 CenterZ=0 NormalX=0 NormalY=0 NormalZ=1 AngleXU=0 Radius=3.4
    g40: Circle CenterX=-18.6 CenterY=12.1 CenterZ=0 NormalX=0 NormalY=0 NormalZ=1 AngleXU=0 Radius=3.4
    g41: Circle CenterX=-43.2 CenterY=30.3 CenterZ=0 NormalX=0 NormalY=0 NormalZ=1 AngleXU=0 Radius=3.4
    g42: Circle CenterX=-43.2 CenterY=12.1 CenterZ=0 NormalX=0 NormalY=0 NormalZ=1 AngleXU=0 Radius=3.4
    g43: LineSegment [constr] StartX=-4 StartY=21.2 StartZ=0 EndX=-15.2 EndY=21.2 EndZ=0
    g44: LineSegment [constr] StartX=-15.2 StartY=21.2 StartZ=0 EndX=-36.2 EndY=21.2 EndZ=0
    g45: LineSegment [constr] StartX=-41.5 StartY=16.2 StartZ=0 EndX=-30.9 EndY=16.2 EndZ=0
    g46: LineSegment [constr] StartX=-30.9 StartY=16.2 StartZ=0 EndX=-30.9 EndY=26.2 EndZ=0
    g47: LineSegment [constr] StartX=-30.9 StartY=26.2 StartZ=0 EndX=-41.5 EndY=26.2 EndZ=0
    g48: LineSegment [constr] StartX=-41.5 StartY=26.2 StartZ=0 EndX=-41.5 EndY=16.2 EndZ=0
    g49: GeomPoint [constr] X=-36.2 Y=21.2 Z=0
    g50: Circle CenterX=-36.2 CenterY=21.2 CenterZ=0 NormalX=0 NormalY=0 NormalZ=1 AngleXU=0 Radius=2.8
    g51: LineSegment [constr] StartX=-24.2 StartY=26.7 StartZ=0 EndX=-24.2 EndY=15.7 EndZ=0
    g52: Circle CenterX=-24.2 CenterY=26.7 CenterZ=0 NormalX=0 NormalY=0 NormalZ=1 AngleXU=0 Radius=3
    g53: Circle CenterX=-24.2 CenterY=15.7 CenterZ=0 NormalX=0 NormalY=0 NormalZ=1 AngleXU=0 Radius=3
    g54: GeomPoint X=-18.6 Y=30.3 Z=0
    g55: GeomPoint X=-18.6 Y=12.1 Z=0
    g56: GeomPoint X=-43.2 Y=12.1 Z=0
    g57: GeomPoint X=-43.2 Y=30.3 Z=0
    g58: Circle CenterX=-65 CenterY=21.2 CenterZ=0 NormalX=0 NormalY=0 NormalZ=1 AngleXU=0 Radius=1.5
    g59: Circle CenterX=-42 CenterY=21.2 CenterZ=0 NormalX=0 NormalY=0 NormalZ=1 AngleXU=0 Radius=1.5
    g60: Circle CenterX=-19 CenterY=21.2 CenterZ=0 NormalX=0 NormalY=0 NormalZ=1 AngleXU=0 Radius=1.5
  constraints (149):
    c: Coincident(g0,g-41)
    c: Horizontal(g0)
    c: PointOnObject(g0,g-39)
    c: Coincident(g1,g0)
    c: Vertical(g1)
    c: DistanceY(g1,g1) = 3
    c: Coincident(g2,g-17)
    c: Vertical(g2)
    c: Coincident(g3,g-16)
    c: Vertical(g3)
    c: DistanceY(g2,g2) = 2
    c: DistanceY(g3,g3) = 2
    c: Coincident(g4,g3)
    c: Coincident(g4,g2)
    c: Coincident(g5,g-17)
    c: Coincident(g5,g2)
    c: Coincident(g6,g1)
    c: Horizontal(g6)
    c: Coincident(g6,g5)
    c: Coincident(g7,g-15)
    c: Coincident(g8,g7)
    c: Coincident(g8,g3)
    c: Coincident(g8,g-15)
    c: Horizontal(g9)
    c: DistanceY(g-13,g9) = 2
    c: Coincident(g10,g7)
    c: Parallel(g10,g-14)
    c: Coincident(g9,g10)
    c: Distance(g11) = 2
    c: Coincident(g11,g-11)
    c: Perpendicular(g-11,g11)
    c: Distance(g12) = 2
    c: Coincident(g12,g-12)
    c: Perpendicular(g-11,g12)
    c: Coincident(g13,g11)
    c: Coincident(g13,g12)
    c: Coincident(g14,g-32)
    c: Coincident(g14,g12)
    c: Coincident(g14,g9)
    c: Coincident(g15,g-10)
    c: Coincident(g15,g11)
    c: Parallel(g16,g-22)
    c: Distance(g17) = 4
    c: PointOnObject(g17,g16)
    c: Coincident(g15,g16)
    c: Horizontal(g18)
    c: Coincident(g18,g16)
    c: Coincident(g19,g0)
    c: PointOnObject(g19,g-39)
    c: DistanceY(g19,g-36) = 2
    c: Coincident(g18,g19)
    c: Diameter(g22) = 3.6
    c: Coincident(g22,g-9)
    c: Diameter(g23) = 3.6
    c: Coincident(g23,g-8)
    c: Diameter(g24) = 3.6
    c: Diameter(g25) = 3.6
    c: Diameter(g26) = 3.6
    c: Diameter(g27) = 3.6
    c: Diameter(g28) = 3.6
    c: Coincident(g27,g-4)
    c: Coincident(g28,g-3)
    c: Coincident(g25,g-6)
    c: Coincident(g26,g-5)
    c: Coincident(g24,g-7)
    c: Parallel(g20,g-21)
    c: Equal(g20,g-21)
    c: Parallel(g21,g-19)
    c: Equal(g21,g-19)
    c: Distance(g29) = 0.2
    c: Distance(g30) = 0.2
    c: Parallel(g29,g-20)
    c: Parallel(g31,g-20)
    c: Equal(g31,g-20)
    c: Coincident(g30,g31)
    c: Coincident(g31,g29)
    c: Coincident(g29,g-21)
    c: Parallel(g30,g31)
    c: Coincident(g17,g30)
    c: Coincident(g20,g29)
    c: Coincident(g21,g30)
    c: Perpendicular(g16,g17)
    c: Coincident(g32,g21)
    c: Coincident(g32,g20)
    c: Perpendicular(g10,g7)
    c: Horizontal(g33)
    c: Symmetric(g-24,g-24,g33)
    c: PointOnObject(g33,g-28)
    c: Symmetric(g-24,g-24,g34)
    c: DistanceY(g35,g35) = 25
    c: Symmetric(g35,g35,g33)
    c: Distance(g36) = 41
    c: Coincident(g36,g35)
    c: Horizontal(g36)
    c: Coincident(g37,g35)
    c: Horizontal(g37)
    c: Coincident(g38,g36)
    c: Vertical(g38)
    c: Coincident(g37,g38)
    c: Diameter(g39) = 6.8
    c: Diameter(g40) = 6.8
    c: Tangent(g39,g36)
    c: Tangent(g40,g37)
    c: Tangent(g39,g35)
    c: Tangent(g40,g35)
    c: Diameter(g41) = 6.8
    c: Diameter(g42) = 6.8
    c: Tangent(g41,g36)
    c: Tangent(g42,g37)
    c: DistanceX(g41,g39) = 24.6
    c: DistanceX(g42,g40) = 24.6
    c: Distance(g43) = 11.2
    c: Coincident(g43,g33)
    c: PointOnObject(g43,g33)
    c: PointOnObject(g43,g35)
    c: Distance(g44) = 21
    c: Coincident(g44,g43)
    c: PointOnObject(g44,g33)
    c: Coincident(g45,g46)
    c: Coincident(g46,g47)
    c: Coincident(g47,g48)
    c: Coincident(g48,g45)
    c: Horizontal(g45)
    c: Horizontal(g47)
    c: Vertical(g46)
    c: Vertical(g48)
    c: Symmetric(g47,g45,g49)
    c: Distance(g46,g48) = 10.6
    c: Distance(g45,g47) = 10
    c: Coincident(g49,g44)
    c: Diameter(g50) = 5.6
    c: Coincident(g50,g44)
    c: Distance(g51) = 11
    c: Symmetric(g51,g51,g33)
    c: DistanceX(g51,g43) = 9
    c: Diameter(g52) = 6
    c: Coincident(g52,g51)
    c: Diameter(g53) = 6
    c: Coincident(g53,g51)
    c: Coincident(g40,g55)
    c: Coincident(g39,g54)
    c: Coincident(g41,g57)
    c: Coincident(g42,g56)
    c: Diameter(g58) = 3
    c: Diameter(g59) = 3
    c: Diameter(g60) = 3
    c: Coincident(g58,g-44)
    c: Coincident(g59,g-46)
    c: Coincident(g60,g-45)
FEATURE [Sketcher::SketchObject] Sketch078
  ArcFitTolerance = 1e-06
  AttachmentSupport = -> [XZ_Plane005]
  FullyConstrained = true
  MakeInternals = false
  MapMode = 5
  Placement = pos=(0,0,0) rot=(1,0,0;1.5708rad)
  sketch-geometry (5):
    g0: LineSegment [constr] StartX=0 StartY=5.5 StartZ=0 EndX=0 EndY=-5.5 EndZ=0
    g1: ArcOfCircle CenterX=0 CenterY=5.5 CenterZ=0 NormalX=0 NormalY=0 NormalZ=1 AngleXU=0 Radius=2.7 StartAngle=0 EndAngle=3.14159
    g2: ArcOfCircle CenterX=0 CenterY=-5.5 CenterZ=0 NormalX=0 NormalY=0 NormalZ=1 AngleXU=0 Radius=2.7 StartAngle=3.1416 EndAngle=6.28318
    g3: LineSegment StartX=-2.7 StartY=5.5 StartZ=0 EndX=-2.7 EndY=-5.50001 EndZ=0
    g4: LineSegment StartX=2.7 StartY=5.5 StartZ=0 EndX=2.7 EndY=-5.50001 EndZ=0
  constraints (13):
    c: Distance(g0) = 11
    c: Vertical(g0)
    c: Symmetric(g0,g0,g-1)
    c: Radius(g1) = 2.7
    c: Coincident(g1,g0)
    c: Radius(g2) = 2.7
    c: Coincident(g2,g0)
    c: Vertical(g3)
    c: Vertical(g4)
    c: Coincident(g2,g4)
    c: Coincident(g2,g3)
    c: Tangent(g3,g1) = -1.5708
    c: Tangent(g4,g1) = 1.5708
FEATURE [PartDesign::Pad] Pad002
  Direction = (0,-1,2e-16)
  Length = 0.8
  Length2 = 10
  Placement = pos=(0,0,0) rot=(1,0,0;1.5708rad)
  Profile = -> Sketch078
  ReferenceAxis = -> Sketch078 [N_Axis]
  Refine = true
  Suppressed = false
  Type = 0
FEATURE [Sketcher::SketchObject] Sketch079
  ArcFitTolerance = 1e-06
  AttachmentSupport = -> [XZ_Plane005]
  ExternalGeometry = -> [Sketch078]
  FullyConstrained = true
  MakeInternals = false
  MapMode = 5
  Placement = pos=(0,0,0) rot=(1,0,0;1.5708rad)
  sketch-geometry (2):
    g0: Circle CenterX=-1e-16 CenterY=5.5 CenterZ=0 NormalX=0 NormalY=0 NormalZ=1 AngleXU=0 Radius=2.7
    g1: Circle CenterX=0 CenterY=-5.5 CenterZ=0 NormalX=0 NormalY=0 NormalZ=1 AngleXU=0 Radius=2.7
  constraints (4):
    c: Coincident(g0,g-3)
    c: PointOnObject(g-3,g0)
    c: Coincident(g1,g-4)
    c: Equal(g1,g-4)
FEATURE [PartDesign::Pad] Pad003
  BaseFeature = -> Pad002
  Direction = (0,-1,2e-16)
  Length = 5
  Length2 = 10
  Placement = pos=(0,0,0) rot=(1,0,0;1.5708rad)
  Profile = -> Sketch079
  ReferenceAxis = -> Sketch079 [N_Axis]
  Refine = true
  Suppressed = false
  Type = 0
FEATURE [PartDesign::Fillet] Fillet001
  Base = -> Pad003 [Edge16,Edge14]
  BaseFeature = -> Pad003
  Placement = pos=(0,0,0) rot=(1,0,0;1.5708rad)
  Radius = 0.4
  Refine = true
  SupportTransform = false
  Suppressed = false
  UseAllEdges = false
FEATURE [PartDesign::Body] Body005  label="pulsanti lato destro"
  AllowCompound = false
  Group = -> [Sketch078,Pad002,Sketch079,Pad003,Fillet001]
  Origin = -> Origin005
  Tip = -> Fillet001
FEATURE [PartDesign::SubShapeBinder] Binder
  BindCopyOnChange = 0
  BindMode = 0
  ClaimChildren = false
  Context = -> Body006 [Binder.]
  Fuse = false
  MakeFace = true
  OffsetFill = false
  OffsetIntersection = false
  OffsetJoinType = 0
  OffsetOpenResult = false
  PartialLoad = false
  Refine = true
  Relative = true
  Support = -> [Body[Sketch074.]]
  _Version = 2
FEATURE [PartDesign::SubShapeBinder] Binder001
  BindCopyOnChange = 0
  BindMode = 0
  ClaimChildren = false
  Context = -> Body007 [Binder001.]
  Fuse = false
  MakeFace = true
  OffsetFill = false
  OffsetIntersection = false
  OffsetJoinType = 0
  OffsetOpenResult = false
  PartialLoad = false
  Refine = true
  Relative = true
  Support = -> [Body[Sketch075.]]
  _Version = 2
FEATURE [Mesh::Feature] logo_per_PCB_definitivo_positivo
  Placement = pos=(-191,17,-66) rot=(0,1,1;0rad)
FEATURE [Sketcher::SketchObject] Sketch114  label="Sketch114 - base lato DX"
  ArcFitTolerance = 1e-06
  AttachmentSupport = -> [Binder001]
  ExternalGeometry = -> [Binder001]
  FullyConstrained = true
  MakeInternals = false
  MapMode = 5
  Placement = pos=(0,1e-15,0) rot=(0,0.707107,0.707107;3.14159rad)
  sketch-geometry (30):
    g0: Circle CenterX=5.6 CenterY=34.8 CenterZ=0 NormalX=0 NormalY=0 NormalZ=1 AngleXU=0 Radius=1.8
    g1: Circle CenterX=5.6 CenterY=7.6 CenterZ=0 NormalX=0 NormalY=0 NormalZ=1 AngleXU=0 Radius=1.8
    g2: Circle CenterX=24.2 CenterY=26.7 CenterZ=0 NormalX=0 NormalY=0 NormalZ=1 AngleXU=0 Radius=3
    g3: Circle CenterX=24.2 CenterY=15.7 CenterZ=0 NormalX=0 NormalY=0 NormalZ=1 AngleXU=0 Radius=3
    g4: Circle CenterX=36.2 CenterY=21.2 CenterZ=0 NormalX=0 NormalY=0 NormalZ=1 AngleXU=0 Radius=2.8
    g5: Circle CenterX=78.51 CenterY=34.8 CenterZ=0 NormalX=0 NormalY=0 NormalZ=1 AngleXU=0 Radius=1.8
    g6: Circle CenterX=78.51 CenterY=7.6 CenterZ=0 NormalX=0 NormalY=0 NormalZ=1 AngleXU=0 Radius=1.8
    g7: Circle CenterX=184.08 CenterY=34.8 CenterZ=0 NormalX=0 NormalY=0 NormalZ=1 AngleXU=0 Radius=1.8
    g8: Circle CenterX=213.443 CenterY=-76.8316 CenterZ=0 NormalX=0 NormalY=0 NormalZ=1 AngleXU=0 Radius=1.8
    g9: Circle CenterX=179.305 CenterY=-76.8316 CenterZ=0 NormalX=0 NormalY=0 NormalZ=1 AngleXU=0 Radius=1.8
    g10: ArcOfCircle [constr] CenterX=132.428 CenterY=4 CenterZ=0 NormalX=0 NormalY=0 NormalZ=1 AngleXU=0 Radius=16 StartAngle=0.314159 EndAngle=1.5708
    g11: ArcOfCircle CenterX=107.6 CenterY=4 CenterZ=0 NormalX=0 NormalY=0 NormalZ=1 AngleXU=0 Radius=16 StartAngle=1.5708 EndAngle=3.00366
    g12: ArcOfCircle CenterX=207.583 CenterY=4 CenterZ=0 NormalX=0 NormalY=0 NormalZ=1 AngleXU=0 Radius=17 StartAngle=1.85815 EndAngle=3.57792
    g13: ArcOfCircle CenterX=184.801 CenterY=-67.3089 CenterZ=0 NormalX=0 NormalY=0 NormalZ=1 AngleXU=0 Radius=33.7833 StartAngle=5.88425 EndAngle=6.71952
    g14: LineSegment StartX=0 StartY=39.2 StartZ=0 EndX=0 EndY=3.2 EndZ=0
    g15: LineSegment StartX=0 StartY=3.2 StartZ=0 EndX=82.8 EndY=3.2 EndZ=0
    g16: LineSegment StartX=82.8 StartY=3.2 StartZ=0 EndX=82.8 EndY=6.2 EndZ=0
    g17: LineSegment StartX=82.8 StartY=6.2 StartZ=0 EndX=91.752 EndY=6.2 EndZ=0
    g18: LineSegment StartX=107.6 StartY=20 StartZ=0 EndX=132.428 EndY=20 EndZ=0
    g19: LineSegment StartX=147.645 StartY=8.94427 StartZ=0 EndX=176.685 EndY=-80.4316 EndZ=0
    g20: LineSegment StartX=176.685 StartY=-80.4316 StartZ=0 EndX=215.932 EndY=-80.4316 EndZ=0
    g21: LineSegment StartX=215.42 StartY=-53.0314 StartZ=0 EndX=192.176 EndY=-3.18451 EndZ=0
    g22: LineSegment StartX=202.765 StartY=20.303 StartZ=0 EndX=195.887 EndY=39.2 EndZ=0
    g23: LineSegment StartX=195.887 StartY=39.2 StartZ=0 EndX=0 EndY=39.2 EndZ=0
    g24: LineSegment StartX=196.467 StartY=26.4942 StartZ=0 EndX=194.073 EndY=33.0721 EndZ=0
    g25: LineSegment StartX=194.073 StartY=33.0721 StartZ=0 EndX=189.939 EndY=31.5672 EndZ=0
    g26: LineSegment StartX=189.939 StartY=31.5672 StartZ=0 EndX=192.333 EndY=24.9893 EndZ=0
    g27: LineSegment StartX=192.333 StartY=24.9893 StartZ=0 EndX=196.467 EndY=26.4942 EndZ=0
    g28: LineSegment StartX=132.428 StartY=20 StartZ=0 EndX=144.053 EndY=20 EndZ=0
    g29: LineSegment StartX=144.053 StartY=20 StartZ=0 EndX=147.645 EndY=8.94427 EndZ=0
  constraints (65):
    c: Equal(g0,g-25)
    c: Equal(g2,g-29)
    c: Equal(g3,g-30)
    c: Equal(g4,g-28)
    c: Equal(g1,g-26)
    c: Coincident(g0,g-25)
    c: Coincident(g1,g-26)
    c: Coincident(g2,g-29)
    c: Coincident(g3,g-30)
    c: Coincident(g4,g-28)
    c: Equal(g5,g-23)
    c: Equal(g6,g-24)
    c: Coincident(g5,g-23)
    c: Coincident(g6,g-24)
    c: Equal(g7,g-20)
    c: Coincident(g7,g-20)
    c: Equal(g9,g-22)
    c: Coincident(g9,g-22)
    c: Equal(g8,g-21)
    c: Coincident(g8,g-21)
    c: Equal(g13,g-12)
    c: Equal(g12,g-14)
    c: Equal(g10,g-9)
    c: Equal(g11,g-7)
    c: Coincident(g14,g-27)
    c: Coincident(g14,g-27)
    c: Coincident(g15,g14)
    c: Coincident(g15,g-5)
    c: Coincident(g16,g15)
    c: Coincident(g16,g-6)
    c: Coincident(g17,g16)
    c: Coincident(g17,g-7)
    c: Coincident(g11,g17)
    c: Coincident(g11,g-8)
    c: Coincident(g18,g11)
    c: Coincident(g18,g-9)
    c: Coincident(g10,g18)
    c: Coincident(g10,g-10)
    c: Coincident(g19,g10)
    c: Coincident(g19,g-11)
    c: Coincident(g20,g19)
    c: Coincident(g20,g-12)
    c: Coincident(g13,g20)
    c: Coincident(g13,g-13)
    c: Coincident(g21,g13)
    c: Coincident(g21,g-14)
    c: Coincident(g12,g21)
    c: Coincident(g12,g-15)
    c: Coincident(g22,g12)
    c: Coincident(g22,g-15)
    c: Coincident(g23,g22)
    c: Coincident(g23,g14)
    c: Coincident(g24,g-18)
    c: Coincident(g24,g-16)
    c: Coincident(g25,g24)
    c: Coincident(g25,g-19)
    c: Coincident(g26,g25)
    c: Coincident(g26,g-19)
    c: Coincident(g27,g26)
    c: Coincident(g27,g24)
    c: Coincident(g29,g10)
    c: Coincident(g28,g10)
    c: Coincident(g29,g28)
    c: Parallel(g28,g18)
    c: Parallel(g29,g19)
FEATURE [PartDesign::Pad] Pad011
  Direction = (0,1,-2e-16)
  Length = 2
  Length2 = 10
  Profile = -> Sketch114
  ReferenceAxis = -> Sketch114 [N_Axis]
  Refine = true
  Reversed = true
  Suppressed = false
  Type = 0
FEATURE [Sketcher::SketchObject] Sketch115
  ArcFitTolerance = 1e-06
  AttachmentSupport = -> [Pad011]
  ExternalGeometry = -> [Binder001]
  FullyConstrained = true
  MakeInternals = false
  MapMode = 5
  Placement = pos=(0,1.7e-15,0) rot=(0,0.707107,0.707107;3.14159rad)
  sketch-geometry (4):
    g0: ArcOfCircle CenterX=24.2 CenterY=26.7 CenterZ=0 NormalX=0 NormalY=0 NormalZ=1 AngleXU=0 Radius=3 StartAngle=4.48384e-08 EndAngle=3.14159
    g1: ArcOfCircle CenterX=24.2 CenterY=15.7 CenterZ=0 NormalX=0 NormalY=0 NormalZ=1 AngleXU=0 Radius=3 StartAngle=3.14159 EndAngle=6.28318
    g2: LineSegment StartX=21.2 StartY=26.7 StartZ=0 EndX=21.2 EndY=15.7 EndZ=0
    g3: LineSegment StartX=27.2 StartY=26.7 StartZ=0 EndX=27.2 EndY=15.7 EndZ=0
  constraints (12):
    c: Equal(g1,g-4)
    c: Equal(g0,g-3)
    c: Coincident(g0,g-3)
    c: Coincident(g1,g-4)
    c: Vertical(g2)
    c: Vertical(g3)
    c: Tangent(g3,g-3)
    c: Tangent(g2,g-3)
    c: Coincident(g0,g2)
    c: Coincident(g0,g3)
    c: Coincident(g1,g2)
    c: Coincident(g3,g1)
FEATURE [Sketcher::SketchObject] Sketch117  label="Sketch117 - fori per inserto M3 x 3 x 4.5"
  ArcFitTolerance = 1e-06
  AttachmentSupport = -> [Pad011]
  ExternalGeometry = -> [Binder001]
  FullyConstrained = true
  MakeInternals = false
  MapMode = 5
  Placement = pos=(0,1.7e-15,0) rot=(0,0.707107,0.707107;3.14159rad)
  sketch-geometry (4):
    g0: Circle CenterX=43.2 CenterY=30.3 CenterZ=0 NormalX=0 NormalY=0 NormalZ=1 AngleXU=0 Radius=2.25
    g1: Circle CenterX=43.2 CenterY=12.1 CenterZ=0 NormalX=0 NormalY=0 NormalZ=1 AngleXU=0 Radius=2.25
    g2: Circle CenterX=18.6 CenterY=30.3 CenterZ=0 NormalX=0 NormalY=0 NormalZ=1 AngleXU=0 Radius=2.25
    g3: Circle CenterX=18.6 CenterY=12.1 CenterZ=0 NormalX=0 NormalY=0 NormalZ=1 AngleXU=0 Radius=2.25
  constraints (8):
    c: Diameter(g0) = 4.5
    c: Diameter(g1) = 4.5
    c: Diameter(g2) = 4.5
    c: Diameter(g3) = 4.5
    c: Coincident(g2,g-3)
    c: Coincident(g3,g-6)
    c: Coincident(g0,g-4)
    c: Coincident(g1,g-5)
FEATURE [Sketcher::SketchObject] Sketch118
  ArcFitTolerance = 1e-06
  AttachmentSupport = -> [Pad011]
  ExternalGeometry = -> [Binder001]
  FullyConstrained = true
  MakeInternals = false
  MapMode = 5
  Placement = pos=(0,-2,0) rot=(1,0,0;1.5708rad)
  sketch-geometry (12):
    g0: Circle CenterX=-78.51 CenterY=34.8 CenterZ=0 NormalX=0 NormalY=0 NormalZ=1 AngleXU=0 Radius=1.8
    g1: Circle CenterX=-78.51 CenterY=7.6 CenterZ=0 NormalX=0 NormalY=0 NormalZ=1 AngleXU=0 Radius=1.8
    g2: Circle CenterX=-5.6 CenterY=34.8 CenterZ=0 NormalX=0 NormalY=0 NormalZ=1 AngleXU=0 Radius=1.8
    g3: Circle CenterX=-5.6 CenterY=7.6 CenterZ=0 NormalX=0 NormalY=0 NormalZ=1 AngleXU=0 Radius=1.8
    g4: LineSegment StartX=0 StartY=39.2 StartZ=0 EndX=0 EndY=3.2 EndZ=0
    g5: LineSegment StartX=0 StartY=3.2 StartZ=0 EndX=-82.8 EndY=3.2 EndZ=0
    g6: LineSegment StartX=-82.8 StartY=3.2 StartZ=0 EndX=-82.8 EndY=39.2 EndZ=0
    g7: LineSegment StartX=-82.8 StartY=39.2 StartZ=0 EndX=0 EndY=39.2 EndZ=0
    g8: ArcOfCircle CenterX=-65 CenterY=21.2 CenterZ=0 NormalX=0 NormalY=0 NormalZ=1 AngleXU=0 Radius=10 StartAngle=1.5708 EndAngle=4.71239
    g9: ArcOfCircle CenterX=-19 CenterY=21.2 CenterZ=0 NormalX=0 NormalY=0 NormalZ=1 AngleXU=0 Radius=10 StartAngle=4.71239 EndAngle=7.85398
    g10: LineSegment StartX=-65 StartY=31.2 StartZ=0 EndX=-19 EndY=31.2 EndZ=0
    g11: LineSegment StartX=-65 StartY=11.2 StartZ=0 EndX=-19 EndY=11.2 EndZ=0
  constraints (25):
    c: Equal(g2,g-5)
    c: Equal(g3,g-7)
    c: Equal(g1,g-6)
    c: Equal(g0,g-4)
    c: Coincident(g0,g-4)
    c: Coincident(g1,g-6)
    c: Coincident(g3,g-7)
    c: Coincident(g2,g-5)
    c: Coincident(g4,g-8)
    c: Coincident(g4,g-9)
    c: Coincident(g5,g4)
    c: Coincident(g5,g-10)
    c: Coincident(g6,g5)
    c: PointOnObject(g6,g-3)
    c: Vertical(g6)
    c: Coincident(g7,g6)
    c: Coincident(g7,g4)
    c: Tangent(g8,g10) = 1.5708
    c: Tangent(g8,g11) = -1.5708
    c: Tangent(g9,g10) = 1.5708
    c: Tangent(g9,g11) = -1.5708
    c: Equal(g8,g9)
    c: Radius(g8) = 10
    c: Coincident(g8,g-11)
    c: Coincident(g9,g-12)
FEATURE [Sketcher::SketchObject] Sketch120
  ArcFitTolerance = 1e-06
  AttachmentSupport = -> [Pad011]
  ExternalGeometry = -> [Binder001]
  FullyConstrained = true
  MakeInternals = false
  MapMode = 5
  Placement = pos=(0,-2,0) rot=(1,0,0;1.5708rad)
  sketch-geometry (4):
    g0: LineSegment StartX=-137.815 StartY=39.2 StartZ=0 EndX=-142.655 EndY=24.303 EndZ=0
    g1: LineSegment StartX=-137.815 StartY=39.2 StartZ=0 EndX=-110.815 EndY=39.2 EndZ=0
    g2: LineSegment StartX=-142.655 StartY=24.303 StartZ=0 EndX=-110.815 EndY=24.303 EndZ=0
    g3: ArcOfCircle CenterX=-92.2534 CenterY=31.7515 CenterZ=0 NormalX=0 NormalY=0 NormalZ=1 AngleXU=0 Radius=20 StartAngle=2.75997 EndAngle=3.52321
  constraints (12):
    c: PointOnObject(g0,g-3)
    c: Coincident(g1,g0)
    c: PointOnObject(g1,g-3)
    c: Coincident(g2,g0)
    c: Horizontal(g2)
    c: Tangent(g0,g-4)
    c: Vertical(g2,g1)
    c: DistanceX(g1,g1) = 27
    c: DistanceY(g-6,g0) = 4
    c: Radius(g3) = 20
    c: Coincident(g3,g1)
    c: Coincident(g3,g2)
FEATURE [Sketcher::SketchObject] Sketch121
  ArcFitTolerance = 1e-06
  AttachmentSupport = -> [Pad011]
  ExternalGeometry = -> [Binder001]
  FullyConstrained = true
  MakeInternals = false
  MapMode = 5
  Placement = pos=(0,-2,0) rot=(1,0,0;1.5708rad)
  sketch-geometry (15):
    g0: LineSegment StartX=-137.815 StartY=39.2 StartZ=0 EndX=-143.955 EndY=20.303 EndZ=0
    g1: LineSegment StartX=-143.955 StartY=20.303 StartZ=0 EndX=-190.141 EndY=20.303 EndZ=0
    g2: LineSegment StartX=-190.141 StartY=20.303 StartZ=0 EndX=-186.139 EndY=31.3 EndZ=0
    g3: LineSegment StartX=-178.754 StartY=39.2 StartZ=0 EndX=-180.791 EndY=33.6029 EndZ=0
    g4: ArcOfCircle CenterX=-184.08 CenterY=34.8 CenterZ=0 NormalX=0 NormalY=0 NormalZ=1 AngleXU=0 Radius=3.5 StartAngle=4.71239 EndAngle=5.93412
    g5: LineSegment StartX=-184.08 StartY=31.3 StartZ=0 EndX=-186.139 EndY=31.3 EndZ=0
    g6: LineSegment StartX=-137.815 StartY=39.2 StartZ=0 EndX=-156.815 EndY=39.2 EndZ=0
    g7: LineSegment StartX=-168.815 StartY=39.2 StartZ=0 EndX=-178.754 EndY=39.2 EndZ=0
    g8: LineSegment StartX=-157.815 StartY=39.2 StartZ=0 EndX=-167.815 EndY=39.2 EndZ=0
    g9: LineSegment StartX=-168.815 StartY=31.2 StartZ=0 EndX=-156.815 EndY=31.2 EndZ=0
    g10: LineSegment StartX=-167.436 StartY=36.2 StartZ=0 EndX=-157.436 EndY=36.2 EndZ=0
    g11: ArcOfCircle CenterX=-176.411 CenterY=35.2 CenterZ=0 NormalX=0 NormalY=0 NormalZ=1 AngleXU=0 Radius=20 StartAngle=6.08183 EndAngle=6.48454
    g12: ArcOfCircle CenterX=-188.411 CenterY=35.2 CenterZ=0 NormalX=0 NormalY=0 NormalZ=1 AngleXU=0 Radius=20 StartAngle=6.08183 EndAngle=6.48454
    g13: ArcOfCircle CenterX=-177.411 CenterY=35.2 CenterZ=0 NormalX=0 NormalY=0 NormalZ=1 AngleXU=0 Radius=20 StartAngle=0.0500209 EndAngle=0.201358
    g14: ArcOfCircle CenterX=-187.411 CenterY=35.2 CenterZ=0 NormalX=0 NormalY=0 NormalZ=1 AngleXU=0 Radius=20 StartAngle=0.0500209 EndAngle=0.201358
  constraints (46):
    c: PointOnObject(g0,g-3)
    c: Tangent(g0,g-5)
    c: Coincident(g1,g0)
    c: Horizontal(g1)
    c: Coincident(g2,g1)
    c: PointOnObject(g3,g-3)
    c: Parallel(g3,g-6)
    c: Parallel(g2,g-6)
    c: Radius(g4) = 3.5
    c: Coincident(g4,g-7)
    c: Tangent(g3,g4) = 1.5708
    c: Horizontal(g5)
    c: Tangent(g5,g4) = 1.5708
    c: DistanceX(g-8,g5) = 3.8
    c: Coincident(g2,g5)
    c: Coincident(g6,g0)
    c: PointOnObject(g6,g-3)
    c: DistanceX(g6,g6) = 19
    c: PointOnObject(g7,g-3)
    c: DistanceX(g7,g6) = 12
    c: Coincident(g7,g3)
    c: PointOnObject(g8,g-3)
    c: PointOnObject(g8,g-3)
    c: DistanceX(g8,g8) = 10
    c: DistanceX(g8,g6) = 1
    c: Horizontal(g9)
    c: Vertical(g7,g9)
    c: Vertical(g6,g9)
    c: DistanceY(g9,g7) = 8
    c: Horizontal(g10)
    c: Equal(g8,g10)
    c: DistanceY(g10,g8) = 3
    c: Radius(g11) = 20
    c: Coincident(g11,g6)
    c: Coincident(g11,g9)
    c: Radius(g12) = 20
    c: Coincident(g12,g7)
    c: Coincident(g12,g9)
    c: Equal(g13,g11)
    c: Coincident(g13,g8)
    c: Coincident(g13,g10)
    c: Horizontal(g13,g11)
    c: Equal(g14,g12)
    c: Coincident(g14,g8)
    c: Coincident(g14,g10)
    c: Horizontal(g1,g-6)
FEATURE [Sketcher::SketchObject] Sketch122
  ArcFitTolerance = 1e-06
  AttachmentSupport = -> [Pad011]
  ExternalGeometry = -> [Binder001]
  FullyConstrained = true
  MakeInternals = false
  MapMode = 5
  Placement = pos=(0,-2,0) rot=(1,0,0;1.5708rad)
  sketch-geometry (8):
    g0: LineSegment StartX=-202.765 StartY=20.303 StartZ=0 EndX=-143.955 EndY=20.303 EndZ=0
    g1: ArcOfCircle CenterX=-184.801 CenterY=-67.3089 CenterZ=0 NormalX=0 NormalY=0 NormalZ=1 AngleXU=0 Radius=33.7833 StartAngle=2.70526 EndAngle=3.54053
    g2: LineSegment StartX=-176.685 StartY=-80.4316 StartZ=0 EndX=-215.932 EndY=-80.4316 EndZ=0
    g3: LineSegment StartX=-215.42 StartY=-53.0315 StartZ=0 EndX=-192.176 EndY=-3.18454 EndZ=0
    g4: ArcOfCircle CenterX=-207.583 CenterY=4 CenterZ=0 NormalX=0 NormalY=0 NormalZ=1 AngleXU=0 Radius=17 StartAngle=5.84685 EndAngle=7.56663
    g5: Circle CenterX=-213.443 CenterY=-76.8316 CenterZ=0 NormalX=0 NormalY=0 NormalZ=1 AngleXU=0 Radius=3
    g6: Circle CenterX=-179.305 CenterY=-76.8316 CenterZ=0 NormalX=0 NormalY=0 NormalZ=1 AngleXU=0 Radius=3
    g7: LineSegment StartX=-143.955 StartY=20.303 StartZ=0 EndX=-176.685 EndY=-80.4316 EndZ=0
  constraints (18):
    c: Coincident(g0,g-6)
    c: Coincident(g1,g-7)
    c: Coincident(g1,g-8)
    c: Coincident(g2,g1)
    c: Tangent(g3,g-5)
    c: Coincident(g4,g-6)
    c: Coincident(g4,g0)
    c: Coincident(g3,g4)
    c: Coincident(g1,g3)
    c: Diameter(g5) = 6
    c: Diameter(g6) = 6
    c: Coincident(g5,g-9)
    c: Coincident(g6,g-10)
    c: Horizontal(g0)
    c: Horizontal(g2)
    c: Coincident(g7,g0)
    c: Coincident(g7,g2)
    c: Tangent(g7,g-4)
FEATURE [Sketcher::SketchObject] Sketch123
  ArcFitTolerance = 1e-06
  AttachmentSupport = -> [Pad011]
  ExternalGeometry = -> [Binder001]
  FullyConstrained = true
  MakeInternals = false
  MapMode = 5
  Placement = pos=(0,-2,0) rot=(1,0,0;1.5708rad)
  sketch-geometry (4):
    g0: LineSegment StartX=-108 StartY=36.8 StartZ=0 EndX=-90 EndY=36.8 EndZ=0
    g1: LineSegment StartX=-108 StartY=36.8 StartZ=0 EndX=-108 EndY=26.8 EndZ=0
    g2: LineSegment StartX=-108 StartY=26.8 StartZ=0 EndX=-90 EndY=26.8 EndZ=0
    g3: ArcOfCircle CenterX=-94 CenterY=31.8 CenterZ=0 NormalX=0 NormalY=0 NormalZ=1 AngleXU=0 Radius=6.40312 StartAngle=5.38713 EndAngle=7.17924
  constraints (13):
    c: Horizontal(g0)
    c: Coincident(g1,g0)
    c: Vertical(g1)
    c: Coincident(g2,g1)
    c: Horizontal(g2)
    c: DistanceX(g0,g0) = 18
    c: DistanceY(g1,g1) = 10
    c: Equal(g0,g2)
    c: DistanceX(g0,g-3) = 90
    c: DistanceY(g0,g-3) = 2.4
    c: Coincident(g3,g0)
    c: Coincident(g3,g2)
    c: DistanceX(g3,g0) = 4
FEATURE [PartDesign::Chamfer] Chamfer014
  Angle = 45
  Base = -> Pad011 [Edge80,Edge4,Edge7]
  BaseFeature = -> Pad011
  ChamferType = 0
  FlipDirection = false
  Refine = true
  Size = 1.9
  Size2 = 1
  SupportTransform = false
  Suppressed = false
  UseAllEdges = false
FEATURE [PartDesign::Pocket] Pocket006
  BaseFeature = -> Chamfer014
  Direction = (0,-1,2e-16)
  Length = 1.2
  Length2 = 5
  Profile = -> Sketch115
  ReferenceAxis = -> Sketch115 [N_Axis]
  Refine = true
  Suppressed = false
  Type = 0
FEATURE [Sketcher::SketchObject] Sketch116  label="Sketch116 - pieno per inserto M3 x 3 x 4,5"
  ArcFitTolerance = 1e-06
  AttachmentSupport = -> [Pocket006]
  ExternalGeometry = -> [Binder001]
  FullyConstrained = true
  MakeInternals = false
  MapMode = 5
  Placement = pos=(0,1.7e-15,0) rot=(0,0.707107,0.707107;3.14159rad)
  sketch-geometry (4):
    g0: Circle CenterX=43.2 CenterY=30.3 CenterZ=0 NormalX=0 NormalY=0 NormalZ=1 AngleXU=0 Radius=3.4
    g1: Circle CenterX=43.2 CenterY=12.1 CenterZ=0 NormalX=0 NormalY=0 NormalZ=1 AngleXU=0 Radius=3.4
    g2: Circle CenterX=18.6 CenterY=30.3 CenterZ=0 NormalX=0 NormalY=0 NormalZ=1 AngleXU=0 Radius=3.4
    g3: Circle CenterX=18.6 CenterY=12.1 CenterZ=0 NormalX=0 NormalY=0 NormalZ=1 AngleXU=0 Radius=3.4
  constraints (8):
    c: Diameter(g0) = 6.8
    c: Diameter(g1) = 6.8
    c: Diameter(g2) = 6.8
    c: Diameter(g3) = 6.8
    c: Coincident(g2,g-3)
    c: Coincident(g0,g-4)
    c: Coincident(g3,g-6)
    c: Coincident(g1,g-5)
FEATURE [PartDesign::Pad] Pad012
  BaseFeature = -> Pocket006
  Direction = (0,1,-2e-16)
  Length = 2.4
  Length2 = 10
  Profile = -> Sketch116
  ReferenceAxis = -> Sketch116 [N_Axis]
  Refine = true
  Suppressed = false
  Type = 0
FEATURE [PartDesign::Pocket] Pocket007
  BaseFeature = -> Pad012
  Direction = (0,-1,2e-16)
  Length = 0.6
  Length2 = 2.4
  Profile = -> Sketch117
  ReferenceAxis = -> Sketch117 [N_Axis]
  Refine = true
  Suppressed = false
  Type = 4
FEATURE [PartDesign::Pad] Pad013
  BaseFeature = -> Pocket007
  Direction = (0,-1,2e-16)
  Length = 1.6
  Length2 = 10
  Profile = -> Sketch118
  ReferenceAxis = -> Sketch118 [N_Axis]
  Refine = true
  Suppressed = false
  Type = 0
FEATURE [Sketcher::SketchObject] Sketch119
  ArcFitTolerance = 1e-06
  AttachmentSupport = -> [Pad013]
  ExternalGeometry = -> [Binder001]
  FullyConstrained = true
  MakeInternals = false
  MapMode = 5
  Placement = pos=(0,-3.6,0) rot=(1,0,0;1.5708rad)
  sketch-geometry (21):
    g0: LineSegment [constr] StartX=-82.8 StartY=3.2 StartZ=0 EndX=-82.8 EndY=39.2 EndZ=0
    g1: ArcOfCircle CenterX=-78.51 CenterY=34.8 CenterZ=0 NormalX=0 NormalY=0 NormalZ=1 AngleXU=0 Radius=3.5 StartAngle=4.71239 EndAngle=6.28319
    g2: ArcOfCircle CenterX=-78.51 CenterY=7.6 CenterZ=0 NormalX=0 NormalY=0 NormalZ=1 AngleXU=0 Radius=3.5 StartAngle=0 EndAngle=1.5708
    g3: ArcOfCircle CenterX=-5.6 CenterY=34.8 CenterZ=0 NormalX=0 NormalY=0 NormalZ=1 AngleXU=0 Radius=3.5 StartAngle=3.14159 EndAngle=4.71239
    g4: ArcOfCircle CenterX=-5.6 CenterY=7.6 CenterZ=0 NormalX=0 NormalY=0 NormalZ=1 AngleXU=0 Radius=3.5 StartAngle=1.5708 EndAngle=3.14159
    g5: LineSegment StartX=0 StartY=39.2 StartZ=0 EndX=0 EndY=31.3 EndZ=0
    g6: LineSegment StartX=0 StartY=39.2 StartZ=0 EndX=-9.1 EndY=39.2 EndZ=0
    g7: LineSegment StartX=0 StartY=3.2 StartZ=0 EndX=0 EndY=11.1 EndZ=0
    g8: LineSegment StartX=0 StartY=3.2 StartZ=0 EndX=-9.1 EndY=3.2 EndZ=0
    g9: LineSegment StartX=-82.8 StartY=3.2 StartZ=0 EndX=-75.01 EndY=3.2 EndZ=0
    g10: LineSegment StartX=-82.8 StartY=3.2 StartZ=0 EndX=-82.8 EndY=11.1 EndZ=0
    g11: LineSegment StartX=-82.8 StartY=39.2 StartZ=0 EndX=-82.8 EndY=31.3 EndZ=0
    g12: LineSegment StartX=-82.8 StartY=39.2 StartZ=0 EndX=-75.01 EndY=39.2 EndZ=0
    g13: LineSegment StartX=-82.8 StartY=31.3 StartZ=0 EndX=-78.51 EndY=31.3 EndZ=0
    g14: LineSegment StartX=-75.01 StartY=39.2 StartZ=0 EndX=-75.01 EndY=34.8 EndZ=0
    g15: LineSegment StartX=-82.8 StartY=11.1 StartZ=0 EndX=-78.51 EndY=11.1 EndZ=0
    g16: LineSegment StartX=-75.01 StartY=3.2 StartZ=0 EndX=-75.01 EndY=7.6 EndZ=0
    g17: LineSegment StartX=-9.1 StartY=39.2 StartZ=0 EndX=-9.1 EndY=34.8 EndZ=0
    g18: LineSegment StartX=0 StartY=31.3 StartZ=0 EndX=-5.6 EndY=31.3 EndZ=0
    g19: LineSegment StartX=0 StartY=11.1 StartZ=0 EndX=-5.6 EndY=11.1 EndZ=0
    g20: LineSegment StartX=-9.1 StartY=3.2 StartZ=0 EndX=-9.1 EndY=7.6 EndZ=0
  constraints (51):
    c: Coincident(g0,g-10)
    c: PointOnObject(g0,g-8)
    c: Vertical(g0)
    c: Coincident(g1,g-3)
    c: Coincident(g2,g-4)
    c: Coincident(g3,g-5)
    c: Coincident(g4,g-6)
    c: Radius(g4) = 3.5
    c: Radius(g3) = 3.5
    c: Radius(g1) = 3.5
    c: Radius(g2) = 3.5
    c: Coincident(g5,g-9)
    c: PointOnObject(g5,g-9)
    c: Coincident(g6,g5)
    c: PointOnObject(g6,g-8)
    c: Coincident(g7,g-9)
    c: PointOnObject(g7,g-9)
    c: Coincident(g8,g7)
    c: PointOnObject(g8,g-7)
    c: Coincident(g9,g0)
    c: PointOnObject(g9,g-7)
    c: Coincident(g10,g0)
    c: PointOnObject(g10,g0)
    c: Coincident(g11,g0)
    c: PointOnObject(g11,g0)
    c: Coincident(g12,g0)
    c: PointOnObject(g12,g-8)
    c: Coincident(g13,g11)
    c: Horizontal(g13)
    c: Coincident(g14,g12)
    c: Vertical(g14)
    c: Coincident(g15,g10)
    c: Horizontal(g15)
    c: Coincident(g16,g9)
    c: Vertical(g16)
    c: Coincident(g17,g6)
    c: Vertical(g17)
    c: Coincident(g18,g5)
    c: Horizontal(g18)
    c: Coincident(g19,g7)
    c: Horizontal(g19)
    c: Coincident(g20,g8)
    c: Vertical(g20)
    c: Tangent(g20,g4) = 1.5708
    c: Tangent(g4,g19) = -1.5708
    c: Tangent(g18,g3) = 1.5708
    c: Tangent(g3,g17) = -1.5708
    c: Tangent(g13,g1) = -1.5708
    c: Tangent(g1,g14) = 1.5708
    c: Tangent(g16,g2) = -1.5708
    c: Tangent(g2,g15) = 1.5708
FEATURE [PartDesign::Pocket] Pocket008
  BaseFeature = -> Pad013
  Direction = (0,1,-2e-16)
  Length = 1.6
  Length2 = 5
  Profile = -> Sketch119
  ReferenceAxis = -> Sketch119 [N_Axis]
  Refine = true
  Suppressed = false
  Type = 0
FEATURE [PartDesign::Pad] Pad017
  BaseFeature = -> Pocket008
  Direction = (0,-1,2e-16)
  Length = 1.6
  Length2 = 10
  Profile = -> Sketch123
  ReferenceAxis = -> Sketch123 [N_Axis]
  Refine = true
  Suppressed = false
  Type = 0
FEATURE [Sketcher::SketchObject] Sketch125
  ArcFitTolerance = 1e-06
  AttachmentSupport = -> [Pad017]
  ExternalGeometry = -> [Pad017]
  FullyConstrained = true
  MakeInternals = false
  MapMode = 5
  Placement = pos=(0,-3.6,8e-16) rot=(1,0,0;1.5708rad)
  sketch-geometry (20):
    g0: LineSegment StartX=-108 StartY=35.8 StartZ=0 EndX=-108 EndY=35 EndZ=0
    g1: LineSegment StartX=-108 StartY=35 StartZ=0 EndX=-97 EndY=35 EndZ=0
    g2: LineSegment StartX=-97 StartY=35 StartZ=0 EndX=-97 EndY=35.8 EndZ=0
    g3: LineSegment StartX=-97 StartY=35.8 StartZ=0 EndX=-108 EndY=35.8 EndZ=0
    g4: LineSegment StartX=-108 StartY=28.6 StartZ=0 EndX=-108 EndY=27.8 EndZ=0
    g5: LineSegment StartX=-108 StartY=27.8 StartZ=0 EndX=-97 EndY=27.8 EndZ=0
    g6: LineSegment StartX=-97 StartY=27.8 StartZ=0 EndX=-97 EndY=28.6 EndZ=0
    g7: LineSegment StartX=-97 StartY=28.6 StartZ=0 EndX=-108 EndY=28.6 EndZ=0
    g8: LineSegment StartX=-108 StartY=30.4 StartZ=0 EndX=-108 EndY=29.6 EndZ=0
    g9: LineSegment StartX=-108 StartY=29.6 StartZ=0 EndX=-97 EndY=29.6 EndZ=0
    g10: LineSegment StartX=-97 StartY=29.6 StartZ=0 EndX=-97 EndY=30.4 EndZ=0
    g11: LineSegment StartX=-97 StartY=30.4 StartZ=0 EndX=-108 EndY=30.4 EndZ=0
    g12: LineSegment StartX=-108 StartY=32.2 StartZ=0 EndX=-108 EndY=31.4 EndZ=0
    g13: LineSegment StartX=-108 StartY=31.4 StartZ=0 EndX=-97 EndY=31.4 EndZ=0
    g14: LineSegment StartX=-97 StartY=31.4 StartZ=0 EndX=-97 EndY=32.2 EndZ=0
    g15: LineSegment StartX=-97 StartY=32.2 StartZ=0 EndX=-108 EndY=32.2 EndZ=0
    g16: LineSegment StartX=-108 StartY=34 StartZ=0 EndX=-108 EndY=33.2 EndZ=0
    g17: LineSegment StartX=-108 StartY=33.2 StartZ=0 EndX=-97 EndY=33.2 EndZ=0
    g18: LineSegment StartX=-97 StartY=33.2 StartZ=0 EndX=-97 EndY=34 EndZ=0
    g19: LineSegment StartX=-97 StartY=34 StartZ=0 EndX=-108 EndY=34 EndZ=0
  constraints (55):
    c: Coincident(g1,g0)
    c: Horizontal(g1)
    c: Coincident(g2,g1)
    c: Vertical(g2)
    c: Coincident(g3,g2)
    c: Horizontal(g3)
    c: Coincident(g3,g0)
    c: DistanceX(g1,g1) = 11
    c: DistanceY(g2,g2) = 0.8
    c: Coincident(g5,g4)
    c: Horizontal(g5)
    c: Coincident(g6,g5)
    c: Vertical(g6)
    c: Coincident(g7,g6)
    c: Horizontal(g7)
    c: Coincident(g7,g4)
    c: Coincident(g9,g8)
    c: Horizontal(g9)
    c: Coincident(g10,g9)
    c: Vertical(g10)
    c: Coincident(g11,g10)
    c: Horizontal(g11)
    c: Coincident(g11,g8)
    c: Coincident(g13,g12)
    c: Horizontal(g13)
    c: Coincident(g14,g13)
    c: Vertical(g14)
    c: Coincident(g15,g14)
    c: Horizontal(g15)
    c: Coincident(g15,g12)
    c: Coincident(g17,g16)
    c: Horizontal(g17)
    c: Coincident(g18,g17)
    c: Vertical(g18)
    c: Coincident(g19,g18)
    c: Horizontal(g19)
    c: Coincident(g19,g16)
    c: Equal(g3,g19)
    c: Equal(g3,g15)
    c: Equal(g3,g11)
    c: Equal(g3,g7)
    c: Equal(g2,g18)
    c: Equal(g2,g14)
    c: Equal(g2,g10)
    c: Equal(g2,g6)
    c: DistanceY(g-4,g4) = 1
    c: DistanceY(g4,g8) = 1
    c: DistanceY(g8,g12) = 1
    c: DistanceY(g12,g16) = 1
    c: DistanceY(g16,g0) = 1
    c: Tangent(g0,g-5)
    c: Tangent(g16,g-5)
    c: Tangent(g12,g-5)
    c: Tangent(g8,g-5)
    c: Tangent(g4,g-5)
FEATURE [PartDesign::Chamfer] Chamfer009
  Angle = 45
  Base = -> Pad017 [Edge151,Edge154]
  BaseFeature = -> Pad017
  ChamferType = 1
  FlipDirection = false
  Refine = true
  Size = 1.5
  Size2 = 2.8
  SupportTransform = false
  Suppressed = false
  UseAllEdges = false
FEATURE [PartDesign::Pocket] Pocket009
  BaseFeature = -> Chamfer009
  Direction = (0,1,-2e-16)
  Length = 1
  Length2 = 5
  Profile = -> Sketch125
  ReferenceAxis = -> Sketch125 [N_Axis]
  Refine = true
  Suppressed = false
  Type = 0
FEATURE [PartDesign::Pad] Pad014
  BaseFeature = -> Pocket009
  Direction = (0,-1,2e-16)
  Length = 0.8
  Length2 = 10
  Profile = -> Sketch120
  ReferenceAxis = -> Sketch120 [N_Axis]
  Refine = true
  Suppressed = false
  Type = 0
FEATURE [Sketcher::SketchObject] Sketch124
  ArcFitTolerance = 1e-06
  AttachmentSupport = -> [Pad014]
  ExternalGeometry = -> [Binder001]
  FullyConstrained = true
  MakeInternals = false
  MapMode = 5
  Placement = pos=(0,-2.8,6e-16) rot=(1,0,0;1.5708rad)
  sketch-geometry (4):
    g0: LineSegment StartX=-129 StartY=39.2 StartZ=0 EndX=-131.599 EndY=31.2 EndZ=0
    g1: LineSegment StartX=-118 StartY=39.2 StartZ=0 EndX=-120.599 EndY=31.2 EndZ=0
    g2: LineSegment StartX=-129 StartY=39.2 StartZ=0 EndX=-118 EndY=39.2 EndZ=0
    g3: LineSegment StartX=-120.599 StartY=31.2 StartZ=0 EndX=-131.599 EndY=31.2 EndZ=0
  constraints (12):
    c: PointOnObject(g0,g-3)
    c: PointOnObject(g1,g-3)
    c: Parallel(g-4,g0)
    c: Parallel(g-4,g1)
    c: Coincident(g2,g0)
    c: Coincident(g2,g1)
    c: DistanceX(g2,g2) = 11
    c: DistanceY(g1,g1) = 8
    c: Coincident(g3,g1)
    c: Horizontal(g3)
    c: Coincident(g3,g0)
    c: DistanceX(g1,g-3) = 118
FEATURE [PartDesign::Pad] Pad018
  BaseFeature = -> Pad014
  Direction = (0,-1,2e-16)
  Length = 1.2
  Length2 = 10
  Profile = -> Sketch124
  ReferenceAxis = -> Sketch124 [N_Axis]
  Refine = true
  Suppressed = false
  Type = 0
FEATURE [Sketcher::SketchObject] Sketch126
  ArcFitTolerance = 1e-06
  AttachmentSupport = -> [Pad018]
  ExternalGeometry = -> [Pad018]
  FullyConstrained = true
  MakeInternals = false
  MapMode = 5
  Placement = pos=(0,-4,0) rot=(1,0,0;1.5708rad)
  sketch-geometry (8):
    g0: LineSegment StartX=-129.877 StartY=36.5 StartZ=0 EndX=-130.137 EndY=35.7 EndZ=0
    g1: LineSegment StartX=-130.69 StartY=34 StartZ=0 EndX=-130.95 EndY=33.2 EndZ=0
    g2: LineSegment StartX=-129.877 StartY=36.5 StartZ=0 EndX=-118.877 EndY=36.5 EndZ=0
    g3: LineSegment StartX=-130.137 StartY=35.7 StartZ=0 EndX=-119.137 EndY=35.7 EndZ=0
    g4: LineSegment StartX=-130.69 StartY=34 StartZ=0 EndX=-119.69 EndY=34 EndZ=0
    g5: LineSegment StartX=-130.95 StartY=33.2 StartZ=0 EndX=-119.95 EndY=33.2 EndZ=0
    g6: LineSegment StartX=-118.877 StartY=36.5 StartZ=0 EndX=-119.137 EndY=35.7 EndZ=0
    g7: LineSegment StartX=-119.69 StartY=34 StartZ=0 EndX=-119.95 EndY=33.2 EndZ=0
  constraints (20):
    c: Coincident(g2,g0)
    c: Horizontal(g2)
    c: Coincident(g3,g0)
    c: Horizontal(g3)
    c: Coincident(g4,g1)
    c: Horizontal(g4)
    c: Coincident(g5,g1)
    c: Horizontal(g5)
    c: Coincident(g6,g2)
    c: Coincident(g6,g3)
    c: Coincident(g7,g4)
    c: Coincident(g7,g5)
    c: Tangent(g0,g-4)
    c: Tangent(g6,g-5)
    c: Tangent(g1,g-4)
    c: Tangent(g7,g-5)
    c: DistanceY(g3,g2) = 0.8
    c: DistanceY(g5,g4) = 0.8
    c: DistanceY(g-6,g1) = 2
    c: DistanceY(g-6,g0) = 4.5
FEATURE [PartDesign::Chamfer] Chamfer008
  Angle = 45
  Base = -> Pad018 [Edge257]
  BaseFeature = -> Pad018
  ChamferType = 1
  FlipDirection = false
  Refine = true
  Size = 1
  Size2 = 6
  SupportTransform = false
  Suppressed = false
  UseAllEdges = false
FEATURE [PartDesign::Pocket] Pocket010
  BaseFeature = -> Chamfer008
  Direction = (0,1,-2e-16)
  Length = 1
  Length2 = 5
  Profile = -> Sketch126
  ReferenceAxis = -> Sketch126 [N_Axis]
  Refine = true
  Suppressed = false
  Type = 0
FEATURE [PartDesign::Pad] Pad015
  BaseFeature = -> Pocket010
  Direction = (0,-1,2e-16)
  Length = 2
  Length2 = 10
  Profile = -> Sketch121
  ReferenceAxis = -> Sketch121 [N_Axis]
  Refine = true
  Suppressed = false
  Type = 0
FEATURE [PartDesign::Pad] Pad016
  BaseFeature = -> Pad015
  Direction = (0,-1,2e-16)
  Length = 1.6
  Length2 = 10
  Profile = -> Sketch122
  ReferenceAxis = -> Sketch122 [N_Axis]
  Refine = true
  Suppressed = false
  Type = 0
FEATURE [Sketcher::SketchObject] Sketch127
  ArcFitTolerance = 1e-06
  AttachmentSupport = -> [Pad016]
  ExternalGeometry = -> [Pad016]
  FullyConstrained = true
  MakeInternals = false
  MapMode = 5
  Placement = pos=(0,0,-80.4316) rot=(1,0,0;3.14159rad)
  sketch-geometry (8):
    g0: LineSegment StartX=-176.685 StartY=3.6 StartZ=0 EndX=-186.685 EndY=3.6 EndZ=0
    g1: LineSegment [constr] StartX=-186.685 StartY=3.6 StartZ=0 EndX=-186.685 EndY=-9e-16 EndZ=0
    g2: LineSegment StartX=-176.685 StartY=3.6 StartZ=0 EndX=-176.685 EndY=0 EndZ=0
    g3: ArcOfEllipse CenterX=-186.685 CenterY=-9e-16 CenterZ=0 NormalX=0 NormalY=0 NormalZ=1 MajorRadius=10 MinorRadius=3.6 AngleXU=1e-16 StartAngle=0 EndAngle=1.5708
    g4: LineSegment [constr] StartX=-176.685 StartY=-2e-15 StartZ=0 EndX=-196.685 EndY=-2e-15 EndZ=0
    g5: LineSegment [constr] StartX=-186.685 StartY=3.6 StartZ=0 EndX=-186.685 EndY=-3.6 EndZ=0
    g6: GeomPoint [constr] X=-177.356 Y=0 Z=0
    g7: GeomPoint [constr] X=-196.015 Y=-1.9e-15 Z=0
  constraints (13):
    c: Coincident(g0,g-4)
    c: PointOnObject(g0,g-4)
    c: DistanceX(g0,g0) = 10
    c: Coincident(g1,g0)
    c: PointOnObject(g1,g-5)
    c: Vertical(g1)
    c: Coincident(g2,g0)
    c: Coincident(g2,g-5)
    c: InternalAlignment(g4-g7 -> g3) x4
    c: Coincident(g3,g1)
    c: Coincident(g3,g0)
    c: Coincident(g3,g2)
    c: Horizontal(g4)
FEATURE [Sketcher::SketchObject] Sketch128
  ArcFitTolerance = 1e-06
  AttachmentSupport = -> [Pad016]
  ExternalGeometry = -> [Pad016]
  FullyConstrained = true
  MakeInternals = false
  MapMode = 5
  Placement = pos=(0,0,-80.4316) rot=(1,0,0;3.14159rad)
  sketch-geometry (8):
    g0: LineSegment StartX=-215.932 StartY=3.6 StartZ=0 EndX=-215.932 EndY=-1.3e-15 EndZ=0
    g1: LineSegment StartX=-215.932 StartY=3.6 StartZ=0 EndX=-205.932 EndY=3.6 EndZ=0
    g2: LineSegment [constr] StartX=-205.932 StartY=3.6 StartZ=0 EndX=-205.932 EndY=-9e-16 EndZ=0
    g3: ArcOfEllipse CenterX=-205.932 CenterY=-9e-16 CenterZ=0 NormalX=0 NormalY=0 NormalZ=1 MajorRadius=10 MinorRadius=3.6 AngleXU=-3.14159 StartAngle=4.71239 EndAngle=6.28319
    g4: LineSegment [constr] StartX=-215.932 StartY=-1e-15 StartZ=0 EndX=-195.932 EndY=-1e-15 EndZ=0
    g5: LineSegment [constr] StartX=-205.932 StartY=-3.6 StartZ=0 EndX=-205.932 EndY=3.6 EndZ=0
    g6: GeomPoint [constr] X=-215.262 Y=-2e-15 Z=0
    g7: GeomPoint [constr] X=-196.602 Y=-1e-15 Z=0
  constraints (13):
    c: Coincident(g0,g-4)
    c: Coincident(g0,g-5)
    c: Coincident(g1,g0)
    c: PointOnObject(g1,g-3)
    c: DistanceX(g1,g1) = 10
    c: Coincident(g2,g1)
    c: Vertical(g2)
    c: PointOnObject(g2,g-5)
    c: InternalAlignment(g4-g7 -> g3) x4
    c: Coincident(g3,g2)
    c: Coincident(g3,g1)
    c: Coincident(g3,g0)
    c: Horizontal(g4)
FEATURE [PartDesign::SubtractivePipe] SubtractivePipe002
  AuxilleryCurvelinear = true
  AuxillerySpineTangent = false
  BaseFeature = -> Pad016
  Binormal = (0,0,0)
  Mode = 0
  Profile = -> Sketch127
  Refine = true
  Spine = -> Pad016 [Edge254]
  SpineTangent = false
  Suppressed = false
  Transformation = 0
  Transition = 0
FEATURE [PartDesign::SubtractivePipe] SubtractivePipe003
  AuxilleryCurvelinear = true
  AuxillerySpineTangent = false
  BaseFeature = -> SubtractivePipe002
  Binormal = (0,0,0)
  Mode = 0
  Profile = -> Sketch128
  Refine = true
  Spine = -> Pad016 [Edge256,Edge251,Edge252]
  SpineTangent = false
  Suppressed = false
  Transformation = 0
  Transition = 0
FEATURE [Sketcher::SketchObject] Sketch129
  ArcFitTolerance = 1e-06
  AttachmentSupport = -> [Pad016]
  ExternalGeometry = -> [Binder001]
  FullyConstrained = true
  MakeInternals = false
  MapMode = 5
  Placement = pos=(0,-3.6,0) rot=(1,0,0;1.5708rad)
  sketch-geometry (12):
    g0: LineSegment [constr] StartX=-192.176 StartY=-3.18451 StartZ=0 EndX=-181.223 EndY=20.303 EndZ=0
    g1: LineSegment [constr] StartX=-202.765 StartY=20.303 StartZ=0 EndX=-181.223 EndY=20.303 EndZ=0
    g2: LineSegment StartX=-202.765 StartY=20.303 StartZ=0 EndX=-181.223 EndY=20.303 EndZ=0
    g3: LineSegment StartX=-192.176 StartY=-3.18451 StartZ=0 EndX=-196.804 EndY=-13.1107 EndZ=0
    g4: ArcOfCircle CenterX=-207.583 CenterY=4 CenterZ=0 NormalX=0 NormalY=0 NormalZ=1 AngleXU=0 Radius=17 StartAngle=5.84685 EndAngle=7.56663
    g5: ArcOfEllipse CenterX=-181.223 CenterY=8.55923 CenterZ=0 NormalX=0 NormalY=0 NormalZ=1 MajorRadius=23.4779 MinorRadius=11.7437 AngleXU=2e-16 StartAngle=4.71239 EndAngle=7.85398
    g6: LineSegment [constr] StartX=-157.745 StartY=8.55923 StartZ=0 EndX=-204.701 EndY=8.55923 EndZ=0
    g7: LineSegment [constr] StartX=-181.223 StartY=20.303 StartZ=0 EndX=-181.223 EndY=-3.18451 EndZ=0
    g8: GeomPoint [constr] X=-160.894 Y=8.55923 Z=0
    g9: GeomPoint [constr] X=-201.553 Y=8.55923 Z=0
    g10: ArcOfCircle CenterX=-181.223 CenterY=-20.3763 CenterZ=0 NormalX=0 NormalY=0 NormalZ=1 AngleXU=0 Radius=17.1918 StartAngle=1.57079 EndAngle=2.70526
    g11: GeomPoint [constr] X=-181.223 Y=-3.18451 Z=0
  constraints (23):
    c: Coincident(g0,g-5)
    c: Coincident(g1,g-6)
    c: Horizontal(g1)
    c: Coincident(g1,g0)
    c: Parallel(g0,g-4)
    c: Coincident(g2,g1)
    c: Coincident(g2,g0)
    c: Coincident(g3,g0)
    c: Equal(g4,g-5)
    c: Coincident(g4,g1)
    c: Coincident(g4,g0)
    c: InternalAlignment(g6-g9 -> g5) x4
    c: Vertical(g5,g0)
    c: Horizontal(g6)
    c: Coincident(g5,g0)
    c: DistanceX(g6,g-3) = 10.1
    c: Tangent(g10,g3) = -1.5708
    c: PointOnObject(g11,g10)
    c: Tangent(g5,g10,g11) = 1.5708
    c: Coincident(g10,g5)
    c: Coincident(g11,g7)
    c: Parallel(g3,g-4)
    c: Horizontal(g5,g0)
FEATURE [Sketcher::SketchObject] Sketch130
  ArcFitTolerance = 1e-06
  AttachmentOffset = pos=(0,0,-1.6) rot=(0,0,1;0rad)
  AttachmentSupport = -> [Pad016]
  ExternalGeometry = -> [Binder001]
  FullyConstrained = true
  MakeInternals = false
  MapMode = 5
  Placement = pos=(0,-2,-4e-16) rot=(1,0,0;1.5708rad)
  sketch-geometry (12):
    g0: LineSegment [constr] StartX=-192.176 StartY=-3.18451 StartZ=0 EndX=-181.223 EndY=20.303 EndZ=0
    g1: LineSegment [constr] StartX=-202.765 StartY=20.303 StartZ=0 EndX=-181.223 EndY=20.303 EndZ=0
    g2: LineSegment StartX=-202.765 StartY=20.303 StartZ=0 EndX=-181.223 EndY=20.303 EndZ=0
    g3: LineSegment StartX=-192.176 StartY=-3.18451 StartZ=0 EndX=-193.827 EndY=-6.72678 EndZ=0
    g4: ArcOfCircle CenterX=-207.583 CenterY=4 CenterZ=0 NormalX=0 NormalY=0 NormalZ=1 AngleXU=0 Radius=17 StartAngle=5.84685 EndAngle=7.56663
    g5: ArcOfEllipse CenterX=-181.223 CenterY=10.803 CenterZ=0 NormalX=0 NormalY=0 NormalZ=1 MajorRadius=14.4779 MinorRadius=9.5 AngleXU=0 StartAngle=4.71239 EndAngle=7.85398
    g6: LineSegment [constr] StartX=-166.745 StartY=10.803 StartZ=0 EndX=-195.701 EndY=10.803 EndZ=0
    g7: LineSegment [constr] StartX=-181.223 StartY=20.303 StartZ=0 EndX=-181.223 EndY=1.30297 EndZ=0
    g8: GeomPoint [constr] X=-170.298 Y=10.803 Z=0
    g9: GeomPoint [constr] X=-192.148 Y=10.803 Z=0
    g10: ArcOfCircle CenterX=-181.223 CenterY=-12.6042 CenterZ=0 NormalX=0 NormalY=0 NormalZ=1 AngleXU=0 Radius=13.9072 StartAngle=1.5708 EndAngle=2.70526
    g11: GeomPoint [constr] X=-181.223 Y=1.30297 Z=0
  constraints (23):
    c: Coincident(g0,g-5)
    c: Coincident(g1,g-6)
    c: Horizontal(g1)
    c: Coincident(g1,g0)
    c: Parallel(g0,g-4)
    c: Coincident(g2,g1)
    c: Coincident(g2,g0)
    c: Coincident(g3,g0)
    c: Equal(g4,g-5)
    c: Coincident(g4,g1)
    c: Coincident(g4,g0)
    c: InternalAlignment(g6-g9 -> g5) x4
    c: Vertical(g5,g0)
    c: Horizontal(g6)
    c: Coincident(g5,g0)
    c: DistanceX(g6,g-3) = 19.1
    c: Tangent(g10,g3) = -1.5708
    c: PointOnObject(g11,g10)
    c: Tangent(g5,g10,g11) = 1.5708
    c: Coincident(g10,g5)
    c: Coincident(g11,g7)
    c: Parallel(g3,g-4)
    c: DistanceY(g5,g0) = 19
FEATURE [Part::Part2DObjectPython] Clone2D001  label="Sketch130 (2D)"  # Draft 2D object (typed FeaturePython)
  Fuse = false
  Objects = -> [Sketch130]
  Placement = pos=(0,-2,-4e-16) rot=(1,0,0;1.5708rad)
  Scale = (1,1,1)
FEATURE [Sketcher::SketchObject] Sketch131
  ArcFitTolerance = 1e-06
  AttachmentOffset = pos=(0,0,-3.5) rot=(0,0,1;0rad)
  AttachmentSupport = -> [Pad016]
  ExternalGeometry = -> [Binder001]
  FullyConstrained = true
  MakeInternals = false
  MapMode = 5
  Placement = pos=(0,-0.1,-8e-16) rot=(1,0,0;1.5708rad)
  sketch-geometry (1):
    g0: GeomPoint X=-197.47 Y=8.55923 Z=0
  constraints (1):
    c: Symmetric(g-6,g-4,g0)
FEATURE [PartDesign::SubtractiveLoft] SubtractiveLoft002
  BaseFeature = -> SubtractivePipe003
  Closed = false
  Profile = -> Sketch129
  Refine = true
  Ruled = false
  Sections = -> [Sketch130]
  Suppressed = false
FEATURE [PartDesign::SubtractiveLoft] SubtractiveLoft003
  BaseFeature = -> SubtractiveLoft002
  Closed = false
  Profile = -> Clone2D001
  Refine = true
  Ruled = false
  Sections = -> [Sketch131]
  Suppressed = false
FEATURE [PartDesign::Chamfer] Chamfer010
  Angle = 45
  Base = -> SubtractiveLoft003 [Edge200,Edge201,Edge203,Edge202,Edge194]
  BaseFeature = -> SubtractiveLoft003
  ChamferType = 0
  FlipDirection = false
  Refine = true
  Size = 1.5
  Size2 = 1
  SupportTransform = false
  Suppressed = false
  UseAllEdges = false
FEATURE [PartDesign::Chamfer] Chamfer011
  Angle = 45
  Base = -> Chamfer010 [Edge15]
  BaseFeature = -> Chamfer010
  ChamferType = 0
  FlipDirection = false
  Refine = true
  Size = 1.6
  Size2 = 1
  SupportTransform = false
  Suppressed = false
  UseAllEdges = false
FEATURE [PartDesign::Chamfer] Chamfer012
  Angle = 45
  Base = -> Chamfer011 [Edge10]
  BaseFeature = -> Chamfer011
  ChamferType = 0
  FlipDirection = false
  Refine = true
  Size = 3.5
  Size2 = 1
  SupportTransform = false
  Suppressed = false
  UseAllEdges = false
FEATURE [PartDesign::Chamfer] Chamfer013
  Angle = 45
  Base = -> Chamfer012 [Edge145,Edge94]
  BaseFeature = -> Chamfer012
  ChamferType = 0
  FlipDirection = false
  Refine = true
  Size = 1.9
  Size2 = 1
  SupportTransform = false
  Suppressed = false
  UseAllEdges = false
FEATURE [Sketcher::SketchObject] Sketch132
  ArcFitTolerance = 1e-06
  AttachmentSupport = -> [Pad016]
  ExternalGeometry = -> [Binder001]
  FullyConstrained = true
  MakeInternals = false
  MapMode = 5
  Placement = pos=(0,-3.6,0) rot=(1,0,0;1.5708rad)
  sketch-geometry (3):
    g0: LineSegment [constr] StartX=-215.42 StartY=-53.0314 StartZ=0 EndX=-167.782 EndY=-53.0314 EndZ=0
    g1: Circle CenterX=-191.282 CenterY=-53.0314 CenterZ=0 NormalX=0 NormalY=0 NormalZ=1 AngleXU=0 Radius=11.5
    g2: Circle CenterX=-191.282 CenterY=-53.0314 CenterZ=0 NormalX=0 NormalY=0 NormalZ=1 AngleXU=0 Radius=10.7
  constraints (8):
    c: Coincident(g0,g-3)
    c: PointOnObject(g0,g-4)
    c: Horizontal(g0)
    c: Diameter(g1) = 23
    c: PointOnObject(g1,g0)
    c: DistanceX(g1,g0) = 23.5
    c: Diameter(g2) = 21.4
    c: Coincident(g2,g1)
FEATURE [PartDesign::Fillet] Fillet007
  Base = -> Chamfer013 [Edge83]
  BaseFeature = -> Chamfer013
  Radius = 1.1
  Refine = true
  SupportTransform = false
  Suppressed = false
  UseAllEdges = false
FEATURE [PartDesign::Fillet] Fillet008
  Base = -> Fillet007 [Edge76]
  BaseFeature = -> Fillet007
  Radius = 1.9
  Refine = true
  SupportTransform = false
  Suppressed = false
  UseAllEdges = false
FEATURE [PartDesign::Pocket] Pocket011
  BaseFeature = -> Fillet008
  Direction = (0,1,-2e-16)
  Length = 0.8
  Length2 = 5
  Profile = -> Sketch132
  ReferenceAxis = -> Sketch132 [N_Axis]
  Refine = true
  Suppressed = false
  Type = 0
FEATURE [Part::Part2DObjectPython] ShapeString  # Draft 2D object (typed FeaturePython)
  FontFile = <path>
  Fuse = false
  Justification = 6
  JustificationReference = 0
  KeepLeftMargin = false
  MakeFace = true
  ObliqueAngle = 0
  Placement = pos=(-199,-3.6,-57.5) rot=(1,0,0;1.5708rad)
  ScaleToSize = true
  Size = 10
  String = AS
  Tracking = 0
FEATURE [PartDesign::Pocket] Pocket012
  BaseFeature = -> Pocket011
  Direction = (0,1,0)
  Length = 1
  Length2 = 5
  Profile = -> ShapeString
  ReferenceAxis = -> ShapeString [N_Axis]
  Refine = true
  Suppressed = false
  Type = 0
FEATURE [PartDesign::Body] Body007  label="lato DX"
  AllowCompound = false
  Group = -> [Binder001,Sketch114,Pad011,Chamfer014,Sketch115,Pocket006,Sketch116,Pad012,Sketch117,Pocket007,Sketch118,Pad013,Sketch119,Pocket008,Pad017,Chamfer009,Pocket009,Sketch123,Sketch120,Pad014,Pad018,Chamfer008,Pocket010,Sketch121,Pad015,Sketch122,Pad016,Sketch124,Sketch125,Sketch126,Sketch127,Sketch128,SubtractivePipe002,SubtractivePipe003,Sketch129,Sketch130,Clone2D001,Sketch131,SubtractiveLoft002,+11 more]
  Origin = -> Origin007
  Tip = -> Pocket012
FEATURE [Sketcher::SketchObject] Sketch133
  ArcFitTolerance = 1e-06
  AttachmentSupport = -> [Binder]
  ExternalGeometry = -> [Binder]
  FullyConstrained = true
  MakeInternals = false
  MapMode = 5
  Placement = pos=(0,9e-16,0) rot=(0,0.707107,0.707107;3.14159rad)
  sketch-geometry (30):
    g0: LineSegment StartX=0 StartY=39.2 StartZ=0 EndX=0 EndY=3.2 EndZ=0
    g1: LineSegment StartX=0 StartY=3.2 StartZ=0 EndX=82.8 EndY=3.2 EndZ=0
    g2: LineSegment StartX=82.8 StartY=3.2 StartZ=0 EndX=82.8 EndY=6.2 EndZ=0
    g3: LineSegment StartX=82.8 StartY=6.2 StartZ=0 EndX=91.752 EndY=6.2 EndZ=0
    g4: LineSegment StartX=0 StartY=39.2 StartZ=0 EndX=195.887 EndY=39.2 EndZ=0
    g5: LineSegment StartX=195.887 StartY=39.2 StartZ=0 EndX=202.765 EndY=20.303 EndZ=0
    g6: LineSegment StartX=192.333 StartY=24.9893 StartZ=0 EndX=196.467 EndY=26.4942 EndZ=0
    g7: LineSegment StartX=196.467 StartY=26.4942 StartZ=0 EndX=194.073 EndY=33.0721 EndZ=0
    g8: LineSegment StartX=194.073 StartY=33.0721 StartZ=0 EndX=189.939 EndY=31.5672 EndZ=0
    g9: LineSegment StartX=189.939 StartY=31.5672 StartZ=0 EndX=192.333 EndY=24.9893 EndZ=0
    g10: ArcOfCircle CenterX=107.6 CenterY=4 CenterZ=0 NormalX=0 NormalY=0 NormalZ=1 AngleXU=0 Radius=16 StartAngle=1.5708 EndAngle=3.00366
    g11: LineSegment StartX=107.6 StartY=20 StartZ=0 EndX=132.428 EndY=20 EndZ=0
    g12: ArcOfCircle [constr] CenterX=132.428 CenterY=4 CenterZ=0 NormalX=0 NormalY=0 NormalZ=1 AngleXU=0 Radius=16 StartAngle=0.314159 EndAngle=1.5708
    g13: LineSegment StartX=147.645 StartY=8.94427 StartZ=0 EndX=176.685 EndY=-80.4316 EndZ=0
    g14: LineSegment StartX=176.685 StartY=-80.4316 StartZ=0 EndX=215.932 EndY=-80.4316 EndZ=0
    g15: ArcOfCircle CenterX=207.583 CenterY=4 CenterZ=0 NormalX=0 NormalY=0 NormalZ=1 AngleXU=0 Radius=17 StartAngle=1.85815 EndAngle=3.57792
    g16: ArcOfCircle CenterX=184.801 CenterY=-67.3089 CenterZ=0 NormalX=0 NormalY=0 NormalZ=1 AngleXU=0 Radius=33.7833 StartAngle=5.88425 EndAngle=6.71952
    g17: LineSegment StartX=192.176 StartY=-3.18451 StartZ=0 EndX=215.42 EndY=-53.0314 EndZ=0
    g18: Circle CenterX=5.6 CenterY=34.8 CenterZ=0 NormalX=0 NormalY=0 NormalZ=1 AngleXU=0 Radius=1.8
    g19: Circle CenterX=5.6 CenterY=7.6 CenterZ=0 NormalX=0 NormalY=0 NormalZ=1 AngleXU=0 Radius=1.8
    g20: Circle CenterX=78.51 CenterY=34.8 CenterZ=0 NormalX=0 NormalY=0 NormalZ=1 AngleXU=0 Radius=1.8
    g21: Circle CenterX=78.51 CenterY=7.6 CenterZ=0 NormalX=0 NormalY=0 NormalZ=1 AngleXU=0 Radius=1.8
    g22: Circle CenterX=184.08 CenterY=34.8 CenterZ=0 NormalX=0 NormalY=0 NormalZ=1 AngleXU=0 Radius=1.8
    g23: Circle CenterX=179.305 CenterY=-76.8316 CenterZ=0 NormalX=0 NormalY=0 NormalZ=1 AngleXU=0 Radius=1.8
    g24: Circle CenterX=213.443 CenterY=-76.8316 CenterZ=0 NormalX=0 NormalY=0 NormalZ=1 AngleXU=0 Radius=1.8
    g25: Circle CenterX=19 CenterY=21.2 CenterZ=0 NormalX=0 NormalY=0 NormalZ=1 AngleXU=0 Radius=6.3
    g26: Circle CenterX=42 CenterY=21.2 CenterZ=0 NormalX=0 NormalY=0 NormalZ=1 AngleXU=0 Radius=6.3
    g27: Circle CenterX=65 CenterY=21.2 CenterZ=0 NormalX=0 NormalY=0 NormalZ=1 AngleXU=0 Radius=6.3
    g28: LineSegment StartX=132.428 StartY=20 StartZ=0 EndX=144.053 EndY=20 EndZ=0
    g29: LineSegment StartX=147.645 StartY=8.94427 StartZ=0 EndX=144.053 EndY=20 EndZ=0
  constraints (65):
    c: Coincident(g0,g-4)
    c: Coincident(g0,g-5)
    c: Coincident(g1,g0)
    c: Coincident(g1,g-6)
    c: Coincident(g2,g1)
    c: Coincident(g2,g-7)
    c: Coincident(g3,g2)
    c: Coincident(g3,g-8)
    c: Coincident(g4,g0)
    c: Coincident(g4,g-16)
    c: Coincident(g5,g4)
    c: Coincident(g5,g-16)
    c: Coincident(g6,g-20)
    c: Coincident(g6,g-21)
    c: Coincident(g7,g6)
    c: Coincident(g7,g-23)
    c: Coincident(g8,g7)
    c: Coincident(g8,g-22)
    c: Coincident(g9,g8)
    c: Coincident(g9,g6)
    c: Equal(g10,g-8)
    c: Coincident(g10,g3)
    c: Coincident(g10,g-9)
    c: Coincident(g11,g10)
    c: Coincident(g11,g-10)
    c: Equal(g12,g-10)
    c: Coincident(g12,g11)
    c: Coincident(g12,g-11)
    c: Coincident(g13,g12)
    c: Coincident(g13,g-12)
    c: Coincident(g14,g13)
    c: Coincident(g14,g-13)
    c: Equal(g15,g-15)
    c: Coincident(g15,g5)
    c: Coincident(g15,g-15)
    c: Equal(g16,g-13)
    c: Coincident(g16,g14)
    c: Coincident(g16,g-14)
    c: Coincident(g17,g15)
    c: Coincident(g17,g16)
    c: Equal(g18,g-28)
    c: Equal(g19,g-29)
    c: Equal(g20,g-26)
    c: Equal(g21,g-27)
    c: Equal(g22,g-17)
    c: Equal(g24,g-25)
    c: Equal(g23,g-24)
    c: Coincident(g23,g-24)
    c: Coincident(g24,g-25)
    c: Coincident(g22,g-17)
    c: Coincident(g20,g-26)
    c: Coincident(g21,g-27)
    c: Coincident(g18,g-28)
    c: Coincident(g19,g-29)
    c: Equal(g25,g-30)
    c: Equal(g26,g-31)
    c: Equal(g27,g-32)
    c: Coincident(g25,g-30)
    c: Coincident(g26,g-31)
    c: Coincident(g27,g-32)
    c: Parallel(g28,g11)
    c: Parallel(g29,g13)
    c: Coincident(g28,g11)
    c: Coincident(g29,g12)
    c: Coincident(g29,g28)
FEATURE [PartDesign::Pad] Pad019
  Direction = (0,1,-2e-16)
  Length = 2
  Length2 = 10
  Profile = -> Sketch133
  ReferenceAxis = -> Sketch133 [N_Axis]
  Refine = true
  Suppressed = false
  Type = 0
FEATURE [Sketcher::SketchObject] Sketch091  label="Sketch091 - forma anteriore"
  ArcFitTolerance = 1e-06
  AttachmentSupport = -> [Pad019]
  ExternalGeometry = -> [Binder]
  FullyConstrained = true
  MakeInternals = false
  MapMode = 5
  Placement = pos=(0,2,0) rot=(0,0.707107,0.707107;3.14159rad)
  sketch-geometry (12):
    g0: Circle CenterX=5.6 CenterY=34.8 CenterZ=0 NormalX=0 NormalY=0 NormalZ=1 AngleXU=0 Radius=1.8
    g1: Circle CenterX=5.6 CenterY=7.6 CenterZ=0 NormalX=0 NormalY=0 NormalZ=1 AngleXU=0 Radius=1.8
    g2: Circle CenterX=78.51 CenterY=34.8 CenterZ=0 NormalX=0 NormalY=0 NormalZ=1 AngleXU=0 Radius=1.8
    g3: Circle CenterX=78.51 CenterY=7.6 CenterZ=0 NormalX=0 NormalY=0 NormalZ=1 AngleXU=0 Radius=1.8
    g4: LineSegment StartX=0 StartY=39.2 StartZ=0 EndX=0 EndY=3.2 EndZ=0
    g5: LineSegment StartX=0 StartY=3.2 StartZ=0 EndX=82.8 EndY=3.2 EndZ=0
    g6: LineSegment StartX=82.8 StartY=3.2 StartZ=0 EndX=82.8 EndY=39.2 EndZ=0
    g7: LineSegment StartX=82.8 StartY=39.2 StartZ=0 EndX=0 EndY=39.2 EndZ=0
    g8: ArcOfCircle CenterX=19 CenterY=21.2 CenterZ=0 NormalX=0 NormalY=0 NormalZ=1 AngleXU=0 Radius=10 StartAngle=1.5708 EndAngle=4.71239
    g9: ArcOfCircle CenterX=65 CenterY=21.2 CenterZ=0 NormalX=0 NormalY=0 NormalZ=1 AngleXU=0 Radius=10 StartAngle=4.71239 EndAngle=7.85398
    g10: LineSegment StartX=19 StartY=31.2 StartZ=0 EndX=65 EndY=31.2 EndZ=0
    g11: LineSegment StartX=19 StartY=11.2 StartZ=0 EndX=65 EndY=11.2 EndZ=0
  constraints (25):
    c: Equal(g2,g-7)
    c: Equal(g3,g-8)
    c: Equal(g1,g-13)
    c: Equal(g0,g-12)
    c: Coincident(g0,g-12)
    c: Coincident(g1,g-13)
    c: Coincident(g3,g-8)
    c: Coincident(g2,g-7)
    c: Coincident(g4,g-4)
    c: Coincident(g4,g-5)
    c: Coincident(g5,g4)
    c: Coincident(g5,g-6)
    c: Coincident(g6,g5)
    c: PointOnObject(g6,g-3)
    c: Vertical(g6)
    c: Coincident(g7,g6)
    c: Coincident(g7,g4)
    c: Tangent(g8,g10) = 1.5708
    c: Tangent(g8,g11) = -1.5708
    c: Tangent(g9,g10) = 1.5708
    c: Tangent(g9,g11) = -1.5708
    c: Equal(g8,g9)
    c: Radius(g8) = 10
    c: Coincident(g8,g-11)
    c: Coincident(g9,g-9)
FEATURE [Sketcher::SketchObject] Sketch093  label="Sketch093 - scavi interni pulsanti"
  ArcFitTolerance = 1e-06
  AttachmentSupport = -> [Pad019]
  ExternalGeometry = -> [Binder]
  FullyConstrained = true
  MakeInternals = false
  MapMode = 5
  Placement = pos=(0,1.8e-15,0) rot=(1,0,0;1.5708rad)
  sketch-geometry (3):
    g0: Circle CenterX=-65 CenterY=21.2 CenterZ=0 NormalX=0 NormalY=0 NormalZ=1 AngleXU=0 Radius=7.3
    g1: Circle CenterX=-42 CenterY=21.2 CenterZ=0 NormalX=0 NormalY=0 NormalZ=1 AngleXU=0 Radius=7.3
    g2: Circle CenterX=-19 CenterY=21.2 CenterZ=0 NormalX=0 NormalY=0 NormalZ=1 AngleXU=0 Radius=7.3
  constraints (6):
    c: Coincident(g0,g-3)
    c: Coincident(g1,g-4)
    c: Coincident(g2,g-5)
    c: Diameter(g0) = 14.6
    c: Diameter(g1) = 14.6
    c: Diameter(g2) = 14.6
FEATURE [Sketcher::SketchObject] Sketch094  label="Sketch094 - forma centrale"
  ArcFitTolerance = 1e-06
  AttachmentSupport = -> [Pad019]
  ExternalGeometry = -> [Binder]
  FullyConstrained = true
  MakeInternals = false
  MapMode = 5
  Placement = pos=(0,2,0) rot=(0,0.707107,0.707107;3.14159rad)
  sketch-geometry (4):
    g0: LineSegment StartX=137.815 StartY=39.2 StartZ=0 EndX=142.655 EndY=24.303 EndZ=0
    g1: LineSegment StartX=110.815 StartY=24.303 StartZ=0 EndX=142.655 EndY=24.303 EndZ=0
    g2: LineSegment StartX=137.815 StartY=39.2 StartZ=0 EndX=110.815 EndY=39.2 EndZ=0
    g3: ArcOfCircle CenterX=92.2534 CenterY=31.7515 CenterZ=0 NormalX=0 NormalY=0 NormalZ=1 AngleXU=0 Radius=20 StartAngle=5.90156 EndAngle=6.66481
  constraints (12):
    c: PointOnObject(g0,g-3)
    c: Tangent(g0,g-5)
    c: Horizontal(g1)
    c: Coincident(g1,g0)
    c: Coincident(g2,g0)
    c: PointOnObject(g2,g-3)
    c: DistanceX(g2,g2) = 27
    c: Vertical(g1,g2)
    c: Coincident(g3,g2)
    c: Radius(g3) = 20
    c: Coincident(g3,g1)
    c: DistanceY(g-6,g0) = 4
FEATURE [Sketcher::SketchObject] Sketch095  label="Sketch095 - forma posteriore"
  ArcFitTolerance = 1e-06
  AttachmentSupport = -> [Pad019]
  ExternalGeometry = -> [Binder]
  FullyConstrained = true
  MakeInternals = false
  MapMode = 5
  Placement = pos=(0,2,0) rot=(0,0.707107,0.707107;3.14159rad)
  sketch-geometry (15):
    g0: LineSegment StartX=137.815 StartY=39.2 StartZ=0 EndX=143.955 EndY=20.303 EndZ=0
    g1: LineSegment StartX=143.955 StartY=20.303 StartZ=0 EndX=190.141 EndY=20.303 EndZ=0
    g2: ArcOfCircle CenterX=184.08 CenterY=34.8 CenterZ=0 NormalX=0 NormalY=0 NormalZ=1 AngleXU=0 Radius=3.5 StartAngle=3.49066 EndAngle=4.71239
    g3: LineSegment StartX=180.791 StartY=33.6029 StartZ=0 EndX=178.754 EndY=39.2 EndZ=0
    g4: LineSegment StartX=184.08 StartY=31.3 StartZ=0 EndX=186.139 EndY=31.3 EndZ=0
    g5: LineSegment StartX=190.141 StartY=20.303 StartZ=0 EndX=186.139 EndY=31.3 EndZ=0
    g6: LineSegment StartX=137.815 StartY=39.2 StartZ=0 EndX=156.815 EndY=39.2 EndZ=0
    g7: LineSegment StartX=178.754 StartY=39.2 StartZ=0 EndX=168.815 EndY=39.2 EndZ=0
    g8: LineSegment StartX=156.815 StartY=31.2 StartZ=0 EndX=168.815 EndY=31.2 EndZ=0
    g9: ArcOfCircle CenterX=176.411 CenterY=35.2 CenterZ=0 NormalX=0 NormalY=0 NormalZ=1 AngleXU=0 Radius=20 StartAngle=2.94023 EndAngle=3.34295
    g10: ArcOfCircle CenterX=188.411 CenterY=35.2 CenterZ=0 NormalX=0 NormalY=0 NormalZ=1 AngleXU=0 Radius=20 StartAngle=2.94023 EndAngle=3.34295
    g11: LineSegment StartX=157.815 StartY=39.2 StartZ=0 EndX=167.815 EndY=39.2 EndZ=0
    g12: LineSegment StartX=157.436 StartY=36.2 StartZ=0 EndX=167.436 EndY=36.2 EndZ=0
    g13: ArcOfCircle CenterX=177.411 CenterY=35.2 CenterZ=0 NormalX=0 NormalY=0 NormalZ=1 AngleXU=0 Radius=20 StartAngle=2.94023 EndAngle=3.09157
    g14: ArcOfCircle CenterX=187.411 CenterY=35.2 CenterZ=0 NormalX=0 NormalY=0 NormalZ=1 AngleXU=0 Radius=20 StartAngle=2.94023 EndAngle=3.09157
  constraints (46):
    c: PointOnObject(g0,g-3)
    c: Tangent(g0,g-6)
    c: Coincident(g1,g0)
    c: Horizontal(g1)
    c: Radius(g2) = 3.5
    c: Coincident(g2,g-5)
    c: PointOnObject(g3,g-3)
    c: Parallel(g3,g-4)
    c: Tangent(g3,g2) = 1.5708
    c: Horizontal(g4)
    c: Tangent(g4,g2) = -1.5708
    c: Coincident(g5,g1)
    c: Parallel(g5,g-4)
    c: Coincident(g5,g4)
    c: DistanceX(g4,g-8) = 3.8
    c: Coincident(g6,g0)
    c: PointOnObject(g6,g-3)
    c: Coincident(g7,g3)
    c: PointOnObject(g7,g-3)
    c: Horizontal(g8)
    c: DistanceX(g6,g7) = 12
    c: Vertical(g8,g6)
    c: Vertical(g7,g8)
    c: DistanceY(g8,g6) = 8
    c: Coincident(g9,g8)
    c: Coincident(g9,g6)
    c: Coincident(g10,g7)
    c: Coincident(g10,g8)
    c: Radius(g9) = 20
    c: Radius(g10) = 20
    c: PointOnObject(g11,g-3)
    c: PointOnObject(g11,g-3)
    c: DistanceX(g11,g11) = 10
    c: DistanceX(g6,g11) = 1
    c: Horizontal(g12)
    c: Equal(g12,g11)
    c: DistanceY(g12,g11) = 3
    c: Coincident(g13,g11)
    c: Coincident(g13,g12)
    c: Radius(g13) = 20
    c: Coincident(g14,g11)
    c: Coincident(g14,g12)
    c: Radius(g14) = 20
    c: DistanceX(g0,g6) = 19
    c: Horizontal(g9,g13)
    c: Horizontal(g0,g-4)
FEATURE [Sketcher::SketchObject] Sketch096  label="Sketch096 - forma impugnatura"
  ArcFitTolerance = 1e-06
  AttachmentSupport = -> [Pad019]
  ExternalGeometry = -> [Binder]
  FullyConstrained = true
  MakeInternals = false
  MapMode = 5
  Placement = pos=(0,2,0) rot=(0,0.707107,0.707107;3.14159rad)
  sketch-geometry (8):
    g0: LineSegment StartX=176.685 StartY=-80.4316 StartZ=0 EndX=143.955 EndY=20.303 EndZ=0
    g1: LineSegment StartX=176.685 StartY=-80.4316 StartZ=0 EndX=215.932 EndY=-80.4316 EndZ=0
    g2: Circle CenterX=179.305 CenterY=-76.8316 CenterZ=0 NormalX=0 NormalY=0 NormalZ=1 AngleXU=0 Radius=3
    g3: Circle CenterX=213.443 CenterY=-76.8316 CenterZ=0 NormalX=0 NormalY=0 NormalZ=1 AngleXU=0 Radius=3
    g4: LineSegment StartX=143.955 StartY=20.303 StartZ=0 EndX=202.765 EndY=20.303 EndZ=0
    g5: LineSegment StartX=215.42 StartY=-53.0314 StartZ=0 EndX=192.176 EndY=-3.18451 EndZ=0
    g6: ArcOfCircle CenterX=184.801 CenterY=-67.3089 CenterZ=0 NormalX=0 NormalY=0 NormalZ=1 AngleXU=0 Radius=33.7833 StartAngle=5.88425 EndAngle=6.71952
    g7: ArcOfCircle CenterX=207.583 CenterY=4 CenterZ=0 NormalX=0 NormalY=0 NormalZ=1 AngleXU=0 Radius=17 StartAngle=1.85815 EndAngle=3.57792
  constraints (19):
    c: Coincident(g0,g-4)
    c: PointOnObject(g0,g-3)
    c: Horizontal(g0,g-7)
    c: Coincident(g1,g0)
    c: Coincident(g1,g-5)
    c: Diameter(g2) = 6
    c: Diameter(g3) = 6
    c: Coincident(g2,g-9)
    c: Coincident(g3,g-10)
    c: Coincident(g4,g0)
    c: Coincident(g5,g-6)
    c: Coincident(g6,g1)
    c: Coincident(g6,g5)
    c: Equal(g-5,g6)
    c: Coincident(g5,g-7)
    c: Coincident(g4,g-7)
    c: Tangent(g7,g-7)
    c: Coincident(g7,g4)
    c: Coincident(g7,g5)
FEATURE [Sketcher::SketchObject] Sketch097
  ArcFitTolerance = 1e-06
  AttachmentSupport = -> [Pad019]
  ExternalGeometry = -> [Binder]
  FullyConstrained = true
  MakeInternals = false
  MapMode = 5
  Placement = pos=(0,2,0) rot=(0,0.707107,0.707107;3.14159rad)
  sketch-geometry (4):
    g0: LineSegment StartX=90 StartY=36.8 StartZ=0 EndX=108 EndY=36.8 EndZ=0
    g1: LineSegment StartX=108 StartY=36.8 StartZ=0 EndX=108 EndY=26.8 EndZ=0
    g2: LineSegment StartX=108 StartY=26.8 StartZ=0 EndX=90 EndY=26.8 EndZ=0
    g3: ArcOfCircle CenterX=94 CenterY=31.8 CenterZ=0 NormalX=0 NormalY=0 NormalZ=1 AngleXU=0 Radius=6.40312 StartAngle=2.24554 EndAngle=4.03765
  constraints (13):
    c: Horizontal(g0)
    c: Coincident(g1,g0)
    c: Vertical(g1)
    c: DistanceX(g0,g0) = 18
    c: DistanceY(g1,g1) = 10
    c: Coincident(g2,g1)
    c: Horizontal(g2)
    c: Equal(g2,g0)
    c: DistanceY(g0,g-3) = 2.4
    c: Coincident(g3,g0)
    c: Coincident(g3,g2)
    c: DistanceX(g2,g3) = 4
    c: DistanceX(g-3,g0) = 90
FEATURE [PartDesign::Chamfer] Chamfer015
  Angle = 45
  Base = -> Pad019 [Edge19,Edge22,Edge79]
  BaseFeature = -> Pad019
  ChamferType = 0
  FlipDirection = false
  Refine = true
  Size = 1.9
  Size2 = 1
  SupportTransform = false
  Suppressed = false
  UseAllEdges = false
FEATURE [PartDesign::Pocket] Pocket002
  BaseFeature = -> Chamfer015
  Direction = (0,1,-2e-16)
  Length = 1.2
  Length2 = 5
  Profile = -> Sketch093
  ReferenceAxis = -> Sketch093 [N_Axis]
  Refine = true
  Suppressed = false
  Type = 0
FEATURE [PartDesign::Pad] Pad005
  BaseFeature = -> Pocket002
  Direction = (0,1,-2e-16)
  Length = 1.6
  Length2 = 10
  Profile = -> Sketch091
  ReferenceAxis = -> Sketch091 [N_Axis]
  Refine = true
  Suppressed = false
  Type = 0
FEATURE [Sketcher::SketchObject] Sketch092  label="Sketch092 - scavi per viti anteriori"
  ArcFitTolerance = 1e-06
  AttachmentSupport = -> [Pad005]
  ExternalGeometry = -> [Binder]
  FullyConstrained = true
  MakeInternals = false
  MapMode = 5
  Placement = pos=(0,3.6,0) rot=(0,0.707107,0.707107;3.14159rad)
  sketch-geometry (20):
    g0: ArcOfCircle CenterX=5.6 CenterY=7.6 CenterZ=0 NormalX=0 NormalY=0 NormalZ=1 AngleXU=0 Radius=3.5 StartAngle=0 EndAngle=1.5708
    g1: ArcOfCircle CenterX=5.6 CenterY=34.8 CenterZ=0 NormalX=0 NormalY=0 NormalZ=1 AngleXU=0 Radius=3.5 StartAngle=4.71239 EndAngle=6.28319
    g2: ArcOfCircle CenterX=78.51 CenterY=34.8 CenterZ=0 NormalX=0 NormalY=0 NormalZ=1 AngleXU=0 Radius=3.5 StartAngle=3.14159 EndAngle=4.71239
    g3: ArcOfCircle CenterX=78.51 CenterY=7.6 CenterZ=0 NormalX=0 NormalY=0 NormalZ=1 AngleXU=0 Radius=3.5 StartAngle=1.5708 EndAngle=3.14159
    g4: LineSegment StartX=0 StartY=3.2 StartZ=0 EndX=0 EndY=11.1 EndZ=0
    g5: LineSegment StartX=0 StartY=11.1 StartZ=0 EndX=5.6 EndY=11.1 EndZ=0
    g6: LineSegment StartX=0 StartY=3.2 StartZ=0 EndX=9.1 EndY=3.2 EndZ=0
    g7: LineSegment StartX=9.1 StartY=3.2 StartZ=0 EndX=9.1 EndY=7.6 EndZ=0
    g8: LineSegment StartX=0 StartY=39.2 StartZ=0 EndX=0 EndY=31.3 EndZ=0
    g9: LineSegment StartX=0 StartY=31.3 StartZ=0 EndX=5.6 EndY=31.3 EndZ=0
    g10: LineSegment StartX=0 StartY=39.2 StartZ=0 EndX=9.1 EndY=39.2 EndZ=0
    g11: LineSegment StartX=9.1 StartY=39.2 StartZ=0 EndX=9.1 EndY=34.8 EndZ=0
    g12: LineSegment StartX=82.8 StartY=39.2 StartZ=0 EndX=75.01 EndY=39.2 EndZ=0
    g13: LineSegment StartX=82.8 StartY=39.2 StartZ=0 EndX=82.8 EndY=31.3 EndZ=0
    g14: LineSegment StartX=82.8 StartY=31.3 StartZ=0 EndX=78.51 EndY=31.3 EndZ=0
    g15: LineSegment StartX=82.8 StartY=3.2 StartZ=0 EndX=75.01 EndY=3.2 EndZ=0
    g16: LineSegment StartX=75.01 StartY=3.2 StartZ=0 EndX=75.01 EndY=7.6 EndZ=0
    g17: LineSegment StartX=82.8 StartY=3.2 StartZ=0 EndX=82.8 EndY=11.1 EndZ=0
    g18: LineSegment StartX=82.8 StartY=11.1 StartZ=0 EndX=78.51 EndY=11.1 EndZ=0
    g19: LineSegment StartX=75.01 StartY=39.2 StartZ=0 EndX=75.01 EndY=34.8 EndZ=0
  constraints (48):
    c: Radius(g0) = 3.5
    c: Coincident(g0,g-10)
    c: Radius(g1) = 3.5
    c: Coincident(g1,g-9)
    c: Radius(g2) = 3.5
    c: Coincident(g2,g-8)
    c: Radius(g3) = 3.5
    c: Coincident(g3,g-7)
    c: Coincident(g4,g-5)
    c: PointOnObject(g4,g-4)
    c: Coincident(g5,g4)
    c: Horizontal(g5)
    c: Coincident(g6,g4)
    c: PointOnObject(g6,g-5)
    c: Coincident(g7,g6)
    c: Vertical(g7)
    c: Coincident(g8,g-4)
    c: PointOnObject(g8,g-4)
    c: Coincident(g9,g8)
    c: Horizontal(g9)
    c: Coincident(g10,g8)
    c: PointOnObject(g10,g-3)
    c: Coincident(g11,g10)
    c: Vertical(g11)
    c: PointOnObject(g12,g-3)
    c: PointOnObject(g12,g-3)
    c: Coincident(g13,g12)
    c: Vertical(g13)
    c: Coincident(g14,g13)
    c: Horizontal(g14)
    c: Coincident(g15,g-6)
    c: PointOnObject(g15,g-5)
    c: Coincident(g16,g15)
    c: Vertical(g16)
    c: Coincident(g17,g15)
    c: Coincident(g18,g17)
    c: Horizontal(g18)
    c: Tangent(g3,g18) = -1.5708
    c: Tangent(g16,g3) = 1.5708
    c: Coincident(g19,g12)
    c: Vertical(g19)
    c: Tangent(g2,g19) = -1.5708
    c: Tangent(g2,g14) = 1.5708
    c: Tangent(g0,g7) = -1.5708
    c: Tangent(g0,g5) = 1.5708
    c: Tangent(g9,g1) = -1.5708
    c: Tangent(g1,g11) = 1.5708
    c: Tangent(g17,g13)
FEATURE [PartDesign::Pocket] Pocket001
  BaseFeature = -> Pad005
  Direction = (0,-1,2e-16)
  Length = 1.6
  Length2 = 5
  Profile = -> Sketch092
  ReferenceAxis = -> Sketch092 [N_Axis]
  Refine = true
  Suppressed = false
  Type = 0
FEATURE [PartDesign::Pad] Pad006
  BaseFeature = -> Pocket001
  Direction = (0,1,-2e-16)
  Length = 0.8
  Length2 = 10
  Profile = -> Sketch094
  ReferenceAxis = -> Sketch094 [N_Axis]
  Refine = true
  Suppressed = false
  Type = 0
FEATURE [PartDesign::Pad] Pad007
  BaseFeature = -> Pad006
  Direction = (0,1,-2e-16)
  Length = 2
  Length2 = 10
  Profile = -> Sketch095
  ReferenceAxis = -> Sketch095 [N_Axis]
  Refine = true
  Suppressed = false
  Type = 0
FEATURE [PartDesign::Pad] Pad008  label="Pad008 - forma impugnatura"
  BaseFeature = -> Pad007
  Direction = (0,1,-2e-16)
  Length = 1.6
  Length2 = 10
  Profile = -> Sketch096
  ReferenceAxis = -> Sketch096 [N_Axis]
  Refine = true
  Suppressed = false
  Type = 0
FEATURE [PartDesign::Pad] Pad009
  BaseFeature = -> Pad008
  Direction = (0,1,-2e-16)
  Length = 1.6
  Length2 = 10
  Profile = -> Sketch097
  ReferenceAxis = -> Sketch097 [N_Axis]
  Refine = true
  Suppressed = false
  Type = 0
FEATURE [Sketcher::SketchObject] Sketch098
  ArcFitTolerance = 1e-06
  AttachmentSupport = -> [Pad006]
  ExternalGeometry = -> [Binder]
  FullyConstrained = true
  MakeInternals = false
  MapMode = 5
  Placement = pos=(0,2.8,-7e-16) rot=(0,0.707107,0.707107;3.14159rad)
  sketch-geometry (4):
    g0: LineSegment StartX=118 StartY=39.2 StartZ=0 EndX=129 EndY=39.2 EndZ=0
    g1: LineSegment StartX=120.599 StartY=31.2 StartZ=0 EndX=131.599 EndY=31.2 EndZ=0
    g2: LineSegment StartX=129 StartY=39.2 StartZ=0 EndX=131.599 EndY=31.2 EndZ=0
    g3: LineSegment StartX=118 StartY=39.2 StartZ=0 EndX=120.599 EndY=31.2 EndZ=0
  constraints (12):
    c: PointOnObject(g0,g-3)
    c: PointOnObject(g0,g-3)
    c: DistanceX(g0,g0) = 11
    c: Horizontal(g1)
    c: Equal(g1,g0)
    c: Coincident(g2,g0)
    c: Coincident(g3,g0)
    c: Parallel(g-4,g2)
    c: Coincident(g1,g2)
    c: Coincident(g1,g3)
    c: DistanceY(g1,g0) = 8
    c: DistanceX(g-3,g0) = 118
FEATURE [Sketcher::SketchObject] Sketch099
  ArcFitTolerance = 1e-06
  AttachmentSupport = -> [Pad008]
  ExternalGeometry = -> [Binder]
  FullyConstrained = true
  MakeInternals = false
  MapMode = 5
  Placement = pos=(0,3.6,0) rot=(0,0.707107,0.707107;3.14159rad)
  sketch-geometry (13):
    g0: LineSegment StartX=192.176 StartY=-3.18451 StartZ=0 EndX=196.804 EndY=-13.1108 EndZ=0
    g1: LineSegment [constr] StartX=202.765 StartY=20.303 StartZ=0 EndX=181.223 EndY=20.303 EndZ=0
    g2: LineSegment [constr] StartX=181.223 StartY=20.303 StartZ=0 EndX=181.223 EndY=-3.18451 EndZ=0
    g3: ArcOfCircle CenterX=181.223 CenterY=-20.3764 CenterZ=0 NormalX=0 NormalY=0 NormalZ=1 AngleXU=0 Radius=17.1918 StartAngle=0.436332 EndAngle=1.57079
    g4: ArcOfEllipse CenterX=181.223 CenterY=8.55923 CenterZ=0 NormalX=0 NormalY=0 NormalZ=1 MajorRadius=23.4779 MinorRadius=11.7437 AngleXU=0 StartAngle=1.5708 EndAngle=4.71239
    g5: LineSegment [constr] StartX=204.701 StartY=8.55923 StartZ=0 EndX=157.745 EndY=8.55923 EndZ=0
    g6: LineSegment [constr] StartX=181.223 StartY=20.303 StartZ=0 EndX=181.223 EndY=-3.18451 EndZ=0
    g7: GeomPoint [constr] X=201.553 Y=8.55923 Z=0
    g8: GeomPoint [constr] X=160.894 Y=8.55923 Z=0
    g9: GeomPoint [constr] X=181.223 Y=-3.18451 Z=0
    g10: LineSegment StartX=181.223 StartY=20.303 StartZ=0 EndX=202.765 EndY=20.303 EndZ=0
    g11: ArcOfCircle CenterX=207.583 CenterY=4 CenterZ=0 NormalX=0 NormalY=0 NormalZ=1 AngleXU=0 Radius=17 StartAngle=1.85815 EndAngle=3.57792
    g12: LineSegment [constr] StartX=172.411 StartY=39.2 StartZ=0 EndX=192.176 EndY=-3.18451 EndZ=0
  constraints (27):
    c: Coincident(g1,g-7)
    c: Horizontal(g1)
    c: Coincident(g2,g1)
    c: Vertical(g2)
    c: Horizontal(g2,g0)
    c: Coincident(g3,g0)
    c: Coincident(g3,g2)
    c: InternalAlignment(g5-g8 -> g4) x4
    c: Horizontal(g5)
    c: PointOnObject(g4,g2)
    c: Coincident(g4,g1)
    c: DistanceX(g-3,g5) = 10.1
    c: Coincident(g4,g2)
    c: Tangent(g3,g-5)
    c: PointOnObject(g9,g4)
    c: PointOnObject(g9,g3)
    c: Tangent(g4,g3,g9) = 1.5708
    c: Coincident(g10,g1)
    c: Coincident(g10,g1)
    c: Equal(g11,g-4)
    c: Coincident(g11,g1)
    c: Coincident(g11,g0)
    c: PointOnObject(g12,g-6)
    c: PointOnObject(g1,g12)
    c: Tangent(g12,g-5) = -1.5708
    c: Tangent(g0,g-5) = -1.5708
    c: Horizontal(g9,g12)
FEATURE [Sketcher::SketchObject] Sketch106  label="Sketch106 - smusso impuniatura interno"
  ArcFitTolerance = 1e-06
  AttachmentSupport = -> [Pad008]
  ExternalGeometry = -> [Pad008]
  FullyConstrained = true
  MakeInternals = false
  MapMode = 5
  Placement = pos=(0,-1.585e-13,-80.4316) rot=(1,0,0;3.14159rad)
  sketch-geometry (9):
    g0: LineSegment StartX=-176.685 StartY=-3.6 StartZ=0 EndX=-176.685 EndY=-1.452e-13 EndZ=0
    g1: LineSegment [constr] StartX=-176.685 StartY=-1.416e-13 StartZ=0 EndX=-176.685 EndY=-1.452e-13 EndZ=0
    g2: LineSegment [constr] StartX=-186.685 StartY=-3.6 StartZ=0 EndX=-186.685 EndY=-1.452e-13 EndZ=0
    g3: ArcOfEllipse CenterX=-186.685 CenterY=-1.452e-13 CenterZ=0 NormalX=0 NormalY=0 NormalZ=1 MajorRadius=10 MinorRadius=3.6 AngleXU=3.14159 StartAngle=1.5708 EndAngle=3.14159
    g4: LineSegment [constr] StartX=-196.685 StartY=-1.416e-13 StartZ=0 EndX=-176.685 EndY=-1.416e-13 EndZ=0
    g5: LineSegment [constr] StartX=-186.685 StartY=-3.6 StartZ=0 EndX=-186.685 EndY=3.6 EndZ=0
    g6: GeomPoint [constr] X=-196.015 Y=-1.416e-13 Z=0
    g7: GeomPoint [constr] X=-177.356 Y=-1.416e-13 Z=0
    g8: LineSegment StartX=-176.685 StartY=-3.6 StartZ=0 EndX=-186.685 EndY=-3.6 EndZ=0
  constraints (15):
    c: PointOnObject(g2,g-3)
    c: Coincident(g1,g-5)
    c: DistanceY(g1,g1) = 0
    c: Coincident(g0,g1)
    c: DistanceX(g2,g-5) = 10
    c: Vertical(g2)
    c: Horizontal(g2,g0)
    c: InternalAlignment(g4-g7 -> g3) x4
    c: Coincident(g3,g2)
    c: Horizontal(g4)
    c: Coincident(g3,g0)
    c: Tangent(g0,g-5) = 1.5708
    c: Coincident(g3,g2)
    c: Coincident(g8,g0)
    c: Coincident(g8,g2)
FEATURE [Sketcher::SketchObject] Sketch107  label="Sketch107 - smusso impugnatura esterno"
  ArcFitTolerance = 1e-06
  AttachmentSupport = -> [Pad008]
  ExternalGeometry = -> [Pad008]
  FullyConstrained = true
  MakeInternals = false
  MapMode = 5
  Placement = pos=(0,-1.585e-13,-80.4316) rot=(1,0,0;3.14159rad)
  sketch-geometry (9):
    g0: LineSegment [constr] StartX=-215.932 StartY=1.79e-14 StartZ=0 EndX=-215.932 EndY=2.34e-14 EndZ=0
    g1: LineSegment StartX=-215.932 StartY=-3.6 StartZ=0 EndX=-215.932 EndY=2.35e-14 EndZ=0
    g2: LineSegment StartX=-215.932 StartY=-3.6 StartZ=0 EndX=-205.932 EndY=-3.6 EndZ=0
    g3: LineSegment [constr] StartX=-205.932 StartY=-3.6 StartZ=0 EndX=-205.932 EndY=2.35e-14 EndZ=0
    g4: ArcOfEllipse CenterX=-205.932 CenterY=2.34e-14 CenterZ=0 NormalX=0 NormalY=0 NormalZ=1 MajorRadius=10 MinorRadius=3.6 AngleXU=3.14159 StartAngle=1e-16 EndAngle=1.5708
    g5: LineSegment [constr] StartX=-215.932 StartY=1.79e-14 StartZ=0 EndX=-195.932 EndY=1.79e-14 EndZ=0
    g6: LineSegment [constr] StartX=-205.932 StartY=-3.6 StartZ=0 EndX=-205.932 EndY=3.6 EndZ=0
    g7: GeomPoint [constr] X=-215.262 Y=2.37e-14 Z=0
    g8: GeomPoint [constr] X=-196.602 Y=1.78e-14 Z=0
  constraints (16):
    c: Coincident(g0,g-6)
    c: PointOnObject(g0,g-6)
    c: DistanceY(g0,g0) = 0
    c: Coincident(g1,g-6)
    c: Coincident(g1,g0)
    c: Tangent(g2,g-3)
    c: DistanceX(g2,g2) = 10
    c: Coincident(g3,g2)
    c: Vertical(g3)
    c: Horizontal(g3,g0)
    c: InternalAlignment(g5-g8 -> g4) x4
    c: Coincident(g4,g3)
    c: Horizontal(g5)
    c: Coincident(g4,g0)
    c: Coincident(g4,g2)
    c: PointOnObject(g2,g1)
FEATURE [Sketcher::SketchObject] Sketch108
  ArcFitTolerance = 1e-06
  AttachmentOffset = pos=(0,0,-1.6) rot=(0,0,1;0rad)
  AttachmentSupport = -> [Pad008]
  ExternalGeometry = -> [Binder]
  FullyConstrained = true
  MakeInternals = false
  MapMode = 5
  Placement = pos=(0,2,4e-16) rot=(0,0.707107,0.707107;3.14159rad)
  sketch-geometry (14):
    g0: LineSegment StartX=192.176 StartY=-3.18451 StartZ=0 EndX=193.827 EndY=-6.72678 EndZ=0
    g1: LineSegment [constr] StartX=202.765 StartY=20.303 StartZ=0 EndX=181.223 EndY=20.303 EndZ=0
    g2: LineSegment [constr] StartX=181.223 StartY=20.303 StartZ=0 EndX=181.223 EndY=1.30297 EndZ=0
    g3: ArcOfCircle CenterX=181.223 CenterY=-12.6042 CenterZ=0 NormalX=0 NormalY=0 NormalZ=1 AngleXU=0 Radius=13.9072 StartAngle=0.436332 EndAngle=1.5708
    g4: ArcOfEllipse CenterX=181.223 CenterY=10.803 CenterZ=0 NormalX=0 NormalY=0 NormalZ=1 MajorRadius=14.4779 MinorRadius=9.5 AngleXU=0 StartAngle=1.5708 EndAngle=4.71239
    g5: LineSegment [constr] StartX=195.701 StartY=10.803 StartZ=0 EndX=166.745 EndY=10.803 EndZ=0
    g6: LineSegment [constr] StartX=181.223 StartY=20.303 StartZ=0 EndX=181.223 EndY=1.30297 EndZ=0
    g7: GeomPoint [constr] X=192.148 Y=10.803 Z=0
    g8: GeomPoint [constr] X=170.298 Y=10.803 Z=0
    g9: LineSegment StartX=181.223 StartY=20.303 StartZ=0 EndX=202.765 EndY=20.303 EndZ=0
    g10: ArcOfCircle CenterX=207.583 CenterY=4 CenterZ=0 NormalX=0 NormalY=0 NormalZ=1 AngleXU=0 Radius=17 StartAngle=1.85815 EndAngle=3.57792
    g11: LineSegment [constr] StartX=172.411 StartY=39.2 StartZ=0 EndX=192.176 EndY=-3.18451 EndZ=0
    g12: GeomPoint [constr] X=181.223 Y=1.30297 Z=0
    g13: GeomPoint [constr] X=181.223 Y=1.30297 Z=0
  constraints (28):
    c: Coincident(g1,g-7)
    c: Horizontal(g1)
    c: Coincident(g2,g1)
    c: Vertical(g2)
    c: Coincident(g3,g2)
    c: InternalAlignment(g5-g8 -> g4) x4
    c: Horizontal(g5)
    c: PointOnObject(g4,g2)
    c: Coincident(g4,g1)
    c: DistanceX(g-3,g5) = 19.1
    c: Coincident(g4,g2)
    c: Coincident(g9,g1)
    c: Coincident(g9,g1)
    c: Coincident(g10,g1)
    c: Coincident(g10,g0)
    c: PointOnObject(g11,g-6)
    c: PointOnObject(g1,g11)
    c: DistanceY(g2,g1) = 19
    c: Coincident(g10,g-4)
    c: PointOnObject(g12,g4)
    c: PointOnObject(g12,g3)
    c: Tangent(g11,g-5) = -1.5708
    c: Tangent(g0,g-5) = -1.5708
    c: Tangent(g3,g0) = 1.5708
    c: PointOnObject(g13,g4)
    c: PointOnObject(g13,g3)
    c: Tangent(g4,g3,g13) = 1.5708
    c: Horizontal(g11,g0)
FEATURE [Part::Part2DObjectPython] Clone2D  label="Sketch108 (2D)"  # Draft 2D object (typed FeaturePython)
  Fuse = false
  Objects = -> [Sketch108]
  Placement = pos=(0,2,4e-16) rot=(0,0.707107,0.707107;3.14159rad)
  Scale = (1,1,1)
FEATURE [Sketcher::SketchObject] Sketch109
  ArcFitTolerance = 1e-06
  AttachmentOffset = pos=(0,0,-3.5) rot=(0,0,1;0rad)
  AttachmentSupport = -> [Pad008]
  ExternalGeometry = -> [Binder]
  FullyConstrained = true
  MakeInternals = false
  MapMode = 5
  Placement = pos=(0,0.1,8e-16) rot=(0,0.707107,0.707107;3.14159rad)
  sketch-geometry (1):
    g0: GeomPoint X=197.47 Y=8.55923 Z=0
  constraints (1):
    c: Symmetric(g-7,g-5,g0)
FEATURE [PartDesign::Chamfer] Chamfer005
  Angle = 45
  Base = -> Pad009 [Edge215,Edge212]
  BaseFeature = -> Pad009
  ChamferType = 1
  FlipDirection = false
  Refine = true
  Size = 1.5
  Size2 = 2.8
  SupportTransform = false
  Suppressed = false
  UseAllEdges = false
FEATURE [Sketcher::SketchObject] Sketch111
  ArcFitTolerance = 1e-06
  AttachmentSupport = -> [Pad009]
  ExternalGeometry = -> [Pad009]
  FullyConstrained = true
  MakeInternals = false
  MapMode = 5
  Placement = pos=(0,3.6,-8e-16) rot=(0,0.707107,0.707107;3.14159rad)
  sketch-geometry (21):
    g0: LineSegment [constr] StartX=97 StartY=36.8 StartZ=0 EndX=97 EndY=26.8 EndZ=0
    g1: LineSegment StartX=97 StartY=28.6 StartZ=0 EndX=97 EndY=27.8 EndZ=0
    g2: LineSegment StartX=97 StartY=27.8 StartZ=0 EndX=108 EndY=27.8 EndZ=0
    g3: LineSegment StartX=108 StartY=27.8 StartZ=0 EndX=108 EndY=28.6 EndZ=0
    g4: LineSegment StartX=108 StartY=28.6 StartZ=0 EndX=97 EndY=28.6 EndZ=0
    g5: LineSegment StartX=97 StartY=35.8 StartZ=0 EndX=97 EndY=35 EndZ=0
    g6: LineSegment StartX=97 StartY=35 StartZ=0 EndX=108 EndY=35 EndZ=0
    g7: LineSegment StartX=108 StartY=35 StartZ=0 EndX=108 EndY=35.8 EndZ=0
    g8: LineSegment StartX=108 StartY=35.8 StartZ=0 EndX=97 EndY=35.8 EndZ=0
    g9: LineSegment StartX=97 StartY=30.4 StartZ=0 EndX=97 EndY=29.6 EndZ=0
    g10: LineSegment StartX=97 StartY=29.6 StartZ=0 EndX=108 EndY=29.6 EndZ=0
    g11: LineSegment StartX=108 StartY=29.6 StartZ=0 EndX=108 EndY=30.4 EndZ=0
    g12: LineSegment StartX=108 StartY=30.4 StartZ=0 EndX=97 EndY=30.4 EndZ=0
    g13: LineSegment StartX=97 StartY=34 StartZ=0 EndX=97 EndY=33.2 EndZ=0
    g14: LineSegment StartX=97 StartY=33.2 StartZ=0 EndX=108 EndY=33.2 EndZ=0
    g15: LineSegment StartX=108 StartY=33.2 StartZ=0 EndX=108 EndY=34 EndZ=0
    g16: LineSegment StartX=108 StartY=34 StartZ=0 EndX=97 EndY=34 EndZ=0
    g17: LineSegment StartX=97 StartY=32.2 StartZ=0 EndX=97 EndY=31.4 EndZ=0
    g18: LineSegment StartX=97 StartY=31.4 StartZ=0 EndX=108 EndY=31.4 EndZ=0
    g19: LineSegment StartX=108 StartY=31.4 StartZ=0 EndX=108 EndY=32.2 EndZ=0
    g20: LineSegment StartX=108 StartY=32.2 StartZ=0 EndX=97 EndY=32.2 EndZ=0
  constraints (54):
    c: Vertical(g0)
    c: PointOnObject(g0,g-3)
    c: PointOnObject(g0,g-4)
    c: DistanceX(g0,g-5) = 11
    c: Coincident(g1,g2)
    c: Coincident(g2,g3)
    c: Coincident(g3,g4)
    c: Coincident(g4,g1)
    c: Horizontal(g2)
    c: Horizontal(g4)
    c: Tangent(g1,g0)
    c: Tangent(g3,g-5)
    c: DistanceY(g2,g3) = 0.8
    c: Coincident(g5,g6)
    c: Coincident(g6,g7)
    c: Coincident(g7,g8)
    c: Coincident(g8,g5)
    c: Horizontal(g6)
    c: Horizontal(g8)
    c: DistanceY(g6,g7) = 0.8
    c: Coincident(g9,g10)
    c: Coincident(g10,g11)
    c: Coincident(g11,g12)
    c: Coincident(g12,g9)
    c: Horizontal(g10)
    c: Horizontal(g12)
    c: DistanceY(g10,g11) = 0.8
    c: Tangent(g5,g0)
    c: Tangent(g7,g-5)
    c: Tangent(g9,g0)
    c: Tangent(g11,g-5)
    c: Coincident(g13,g14)
    c: Coincident(g14,g15)
    c: Coincident(g15,g16)
    c: Coincident(g16,g13)
    c: Horizontal(g14)
    c: Horizontal(g16)
    c: DistanceY(g14,g15) = 0.8
    c: Tangent(g13,g0)
    c: Tangent(g15,g-5)
    c: Coincident(g17,g18)
    c: Coincident(g18,g19)
    c: Coincident(g19,g20)
    c: Coincident(g20,g17)
    c: Horizontal(g18)
    c: Horizontal(g20)
    c: DistanceY(g18,g19) = 0.8
    c: Tangent(g17,g0)
    c: Tangent(g19,g-5)
    c: DistanceY(g1,g9) = 1
    c: DistanceY(g9,g17) = 1
    c: DistanceY(g17,g13) = 1
    c: DistanceY(g13,g5) = 1
    c: DistanceY(g0,g1) = 1
FEATURE [PartDesign::Pocket] Pocket004
  BaseFeature = -> Chamfer005
  Direction = (0,-1,2e-16)
  Length = 1
  Length2 = 5
  Profile = -> Sketch111
  ReferenceAxis = -> Sketch111 [N_Axis]
  Refine = true
  Suppressed = false
  Type = 0
FEATURE [PartDesign::Pad] Pad010
  BaseFeature = -> Pocket004
  Direction = (0,1,-2e-16)
  Length = 1.2
  Length2 = 10
  Profile = -> Sketch098
  ReferenceAxis = -> Sketch098 [N_Axis]
  Refine = true
  Suppressed = false
  Type = 0
FEATURE [PartDesign::Chamfer] Chamfer006
  Angle = 45
  Base = -> Pad010 [Edge291]
  BaseFeature = -> Pad010
  ChamferType = 1
  FlipDirection = false
  Refine = true
  Size = 1
  Size2 = 6
  SupportTransform = false
  Suppressed = false
  UseAllEdges = false
FEATURE [Sketcher::SketchObject] Sketch110
  ArcFitTolerance = 1e-06
  AttachmentSupport = -> [Pad010]
  ExternalGeometry = -> [Sketch098]
  FullyConstrained = true
  MakeInternals = false
  MapMode = 5
  Placement = pos=(0,4,-9e-16) rot=(0,0.707107,0.707107;3.14159rad)
  sketch-geometry (8):
    g0: LineSegment StartX=119.69 StartY=34 StartZ=0 EndX=130.69 EndY=34 EndZ=0
    g1: LineSegment StartX=119.95 StartY=33.2 StartZ=0 EndX=130.95 EndY=33.2 EndZ=0
    g2: LineSegment StartX=119.137 StartY=35.7 StartZ=0 EndX=130.137 EndY=35.7 EndZ=0
    g3: LineSegment StartX=118.877 StartY=36.5 StartZ=0 EndX=129.877 EndY=36.5 EndZ=0
    g4: LineSegment StartX=118.877 StartY=36.5 StartZ=0 EndX=119.137 EndY=35.7 EndZ=0
    g5: LineSegment StartX=129.877 StartY=36.5 StartZ=0 EndX=130.137 EndY=35.7 EndZ=0
    g6: LineSegment StartX=119.69 StartY=34 StartZ=0 EndX=119.95 EndY=33.2 EndZ=0
    g7: LineSegment StartX=130.69 StartY=34 StartZ=0 EndX=130.95 EndY=33.2 EndZ=0
  constraints (24):
    c: Horizontal(g0)
    c: Horizontal(g1)
    c: Horizontal(g2)
    c: Horizontal(g3)
    c: Equal(g1,g-5)
    c: Equal(g0,g-5)
    c: Equal(g2,g-5)
    c: Equal(g3,g-5)
    c: PointOnObject(g0,g-3)
    c: PointOnObject(g1,g-3)
    c: PointOnObject(g2,g-3)
    c: PointOnObject(g3,g-3)
    c: Coincident(g4,g3)
    c: Coincident(g4,g2)
    c: Coincident(g5,g3)
    c: Coincident(g5,g2)
    c: Coincident(g6,g0)
    c: Coincident(g6,g1)
    c: Coincident(g7,g0)
    c: Coincident(g7,g1)
    c: DistanceY(g1,g0) = 0.8
    c: DistanceY(g2,g3) = 0.8
    c: DistanceY(g-5,g1) = 2
    c: DistanceY(g-5,g2) = 4.5
FEATURE [PartDesign::Pocket] Pocket003
  BaseFeature = -> Chamfer006
  Direction = (0,-1,2e-16)
  Length = 1
  Length2 = 5
  Profile = -> Sketch110
  ReferenceAxis = -> Sketch110 [N_Axis]
  Refine = true
  Suppressed = false
  Type = 0
FEATURE [PartDesign::SubtractivePipe] SubtractivePipe
  AuxilleryCurvelinear = true
  AuxillerySpineTangent = false
  BaseFeature = -> Pocket003
  Binormal = (0,0,0)
  Mode = 0
  Profile = -> Sketch106
  Refine = true
  Spine = -> Pad008 [Edge215]
  SpineTangent = false
  Suppressed = false
  Transformation = 0
  Transition = 0
FEATURE [PartDesign::SubtractivePipe] SubtractivePipe001
  AuxilleryCurvelinear = true
  AuxillerySpineTangent = false
  BaseFeature = -> SubtractivePipe
  Binormal = (0,0,0)
  Mode = 0
  Profile = -> Sketch107
  Refine = true
  Spine = -> Pad008 [Edge213,Edge216,Edge210]
  SpineTangent = false
  Suppressed = false
  Transformation = 0
  Transition = 0
FEATURE [PartDesign::SubtractiveLoft] SubtractiveLoft
  BaseFeature = -> SubtractivePipe001
  Closed = false
  Profile = -> Sketch099
  Refine = true
  Ruled = false
  Sections = -> [Sketch108]
  Suppressed = false
FEATURE [PartDesign::SubtractiveLoft] SubtractiveLoft001
  BaseFeature = -> SubtractiveLoft
  Closed = false
  Profile = -> Clone2D
  Refine = true
  Ruled = false
  Sections = -> [Sketch109]
  Suppressed = false
FEATURE [Sketcher::SketchObject] Sketch112
  ArcFitTolerance = 1e-06
  AttachmentSupport = -> [Pad008]
  ExternalGeometry = -> [Binder]
  FullyConstrained = true
  MakeInternals = false
  MapMode = 5
  Placement = pos=(0,3.6,0) rot=(0,0.707107,0.707107;3.14159rad)
  sketch-geometry (4):
    g0: LineSegment [constr] StartX=167.782 StartY=-53.0314 StartZ=0 EndX=215.42 EndY=-53.0314 EndZ=0
    g1: GeomPoint [constr] X=191.282 Y=-53.0314 Z=0
    g2: Circle CenterX=191.282 CenterY=-53.0314 CenterZ=0 NormalX=0 NormalY=0 NormalZ=1 AngleXU=0 Radius=11.5
    g3: Circle CenterX=191.282 CenterY=-53.0314 CenterZ=0 NormalX=0 NormalY=0 NormalZ=1 AngleXU=0 Radius=10.7
  constraints (9):
    c: Horizontal(g0)
    c: PointOnObject(g0,g-3)
    c: Diameter(g2) = 23
    c: Coincident(g2,g1)
    c: Diameter(g3) = 21.4
    c: Coincident(g3,g1)
    c: DistanceX(g0,g1) = 23.5
    c: PointOnObject(g1,g0)
    c: Coincident(g0,g-4)
FEATURE [PartDesign::Chamfer] Chamfer016
  Angle = 45
  Base = -> SubtractiveLoft001 [Edge118,Edge117,Edge119,Edge120,Edge109]
  BaseFeature = -> SubtractiveLoft001
  ChamferType = 0
  FlipDirection = false
  Refine = true
  Size = 1.5
  Size2 = 1
  SupportTransform = false
  Suppressed = false
  UseAllEdges = false
FEATURE [PartDesign::Chamfer] Chamfer017
  Angle = 45
  Base = -> Chamfer016 [Edge15]
  BaseFeature = -> Chamfer016
  ChamferType = 0
  FlipDirection = false
  Refine = true
  Size = 1.6
  Size2 = 1
  SupportTransform = false
  Suppressed = false
  UseAllEdges = false
FEATURE [PartDesign::Chamfer] Chamfer018
  Angle = 45
  Base = -> Chamfer017 [Edge10]
  BaseFeature = -> Chamfer017
  ChamferType = 0
  FlipDirection = false
  Refine = true
  Size = 3.5
  Size2 = 1
  SupportTransform = false
  Suppressed = false
  UseAllEdges = false
FEATURE [PartDesign::Chamfer] Chamfer019
  Angle = 45
  Base = -> Chamfer018 [Edge94,Edge199]
  BaseFeature = -> Chamfer018
  ChamferType = 0
  FlipDirection = false
  Refine = true
  Size = 1.9
  Size2 = 1
  SupportTransform = false
  Suppressed = false
  UseAllEdges = false
FEATURE [PartDesign::Fillet] Fillet009
  Base = -> Chamfer019 [Edge83]
  BaseFeature = -> Chamfer019
  Radius = 1.1
  Refine = true
  SupportTransform = false
  Suppressed = false
  UseAllEdges = false
FEATURE [PartDesign::Fillet] Fillet010
  Base = -> Fillet009 [Edge77]
  BaseFeature = -> Fillet009
  Radius = 1.9
  Refine = true
  SupportTransform = false
  Suppressed = false
  UseAllEdges = false
FEATURE [PartDesign::Pocket] Pocket005
  BaseFeature = -> Fillet010
  Direction = (0,-1,2e-16)
  Length = 0.8
  Length2 = 5
  Profile = -> Sketch112
  ReferenceAxis = -> Sketch112 [N_Axis]
  Refine = true
  Suppressed = false
  Type = 0
FEATURE [Part::Part2DObjectPython] ShapeString001  # Draft 2D object (typed FeaturePython)
  FontFile = <path>
  Fuse = false
  Justification = 6
  JustificationReference = 0
  KeepLeftMargin = false
  MakeFace = true
  ObliqueAngle = 0
  Placement = pos=(-183.5,3.6,-57.5) rot=(0,0.707107,0.707107;3.14159rad)
  ScaleToSize = true
  Size = 10
  String = AS
  Tracking = 0
FEATURE [PartDesign::Pocket] Pocket013
  BaseFeature = -> Pocket005
  Direction = (-1e-16,-1,2e-16)
  Length = 1
  Length2 = 5
  Profile = -> ShapeString001
  ReferenceAxis = -> ShapeString001 [N_Axis]
  Refine = true
  Suppressed = false
  Type = 0
FEATURE [PartDesign::Body] Body006  label="lato SX"
  AllowCompound = false
  Group = -> [Binder,Pad019,Chamfer015,Pocket002,Sketch133,Sketch091,Pad005,Sketch092,Pocket001,Sketch093,Sketch094,Pad006,Sketch095,Pad007,Sketch096,Pad008,Sketch097,Pad009,Chamfer005,Pocket004,Sketch098,Pad010,Chamfer006,Pocket003,SubtractivePipe,SubtractivePipe001,Sketch099,Sketch106,Sketch107,Sketch108,Clone2D,Sketch109,SubtractiveLoft,SubtractiveLoft001,Sketch110,Sketch111,Sketch112,Chamfer016,Chamfer017,+7 more]
  Origin = -> Origin006
  Tip = -> Pocket013
FEATURE [PartDesign::Pad] Pad020
  Direction = (0,-1,2e-16)
  Length = 25.2
  Length2 = 10
  Midplane = true
  Placement = pos=(0,0,0) rot=(1,0,0;1.5708rad)
  Profile = -> Sketch021
  ReferenceAxis = -> Sketch021 [N_Axis]
  Refine = true
  Suppressed = false
  Type = 0
FEATURE [PartDesign::Body] Body001  label="perno fermo rumble e driver solenoide"
  AllowCompound = false
  Group = -> [Sketch021,Pad020]
  Origin = -> Origin001
  Tip = -> Pad020
FEATURE [PartDesign::Pad] Pad021
  Direction = (0,-1,2e-16)
  Length = 16.8
  Length2 = 10
  Midplane = true
  Placement = pos=(0,0,0) rot=(1,0,0;1.5708rad)
  Profile = -> Sketch061
  ReferenceAxis = -> Sketch061 [N_Axis]
  Refine = true
  Suppressed = false
  Type = 0
FEATURE [PartDesign::Pocket] Pocket014
  BaseFeature = -> Pad021
  Direction = (0,1,-2e-16)
  Length = 12.8
  Length2 = 5
  Midplane = true
  Placement = pos=(0,0,0) rot=(1,0,0;1.5708rad)
  Profile = -> Sketch062
  ReferenceAxis = -> Sketch062 [N_Axis]
  Refine = true
  Suppressed = false
  Type = 0
FEATURE [PartDesign::Pad] Pad022
  BaseFeature = -> Pocket014
  Direction = (0,-1,2e-16)
  Length = 7.6
  Length2 = 10
  Midplane = true
  Placement = pos=(0,0,0) rot=(1,0,0;1.5708rad)
  Profile = -> Sketch063
  ReferenceAxis = -> Sketch063 [N_Axis]
  Refine = true
  Suppressed = false
  Type = 0
FEATURE [PartDesign::Body] Body003  label="blocco switch"
  AllowCompound = false
  Group = -> [Sketch061,Sketch062,Sketch063,Pad021,Pocket014,Pad022]
  Origin = -> Origin003
  Tip = -> Pad022
FEATURE [PartDesign::Pad] Pad024
  Direction = (0,-1,2e-16)
  Length = 17
  Length2 = 10
  Midplane = true
  Placement = pos=(0,0,0) rot=(1,0,0;1.5708rad)
  Profile = -> Sketch045
  ReferenceAxis = -> Sketch045 [N_Axis]
  Refine = true
  Suppressed = false
  Type = 0
FEATURE [PartDesign::Pocket] Pocket015
  BaseFeature = -> Pad024
  Direction = (-1,0,0)
  Length = 8
  Length2 = 5
  Placement = pos=(0,0,0) rot=(1,0,0;1.5708rad)
  Profile = -> Sketch047
  ReferenceAxis = -> Sketch047 [N_Axis]
  Refine = true
  Reversed = true
  Suppressed = false
  Type = 0
FEATURE [PartDesign::Pocket] Pocket016
  BaseFeature = -> Pocket015
  Direction = (-1,0,0)
  Length = 1
  Length2 = 5
  Placement = pos=(0,0,0) rot=(1,0,0;1.5708rad)
  Profile = -> Sketch046
  ReferenceAxis = -> Sketch046 [N_Axis]
  Refine = true
  Reversed = true
  Suppressed = false
  Type = 0
FEATURE [PartDesign::Pocket] Pocket017
  BaseFeature = -> Pocket016
  Direction = (0,1,-2e-16)
  Length = 17
  Length2 = 5
  Midplane = true
  Placement = pos=(0,0,0) rot=(1,0,0;1.5708rad)
  Profile = -> Sketch048
  ReferenceAxis = -> Sketch048 [N_Axis]
  Refine = true
  Suppressed = false
  Type = 0
FEATURE [PartDesign::Pad] Pad025
  BaseFeature = -> Pocket017
  Direction = (0,-1,2e-16)
  Length = 17
  Length2 = 10
  Midplane = true
  Placement = pos=(0,0,0) rot=(1,0,0;1.5708rad)
  Profile = -> Sketch049
  ReferenceAxis = -> Sketch049 [N_Axis]
  Refine = true
  Suppressed = false
  Type = 0
FEATURE [PartDesign::Pad] Pad026
  BaseFeature = -> Pad025
  Direction = (0,-1,2e-16)
  Length = 17
  Length2 = 10
  Midplane = true
  Placement = pos=(0,0,0) rot=(1,0,0;1.5708rad)
  Profile = -> Sketch066
  ReferenceAxis = -> Sketch066 [N_Axis]
  Refine = true
  Suppressed = false
  Type = 0
FEATURE [PartDesign::Pad] Pad027
  BaseFeature = -> Pad026
  Direction = (0,-1,2e-16)
  Length = 5
  Length2 = 10
  Midplane = true
  Placement = pos=(0,0,0) rot=(1,0,0;1.5708rad)
  Profile = -> Sketch064
  ReferenceAxis = -> Sketch064 [N_Axis]
  Refine = true
  Suppressed = false
  Type = 0
FEATURE [PartDesign::Pad] Pad028
  BaseFeature = -> Pad027
  Direction = (1,0,0)
  Length = 1
  Length2 = 10
  Placement = pos=(0,0,0) rot=(1,0,0;1.5708rad)
  Profile = -> Sketch068
  ReferenceAxis = -> Sketch068 [N_Axis]
  Refine = true
  Reversed = true
  Suppressed = false
  Type = 0
FEATURE [PartDesign::Chamfer] Chamfer020
  Angle = 45
  Base = -> Pad028 [Edge73,Edge75,Edge78,Edge77]
  BaseFeature = -> Pad028
  ChamferType = 0
  FlipDirection = false
  Placement = pos=(0,0,0) rot=(1,0,0;1.5708rad)
  Refine = true
  Size = 0.5
  Size2 = 1
  SupportTransform = false
  Suppressed = false
  UseAllEdges = false
FEATURE [PartDesign::Body] Body002  label="supporto per neopixel"
  AllowCompound = false
  Group = -> [Sketch045,Sketch047,Sketch046,Sketch048,Sketch049,Sketch066,Sketch064,Sketch068,Pad024,Pocket015,Pocket016,Pocket017,Pad025,Pad026,Pad027,Pad028,Chamfer020]
  Origin = -> Origin002
  Tip = -> Chamfer020
FEATURE [Sketcher::SketchObject] Sketch134  label="perno fermo rumble002"
  ArcFitTolerance = 1e-06
  AttachmentSupport = -> [XZ_Plane008]
  FullyConstrained = true
  MakeInternals = false
  MapMode = 5
  Placement = pos=(0,0,0) rot=(1,0,0;1.5708rad)
  sketch-geometry (16):
    g0: LineSegment StartX=0 StartY=0.45 StartZ=0 EndX=0 EndY=1.55 EndZ=0
    g1: LineSegment StartX=0.45 StartY=2 StartZ=0 EndX=1.55 EndY=2 EndZ=0
    g2: LineSegment StartX=2 StartY=1.55 StartZ=0 EndX=2 EndY=0.45 EndZ=0
    g3: LineSegment StartX=1.55 StartY=0 StartZ=0 EndX=0.45 EndY=0 EndZ=0
    g4: ArcOfCircle [constr] CenterX=0.45 CenterY=1.55 CenterZ=0 NormalX=0 NormalY=0 NormalZ=1 AngleXU=0 Radius=0.45 StartAngle=1.5708 EndAngle=3.14159
    g5: GeomPoint [constr] X=0 Y=2 Z=0
    g6: LineSegment StartX=0.45 StartY=2 StartZ=0 EndX=0 EndY=1.55 EndZ=0
    g7: ArcOfCircle [constr] CenterX=1.55 CenterY=1.55 CenterZ=0 NormalX=0 NormalY=0 NormalZ=1 AngleXU=0 Radius=0.45 StartAngle=0 EndAngle=1.5708
    g8: GeomPoint [constr] X=2 Y=2 Z=0
    g9: LineSegment StartX=2 StartY=1.55 StartZ=0 EndX=1.55 EndY=2 EndZ=0
    g10: ArcOfCircle [constr] CenterX=1.55 CenterY=0.45 CenterZ=0 NormalX=0 NormalY=0 NormalZ=1 AngleXU=0 Radius=0.45 StartAngle=4.71239 EndAngle=6.28319
    g11: GeomPoint [constr] X=2 Y=0 Z=0
    g12: LineSegment StartX=1.55 StartY=0 StartZ=0 EndX=2 EndY=0.45 EndZ=0
    g13: ArcOfCircle [constr] CenterX=0.45 CenterY=0.45 CenterZ=0 NormalX=0 NormalY=0 NormalZ=1 AngleXU=0 Radius=0.45 StartAngle=3.14159 EndAngle=4.71239
    g14: GeomPoint [constr] X=0 Y=0 Z=0
    g15: LineSegment StartX=0 StartY=0.45 StartZ=0 EndX=0.45 EndY=0 EndZ=0
  constraints (35):
    c: Coincident(g14,g-1)
    c: PointOnObject(g5,g-2)
    c: Horizontal(g1)
    c: Vertical(g2)
    c: Horizontal(g3)
    c: DistanceX(g5,g8) = 2
    c: DistanceY(g11,g8) = 2
    c: PointOnObject(g5,g0)
    c: PointOnObject(g5,g1)
    c: Tangent(g0,g4) = 1.5708
    c: Tangent(g1,g4) = 1.5708
    c: Coincident(g6,g0)
    c: Coincident(g6,g1)
    c: PointOnObject(g8,g2)
    c: PointOnObject(g8,g1)
    c: Tangent(g2,g7) = 1.5708
    c: Tangent(g1,g7) = 1.5708
    c: Coincident(g9,g2)
    c: Coincident(g9,g1)
    c: PointOnObject(g11,g2)
    c: PointOnObject(g11,g3)
    c: Tangent(g2,g10) = 1.5708
    c: Tangent(g3,g10) = 1.5708
    c: Coincident(g12,g2)
    c: Coincident(g12,g3)
    c: PointOnObject(g14,g0)
    c: PointOnObject(g14,g3)
    c: Tangent(g0,g13) = 1.5708
    c: Tangent(g3,g13) = 1.5708
    c: Coincident(g15,g0)
    c: Coincident(g15,g3)
    c: Equal(g6,g9)
    c: Equal(g9,g12)
    c: Equal(g12,g15)
    c: DistanceX(g14,g3) = 0.45
FEATURE [PartDesign::Pad] Pad029
  Direction = (0,-1,2e-16)
  Length = 17
  Length2 = 10
  Midplane = true
  Placement = pos=(0,0,0) rot=(1,0,0;1.5708rad)
  Profile = -> Sketch134
  ReferenceAxis = -> Sketch134 [N_Axis]
  Refine = true
  Suppressed = false
  Type = 0
FEATURE [PartDesign::Body] Body008  label="perno fermo neopixel"
  AllowCompound = false
  Group = -> [Sketch134,Pad029]
  Origin = -> Origin008
  Tip = -> Pad029
FEATURE [Sketcher::SketchObject] Sketch135  label="perno fermo rumble003"
  ArcFitTolerance = 1e-06
  AttachmentSupport = -> [XZ_Plane009]
  FullyConstrained = true
  MakeInternals = false
  MapMode = 5
  Placement = pos=(0,0,0) rot=(1,0,0;1.5708rad)
  sketch-geometry (16):
    g0: LineSegment StartX=4.69e-14 StartY=0.8 StartZ=0 EndX=-3.04e-14 EndY=3.1 EndZ=0
    g1: LineSegment StartX=0.8 StartY=3.9 StartZ=0 EndX=3.1 EndY=3.9 EndZ=0
    g2: LineSegment StartX=3.9 StartY=3.1 StartZ=0 EndX=3.9 EndY=0.8 EndZ=0
    g3: LineSegment StartX=3.1 StartY=0 StartZ=0 EndX=0.8 EndY=0 EndZ=0
    g4: ArcOfCircle [constr] CenterX=0.8 CenterY=3.1 CenterZ=0 NormalX=0 NormalY=0 NormalZ=1 AngleXU=0 Radius=0.8 StartAngle=1.5708 EndAngle=3.14159
    g5: GeomPoint [constr] X=0 Y=3.9 Z=0
    g6: LineSegment StartX=0.8 StartY=3.9 StartZ=0 EndX=-3.04e-14 EndY=3.1 EndZ=0
    g7: ArcOfCircle [constr] CenterX=3.1 CenterY=3.1 CenterZ=0 NormalX=0 NormalY=0 NormalZ=1 AngleXU=0 Radius=0.8 StartAngle=-2.4e-14 EndAngle=1.5708
    g8: GeomPoint [constr] X=3.9 Y=3.9 Z=0
    g9: LineSegment StartX=3.9 StartY=3.1 StartZ=0 EndX=3.1 EndY=3.9 EndZ=0
    g10: ArcOfCircle [constr] CenterX=3.1 CenterY=0.8 CenterZ=0 NormalX=0 NormalY=0 NormalZ=1 AngleXU=0 Radius=0.8 StartAngle=4.71239 EndAngle=6.28319
    g11: GeomPoint [constr] X=3.9 Y=0 Z=0
    g12: LineSegment StartX=3.1 StartY=0 StartZ=0 EndX=3.9 EndY=0.8 EndZ=0
    g13: ArcOfCircle [constr] CenterX=0.8 CenterY=0.8 CenterZ=0 NormalX=0 NormalY=0 NormalZ=1 AngleXU=0 Radius=0.8 StartAngle=3.14159 EndAngle=4.71239
    g14: GeomPoint [constr] X=0 Y=0 Z=0
    g15: LineSegment StartX=4.69e-14 StartY=0.8 StartZ=0 EndX=0.8 EndY=0 EndZ=0
  constraints (35):
    c: Coincident(g14,g-1)
    c: PointOnObject(g5,g-2)
    c: Horizontal(g1)
    c: Vertical(g2)
    c: Horizontal(g3)
    c: DistanceX(g5,g8) = 3.9
    c: DistanceY(g11,g8) = 3.9
    c: PointOnObject(g5,g0)
    c: PointOnObject(g5,g1)
    c: Tangent(g0,g4) = 1.5708
    c: Tangent(g1,g4) = 1.5708
    c: Coincident(g6,g0)
    c: Coincident(g6,g1)
    c: PointOnObject(g8,g2)
    c: PointOnObject(g8,g1)
    c: Tangent(g2,g7) = 1.5708
    c: Tangent(g1,g7) = 1.5708
    c: Coincident(g9,g2)
    c: Coincident(g9,g1)
    c: PointOnObject(g11,g2)
    c: PointOnObject(g11,g3)
    c: Tangent(g2,g10) = 1.5708
    c: Tangent(g3,g10) = 1.5708
    c: Coincident(g12,g2)
    c: Coincident(g12,g3)
    c: PointOnObject(g14,g0)
    c: PointOnObject(g14,g3)
    c: Tangent(g0,g13) = 1.5708
    c: Tangent(g3,g13) = 1.5708
    c: Coincident(g15,g0)
    c: Coincident(g15,g3)
    c: Equal(g6,g9)
    c: Equal(g9,g12)
    c: Equal(g12,g15)
    c: DistanceX(g14,g3) = 0.8
FEATURE [PartDesign::Pad] Pad030
  Direction = (0,-1,2e-16)
  Length = 25.2
  Length2 = 10
  Midplane = true
  Placement = pos=(0,0,0) rot=(1,0,0;1.5708rad)
  Profile = -> Sketch135
  ReferenceAxis = -> Sketch135 [N_Axis]
  Refine = true
  Suppressed = false
  Type = 0
FEATURE [PartDesign::Body] Body009  label="perno fermo switch - caricabatterie - grilletto"
  AllowCompound = false
  Group = -> [Sketch135,Pad030]
  Origin = -> Origin009
  Tip = -> Pad030
FEATURE [Sketcher::SketchObject] Sketch136  label="scavo_rele"
  ArcFitTolerance = 1e-06
  AttachmentSupport = -> [XZ_Plane]
  ExternalGeometry = -> [Sketch]
  FullyConstrained = true
  MakeInternals = false
  MapMode = 5
  Placement = pos=(0,0,0) rot=(1,0,0;1.5708rad)
  sketch-geometry (7):
    g0: LineSegment [constr] StartX=-168.686 StartY=-49.3292 StartZ=0 EndX=-170.664 EndY=-55.416 EndZ=0
    g1: LineSegment [constr] StartX=-168.686 StartY=-49.3292 StartZ=0 EndX=-164.882 EndY=-50.5653 EndZ=0
    g2: LineSegment [constr] StartX=-168.686 StartY=-49.3292 StartZ=0 EndX=-172.3 EndY=-48.155 EndZ=0
    g3: LineSegment StartX=-172.3 StartY=-48.155 StartZ=0 EndX=-164.882 EndY=-50.5653 EndZ=0
    g4: LineSegment StartX=-172.3 StartY=-48.155 StartZ=0 EndX=-174.278 EndY=-54.2417 EndZ=0
    g5: LineSegment StartX=-164.882 StartY=-50.5653 StartZ=0 EndX=-166.86 EndY=-56.6521 EndZ=0
    g6: LineSegment StartX=-174.278 StartY=-54.2417 StartZ=0 EndX=-166.86 EndY=-56.6521 EndZ=0
  constraints (19):
    c: Tangent(g0,g-3)
    c: Distance(g0,g-3) = 75
    c: Distance(g0,g0) = 6.4
    c: Coincident(g1,g0)
    c: Coincident(g2,g0)
    c: Distance(g2) = 3.8
    c: Distance(g1) = 4
    c: Perpendicular(g0,g1)
    c: Perpendicular(g0,g2)
    c: Coincident(g3,g2)
    c: Coincident(g3,g1)
    c: Equal(g4,g0)
    c: Equal(g5,g0)
    c: Parallel(g4,g0)
    c: Parallel(g5,g0)
    c: Coincident(g4,g2)
    c: Coincident(g5,g1)
    c: Coincident(g6,g4)
    c: Coincident(g6,g5)
FEATURE [Part::Extrusion] Extrude076  label="Extrude076 - scavo_rele"
  Base = -> Sketch136
  Dir = (0,-1,2e-16)
  DirMode = 2
  FaceMakerClass = Part::FaceMakerBullseye
  FaceMakerMode = 3
  LengthFwd = 10.4
  LengthRev = 0
  Solid = true
  Symmetric = true
FEATURE [Sketcher::SketchObject] Sketch137  label="scavo_nuovo_driver"
  ArcFitTolerance = 1e-06
  AttachmentSupport = -> [XZ_Plane]
  ExternalGeometry = -> [Sketch]
  FullyConstrained = true
  MakeInternals = false
  MapMode = 5
  Placement = pos=(0,0,0) rot=(1,0,0;1.5708rad)
  sketch-geometry (7):
    g0: LineSegment [constr] StartX=-171.776 StartY=-58.8398 StartZ=0 EndX=-175.794 EndY=-71.2035 EndZ=0
    g1: LineSegment [constr] StartX=-171.776 StartY=-58.8398 StartZ=0 EndX=-170.255 EndY=-59.3342 EndZ=0
    g2: LineSegment [constr] StartX=-171.776 StartY=-58.8398 StartZ=0 EndX=-175.39 EndY=-57.6655 EndZ=0
    g3: LineSegment StartX=-175.39 StartY=-57.6655 StartZ=0 EndX=-170.255 EndY=-59.3342 EndZ=0
    g4: LineSegment StartX=-175.39 StartY=-57.6655 StartZ=0 EndX=-179.408 EndY=-70.0293 EndZ=0
    g5: LineSegment StartX=-170.255 StartY=-59.3342 StartZ=0 EndX=-174.272 EndY=-71.698 EndZ=0
    g6: LineSegment StartX=-179.408 StartY=-70.0293 StartZ=0 EndX=-174.272 EndY=-71.698 EndZ=0
  constraints (19):
    c: Distance(g0,g-3) = 85
    c: Distance(g0) = 13
    c: Tangent(g0,g-3)
    c: Coincident(g1,g0)
    c: Coincident(g2,g0)
    c: Distance(g1) = 1.6
    c: Distance(g2) = 3.8
    c: Perpendicular(g0,g1)
    c: Perpendicular(g0,g2)
    c: Coincident(g3,g2)
    c: Coincident(g3,g1)
    c: Equal(g4,g0)
    c: Equal(g5,g0)
    c: Parallel(g4,g0)
    c: Parallel(g5,g0)
    c: Coincident(g4,g2)
    c: Coincident(g5,g1)
    c: Coincident(g6,g4)
    c: Coincident(g6,g5)
FEATURE [PartDesign::Body] Body  label="Struttura pistola"
  AllowCompound = false
  Group = -> [Sketch,Sketch002,Sketch004,DatumPlane,Sketch005,DatumPlane001,CopyCut,Sketch008,Sketch009,Sketch010,Sketch011,Sketch012,Sketch013,Sketch014,Sketch015,Sketch016,Sketch017,Sketch018,Sketch019,Sketch020,Sketch022,Sketch023,Sketch024,Sketch025,Sketch026,Sketch027,Sketch029,Sketch030,Sketch031,Sketch032,Sketch033,Sketch034,Sketch035,Sketch036,Sketch037,Sketch038,Sketch039,Sketch040,Sketch041,Sketch042,+17 more]
  Origin = -> Origin
FEATURE [Part::Extrusion] Extrude077  label="Extrude077 - scavo_nuovo_driver"
  Base = -> Sketch137
  Dir = (0,-1,2e-16)
  DirMode = 2
  FaceMakerClass = Part::FaceMakerBullseye
  FaceMakerMode = 3
  LengthFwd = 16.8
  LengthRev = 0
  Solid = true
  Symmetric = true
FEATURE [Part::Cut] Cut044
  Base = -> Cut043
  Refine = true
  Tool = -> Extrude076
FEATURE [Part::Cut] Cut045
  Base = -> Cut044
  Refine = true
  Tool = -> Extrude077
note: 2 file-system paths scrubbed to <path> (originals preserved in the JSON sidecar)
